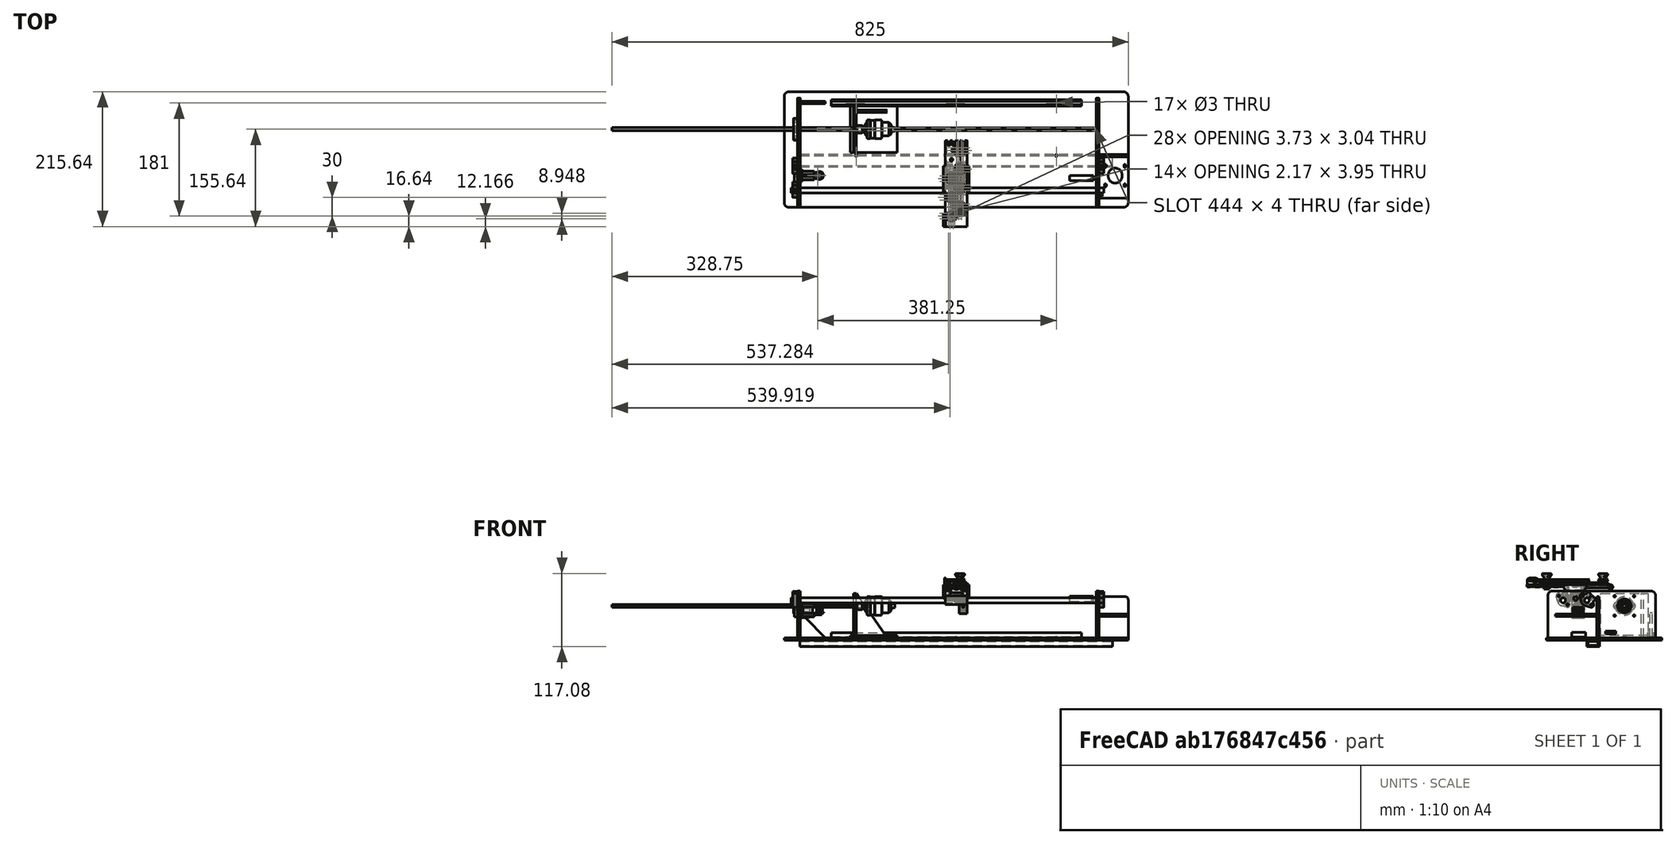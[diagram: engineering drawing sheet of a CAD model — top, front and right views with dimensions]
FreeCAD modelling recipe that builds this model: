
FCSTD DOCUMENT  (FreeCAD 0.18R16131 (Git))
Label: Nawijarka
License: All rights reserved
LicenseURL: http://en.wikipedia.org/wiki/All_rights_reserved
objects: Sketcher::SketchObject×83, PartDesign::Body×59, PartDesign::Pad×39, PartDesign::Pocket×37, PartDesign::FeatureBase×29, PartDesign::Mirrored×16, PartDesign::Revolution×7, Mesh::Feature×4, PartDesign::Chamfer×3, PartDesign::PolarPattern×3, PartDesign::MultiTransform×2, Spreadsheet::Sheet×1, PartDesign::LinearPattern×1, PartDesign::AdditiveCylinder×1, Part::Feature×1
note: 365 computed .brp shape members not serialized (recipe doc carries the construction recipe); baked Part::Feature solids carry a one-line shape summary decoded from their .brp

FEATURE [Sketcher::SketchObject] Sketch
  MapMode = 5
  Support = -> [XY_Plane]
  sketch-geometry (8):
    g0: LineSegment StartX=-267 StartY=110 StartZ=0 EndX=267 EndY=110 EndZ=0
    g1: LineSegment StartX=275 StartY=102 StartZ=0 EndX=275 EndY=-67 EndZ=0
    g2: LineSegment StartX=267 StartY=-75 StartZ=0 EndX=-267 EndY=-75 EndZ=0
    g3: LineSegment StartX=-275 StartY=-67 StartZ=0 EndX=-275 EndY=102 EndZ=0
    g4: ArcOfCircle CenterX=267 CenterY=102 CenterZ=0 NormalX=0 NormalY=0 NormalZ=1 AngleXU=0 Radius=8 StartAngle=6.6112e-12 EndAngle=1.5708
    g5: ArcOfCircle CenterX=267 CenterY=-67 CenterZ=0 NormalX=0 NormalY=0 NormalZ=1 AngleXU=0 Radius=8 StartAngle=4.71239 EndAngle=6.28319
    g6: ArcOfCircle CenterX=-267 CenterY=-67 CenterZ=0 NormalX=0 NormalY=0 NormalZ=1 AngleXU=0 Radius=8 StartAngle=3.14159 EndAngle=4.71239
    g7: ArcOfCircle CenterX=-267 CenterY=102 CenterZ=0 NormalX=0 NormalY=0 NormalZ=1 AngleXU=0 Radius=8 StartAngle=1.5708 EndAngle=3.14159
  constraints (19):
    c: Horizontal(g0)
    c: Horizontal(g2)
    c: Vertical(g1)
    c: Vertical(g3)
    c: Tangent(g0,g4) = 1.5708
    c: Tangent(g1,g4) = 1.5708
    c: Tangent(g2,g5) = 1.5708
    c: Tangent(g1,g5) = 1.5708
    c: Tangent(g2,g6) = 1.5708
    c: Tangent(g3,g6) = 1.5708
    c: Tangent(g3,g7) = 1.5708
    c: Tangent(g0,g7) = 1.5708
    c: Equal(g2,g0)
    c: Equal(g1,g3)
    c: Radius(g6) = 8
    c: DistanceX(g3,g1) = 550
    c: Symmetric(g6,g5,g-2)
    c: DistanceY(g2) = -75
    c: DistanceY(g0) = 110
FEATURE [Spreadsheet::Sheet] Spreadsheet  label="SS"
  cells = A2=thickness_; B2(thickness)==4mm
FEATURE [PartDesign::Pad] Pad
  Length = 4
  Length2 = 100
  Profile = -> Sketch
  Type = 0
  expr: Length = SS.thickness
FEATURE [Mesh::Feature] Motor_NEMA17
  Placement = pos=(254,-24,21) rot=(0,0,1;0rad)
FEATURE [Sketcher::SketchObject] Sketch001
  MapMode = 5
  Placement = pos=(0,0,0) rot=(0.57735,0.57735,0.57735;2.0944rad)
  Support = -> [YZ_Plane001]
  expr: Constraints[5] = SS.thickness
  sketch-geometry (6):
    g0: LineSegment StartX=-64.5 StartY=79 StartZ=0 EndX=92 EndY=79 EndZ=0
    g1: LineSegment StartX=100 StartY=71 StartZ=0 EndX=100 EndY=4 EndZ=0
    g2: LineSegment StartX=100 StartY=4 StartZ=0 EndX=-72.5 EndY=4 EndZ=0
    g3: LineSegment StartX=-72.5 StartY=4 StartZ=0 EndX=-72.5 EndY=71 EndZ=0
    g4: ArcOfCircle CenterX=-64.5 CenterY=71 CenterZ=0 NormalX=0 NormalY=0 NormalZ=1 AngleXU=0 Radius=8 StartAngle=1.5708 EndAngle=3.14159
    g5: ArcOfCircle CenterX=92 CenterY=71 CenterZ=0 NormalX=0 NormalY=0 NormalZ=1 AngleXU=0 Radius=8 StartAngle=7e-16 EndAngle=1.5708
  constraints (16):
    c: Coincident(g1,g2)
    c: Coincident(g2,g3)
    c: Horizontal(g0)
    c: Vertical(g1)
    c: Vertical(g3)
    c: DistanceY(g1) = 4
    c: Tangent(g0,g4) = 1.5708
    c: Tangent(g3,g4) = 1.5708
    c: Tangent(g0,g5) = 1.5708
    c: Tangent(g1,g5) = 1.5708
    c: Equal(g5,g4)
    c: Radius(g4) = 8
    c: DistanceY(g2,g0) = 75
    c: DistanceX(g2) = -72.5
    c: DistanceX(g-1,g1) = 100
    c: Horizontal(g2)
FEATURE [PartDesign::Pad] Pad001
  Length = 4
  Length2 = 100
  Placement = pos=(0,0,0) rot=(0.57735,0.57735,0.57735;2.0944rad)
  Profile = -> Sketch001
  Type = 0
  expr: Length = SS.thickness
FEATURE [Sketcher::SketchObject] Sketch002
  ExternalGeometry = -> [Pad001]
  MapMode = 5
  Placement = pos=(4,-9e-16,9e-16) rot=(0.57735,0.57735,0.57735;2.0944rad)
  Support = -> [Pad001]
  sketch-geometry (12):
    g0: Circle CenterX=-48 CenterY=64 CenterZ=0 NormalX=0 NormalY=0 NormalZ=1 AngleXU=0 Radius=3.9
    g1: Circle CenterX=-10 CenterY=64 CenterZ=0 NormalX=0 NormalY=0 NormalZ=1 AngleXU=0 Radius=3.9
    g2: Circle CenterX=-40.9289 CenterY=56.9289 CenterZ=0 NormalX=0 NormalY=0 NormalZ=1 AngleXU=0 Radius=1.5
    g3: Circle CenterX=-55.0711 CenterY=71.0711 CenterZ=0 NormalX=0 NormalY=0 NormalZ=1 AngleXU=0 Radius=1.5
    g4: Circle CenterX=-17.0711 CenterY=71.0711 CenterZ=0 NormalX=0 NormalY=0 NormalZ=1 AngleXU=0 Radius=1.5
    g5: Circle CenterX=-2.92893 CenterY=56.9289 CenterZ=0 NormalX=0 NormalY=0 NormalZ=1 AngleXU=0 Radius=1.5
    g6: LineSegment [constr] StartX=-55.0711 StartY=71.0711 StartZ=0 EndX=-40.9289 EndY=56.9289 EndZ=0
    g7: LineSegment [constr] StartX=-17.0711 StartY=71.0711 StartZ=0 EndX=-2.92893 EndY=56.9289 EndZ=0
    g8: LineSegment StartX=-32 StartY=53 StartZ=0 EndX=-16 EndY=53 EndZ=0
    g9: LineSegment StartX=-16 StartY=53 StartZ=0 EndX=-16 EndY=44 EndZ=0
    g10: LineSegment StartX=-16 StartY=44 StartZ=0 EndX=-32 EndY=44 EndZ=0
    g11: LineSegment StartX=-32 StartY=44 StartZ=0 EndX=-32 EndY=53 EndZ=0
  constraints (32):
    c: Equal(g1,g0)
    c: Radius(g0) = 3.9
    c: Coincident(g5,g7)
    c: Coincident(g2,g6)
    c: Coincident(g3,g6)
    c: Symmetric(g2,g3,g0)
    c: Symmetric(g4,g5,g1)
    c: Equal(g4,g5)
    c: Equal(g5,g2)
    c: Equal(g2,g3)
    c: Radius(g2) = 1.5
    c: Coincident(g4,g7)
    c: Equal(g7,g6)
    c: Distance(g4,g5) = 20
    c: Angle(g7) = -0.785398
    c: Angle(g6) = -0.785398
    c: Coincident(g8,g9)
    c: Coincident(g9,g10)
    c: Coincident(g10,g11)
    c: Coincident(g11,g8)
    c: Horizontal(g8)
    c: Horizontal(g10)
    c: Vertical(g9)
    c: Vertical(g11)
    c: DistanceX(g10,g10) = 16
    c: DistanceY(g11,g11) = 9
    c: DistanceY(g-3,g10) = 40
    c: DistanceY(g0) = 64
    c: Horizontal(g0,g1)
    c: DistanceX(g0,g1) = 38
    c: DistanceX(g1) = -10
    c: DistanceX(g9) = -16
FEATURE [PartDesign::Pocket] Pocket
  BaseFeature = -> Pad001
  Length = 5
  Length2 = 100
  Placement = pos=(0,0,0) rot=(0.57735,0.57735,0.57735;2.0944rad)
  Profile = -> Sketch002
  Type = 1
FEATURE [Sketcher::SketchObject] Sketch003
  MapMode = 5
  Placement = pos=(0,0,0) rot=(1,0,0;1.5708rad)
  Support = -> [XZ_Plane002]
  expr: Constraints[5] = SS.thickness
  sketch-geometry (5):
    g0: LineSegment StartX=0 StartY=4 StartZ=0 EndX=47 EndY=4 EndZ=0
    g1: LineSegment StartX=47 StartY=4 StartZ=0 EndX=47 EndY=65 EndZ=0
    g2: LineSegment StartX=42 StartY=70 StartZ=0 EndX=0 EndY=70 EndZ=0
    g3: LineSegment StartX=0 StartY=70 StartZ=0 EndX=0 EndY=4 EndZ=0
    g4: ArcOfCircle CenterX=42 CenterY=65 CenterZ=0 NormalX=0 NormalY=0 NormalZ=1 AngleXU=0 Radius=5 StartAngle=2e-16 EndAngle=1.5708
  constraints (14):
    c: Coincident(g0,g1)
    c: Coincident(g2,g3)
    c: Coincident(g3,g0)
    c: Horizontal(g0)
    c: Horizontal(g2)
    c: DistanceY(g0) = 4
    c: Vertical(g1)
    c: Tangent(g1,g4) = -1.5708
    c: Tangent(g2,g4) = -1.5708
    c: Radius(g4) = 5
    c: DistanceX(g-1,g0) = 47
    c: DistanceY(g2) = 70
    c: Vertical(g3)
    c: PointOnObject(g2,g-2)
FEATURE [PartDesign::Pad] Pad002
  Length = 4
  Length2 = 100
  Placement = pos=(0,0,0) rot=(1,0,0;1.5708rad)
  Profile = -> Sketch003
  Type = 0
  expr: Length = SS.thickness
FEATURE [PartDesign::Body] Body002  label="motor_plate_1"
  Group = -> [Sketch003,Pad002]
  Origin = -> Origin002
  Placement = pos=(228,-60,0) rot=(0,0,1;0rad)
  Tip = -> Pad002
FEATURE [PartDesign::FeatureBase] Clone
  BaseFeature = -> Body002
  Placement = pos=(230,-57,0) rot=(0,0,1;0rad)
FEATURE [PartDesign::Body] Body003  label="motor_plate_2"
  BaseFeature = -> Body002
  Group = -> [Clone]
  Origin = -> Origin003
  Placement = pos=(-2.1,66.7,0) rot=(0,0,1;0rad)
  Tip = -> Clone
FEATURE [Sketcher::SketchObject] Sketch004
  MapMode = 5
  Support = -> [XY_Plane004]
  sketch-geometry (4):
    g0: LineSegment StartX=-23.5 StartY=30 StartZ=0 EndX=23.5 EndY=30 EndZ=0
    g1: LineSegment StartX=23.5 StartY=30 StartZ=0 EndX=23.5 EndY=-36 EndZ=0
    g2: LineSegment StartX=23.5 StartY=-36 StartZ=0 EndX=-23.5 EndY=-36 EndZ=0
    g3: LineSegment StartX=-23.5 StartY=-36 StartZ=0 EndX=-23.5 EndY=30 EndZ=0
  constraints (11):
    c: Coincident(g0,g1)
    c: Coincident(g1,g2)
    c: Coincident(g2,g3)
    c: Coincident(g3,g0)
    c: Horizontal(g0)
    c: Vertical(g1)
    c: Vertical(g3)
    c: DistanceX(g2,g2) = 47
    c: DistanceY(g1) = -36
    c: DistanceY(g0) = 30
    c: Symmetric(g1,g2,g-2)
FEATURE [PartDesign::Pad] Pad003
  Length = 4
  Length2 = 100
  Profile = -> Sketch004
  Type = 0
  expr: Length = SS.thickness
FEATURE [Sketcher::SketchObject] Sketch005
  ExternalGeometry = -> [Pad003]
  MapMode = 5
  Placement = pos=(0,0,4) rot=(0,0,1;0rad)
  Support = -> [Pad003]
  sketch-geometry (25):
    g0: LineSegment [constr] StartX=-13 StartY=15.5 StartZ=0 EndX=18 EndY=15.5 EndZ=0
    g1: LineSegment [constr] StartX=18 StartY=15.5 StartZ=0 EndX=18 EndY=-15.5 EndZ=0
    g2: LineSegment [constr] StartX=18 StartY=-15.5 StartZ=0 EndX=-13 EndY=-15.5 EndZ=0
    g3: LineSegment [constr] StartX=-13 StartY=-15.5 StartZ=0 EndX=-13 EndY=15.5 EndZ=0
    g4: ArcOfCircle CenterX=2.5 CenterY=1 CenterZ=0 NormalX=0 NormalY=0 NormalZ=1 AngleXU=0 Radius=11 StartAngle=1e-16 EndAngle=3.14159
    g5: ArcOfCircle CenterX=2.5 CenterY=-1 CenterZ=0 NormalX=0 NormalY=0 NormalZ=1 AngleXU=0 Radius=11 StartAngle=3.14159 EndAngle=6.28319
    g6: LineSegment StartX=-8.5 StartY=1 StartZ=0 EndX=-8.5 EndY=-1 EndZ=0
    g7: LineSegment StartX=13.5 StartY=1 StartZ=0 EndX=13.5 EndY=-1 EndZ=0
    g8: ArcOfCircle CenterX=-13 CenterY=16.5 CenterZ=0 NormalX=0 NormalY=0 NormalZ=1 AngleXU=0 Radius=1.5 StartAngle=1e-15 EndAngle=3.14159
    g9: ArcOfCircle CenterX=-13 CenterY=14.5 CenterZ=0 NormalX=0 NormalY=0 NormalZ=1 AngleXU=0 Radius=1.5 StartAngle=3.14159 EndAngle=6.28319
    g10: LineSegment StartX=-14.5 StartY=16.5 StartZ=0 EndX=-14.5 EndY=14.5 EndZ=0
    g11: LineSegment StartX=-11.5 StartY=16.5 StartZ=0 EndX=-11.5 EndY=14.5 EndZ=0
    g12: ArcOfCircle CenterX=18 CenterY=16.5 CenterZ=0 NormalX=0 NormalY=0 NormalZ=1 AngleXU=0 Radius=1.5 StartAngle=-9e-16 EndAngle=3.14159
    g13: ArcOfCircle CenterX=18 CenterY=14.5 CenterZ=0 NormalX=0 NormalY=0 NormalZ=1 AngleXU=0 Radius=1.5 StartAngle=3.14159 EndAngle=6.28319
    g14: LineSegment StartX=16.5 StartY=16.5 StartZ=0 EndX=16.5 EndY=14.5 EndZ=0
    g15: LineSegment StartX=19.5 StartY=16.5 StartZ=0 EndX=19.5 EndY=14.5 EndZ=0
    g16: ArcOfCircle CenterX=18 CenterY=-14.5 CenterZ=0 NormalX=0 NormalY=0 NormalZ=1 AngleXU=0 Radius=1.5 StartAngle=6e-16 EndAngle=3.14159
    g17: ArcOfCircle CenterX=18 CenterY=-16.5 CenterZ=0 NormalX=0 NormalY=0 NormalZ=1 AngleXU=0 Radius=1.5 StartAngle=3.14159 EndAngle=6.28319
    g18: LineSegment StartX=16.5 StartY=-14.5 StartZ=0 EndX=16.5 EndY=-16.5 EndZ=0
    g19: LineSegment StartX=19.5 StartY=-14.5 StartZ=0 EndX=19.5 EndY=-16.5 EndZ=0
    g20: ArcOfCircle CenterX=-13 CenterY=-14.5 CenterZ=0 NormalX=0 NormalY=0 NormalZ=1 AngleXU=0 Radius=1.5 StartAngle=2e-16 EndAngle=3.14159
    g21: ArcOfCircle CenterX=-13 CenterY=-16.5 CenterZ=0 NormalX=0 NormalY=0 NormalZ=1 AngleXU=0 Radius=1.5 StartAngle=3.14159 EndAngle=6.28319
    g22: LineSegment StartX=-14.5 StartY=-14.5 StartZ=0 EndX=-14.5 EndY=-16.5 EndZ=0
    g23: LineSegment StartX=-11.5 StartY=-14.5 StartZ=0 EndX=-11.5 EndY=-16.5 EndZ=0
    g24: GeomPoint X=2.5 Y=6e-16 Z=0
  constraints (57):
    c: Coincident(g0,g1)
    c: Coincident(g1,g2)
    c: Coincident(g2,g3)
    c: Coincident(g3,g0)
    c: Horizontal(g0)
    c: Horizontal(g2)
    c: Vertical(g3)
    c: Equal(g2,g1)
    c: DistanceX(g2,g2) = 31
    c: Tangent(g4,g7) = 1.5708
    c: Tangent(g4,g6) = -1.5708
    c: Tangent(g6,g5) = -1.5708
    c: Tangent(g7,g5) = 1.5708
    c: Vertical(g6)
    c: Tangent(g8,g11) = 1.5708
    c: Tangent(g8,g10) = -1.5708
    c: Tangent(g10,g9) = -1.5708
    c: Tangent(g11,g9) = 1.5708
    c: Vertical(g10)
    c: Equal(g8,g9)
    c: Tangent(g12,g15) = 1.5708
    c: Tangent(g12,g14) = -1.5708
    c: Tangent(g14,g13) = -1.5708
    c: Tangent(g15,g13) = 1.5708
    c: Vertical(g14)
    c: Equal(g12,g13)
    c: Tangent(g16,g19) = 1.5708
    c: Tangent(g16,g18) = -1.5708
    c: Tangent(g18,g17) = -1.5708
    c: Tangent(g19,g17) = 1.5708
    c: Vertical(g18)
    c: Equal(g16,g17)
    c: Tangent(g20,g23) = 1.5708
    c: Tangent(g20,g22) = -1.5708
    c: Tangent(g22,g21) = -1.5708
    c: Tangent(g23,g21) = 1.5708
    c: Vertical(g22)
    c: Equal(g20,g21)
    c: Symmetric(g8,g9,g0)
    c: Symmetric(g20,g21,g2)
    c: Symmetric(g16,g17,g1)
    c: Symmetric(g13,g12,g0)
    c: Radius(g13) = 1.5
    c: Equal(g13,g9)
    c: Equal(g13,g20)
    c: Equal(g13,g16)
    c: Equal(g18,g22)
    c: Equal(g22,g10)
    c: Equal(g10,g14)
    c: DistanceY(g10,g10) = 2
    c: DistanceY(g6,g6) = 2
    c: Radius(g4) = 11
    c: Symmetric(g5,g4,g-1)
    c: Symmetric(g1,g0,g-1)
    c: Vertical(g5,g24)
    c: Symmetric(g1,g0,g24)
    c: DistanceX(g24,g-3) = 21
FEATURE [PartDesign::Pocket] Pocket001
  BaseFeature = -> Pad003
  Length = 5
  Length2 = 100
  Profile = -> Sketch005
  Type = 1
FEATURE [Sketcher::SketchObject] Sketch006
  MapMode = 5
  Placement = pos=(4,-9e-16,9e-16) rot=(0.57735,0.57735,0.57735;2.0944rad)
  Support = -> [Pocket]
  expr: Constraints[10] = SS.thickness + 1mm
  sketch-geometry (4):
    g0: LineSegment StartX=-34 StartY=13 StartZ=0 EndX=-12 EndY=13 EndZ=0
    g1: LineSegment StartX=-12 StartY=13 StartZ=0 EndX=-12 EndY=5 EndZ=0
    g2: LineSegment StartX=-12 StartY=5 StartZ=0 EndX=-34 EndY=5 EndZ=0
    g3: LineSegment StartX=-34 StartY=5 StartZ=0 EndX=-34 EndY=13 EndZ=0
  constraints (12):
    c: Coincident(g0,g1)
    c: Coincident(g1,g2)
    c: Coincident(g2,g3)
    c: Coincident(g3,g0)
    c: Horizontal(g0)
    c: Horizontal(g2)
    c: Vertical(g1)
    c: Vertical(g3)
    c: DistanceX(g2,g2) = 22
    c: DistanceY(g1,g1) = 8
    c: DistanceY(g1) = 5
    c: DistanceX(g0) = -12
FEATURE [PartDesign::Pocket] Pocket002
  BaseFeature = -> Pocket
  Length = 5
  Length2 = 100
  Placement = pos=(0,0,0) rot=(0.57735,0.57735,0.57735;2.0944rad)
  Profile = -> Sketch006
  Type = 1
FEATURE [Sketcher::SketchObject] Sketch008
  MapMode = 5
  Placement = pos=(0,0,0) rot=(0.707107,0,0.707107;3.14159rad)
  sketch-geometry (17):
    g0: ArcOfCircle CenterX=-3e-16 CenterY=0 CenterZ=0 NormalX=0 NormalY=0 NormalZ=1 AngleXU=0 Radius=9 StartAngle=4.18879 EndAngle=5.23599
    g1: ArcOfCircle CenterX=10 CenterY=-3e-16 CenterZ=0 NormalX=0 NormalY=0 NormalZ=1 AngleXU=0 Radius=4 StartAngle=5.23599 EndAngle=7.33038
    g2: ArcOfCircle CenterX=-10 CenterY=3e-16 CenterZ=0 NormalX=0 NormalY=0 NormalZ=1 AngleXU=0 Radius=4 StartAngle=2.0944 EndAngle=4.18879
    g3: LineSegment StartX=-12 StartY=3.4641 StartZ=0 EndX=-8.5 EndY=5.48483 EndZ=0
    g4: LineSegment StartX=8.5 StartY=5.48483 StartZ=0 EndX=12 EndY=3.4641 EndZ=0
    g5: LineSegment StartX=12 StartY=-3.4641 StartZ=0 EndX=4.5 EndY=-7.79423 EndZ=0
    g6: LineSegment StartX=-4.5 StartY=-7.79423 StartZ=0 EndX=-12 EndY=-3.4641 EndZ=0
    g7: GeomPoint X=0 Y=-9 Z=0
    g8: Circle CenterX=-10 CenterY=3e-16 CenterZ=0 NormalX=0 NormalY=0 NormalZ=1 AngleXU=0 Radius=1.5
    g9: Circle CenterX=10 CenterY=-3e-16 CenterZ=0 NormalX=0 NormalY=0 NormalZ=1 AngleXU=0 Radius=1.5
    g10: ArcOfCircle CenterX=-3e-16 CenterY=0 CenterZ=0 NormalX=0 NormalY=0 NormalZ=1 AngleXU=0 Radius=4 StartAngle=1.69612 EndAngle=7.72865
    g11: LineSegment StartX=-8.5 StartY=5.48483 StartZ=0 EndX=-8.5 EndY=11.4848 EndZ=0
    g12: LineSegment StartX=-8.5 StartY=11.4848 StartZ=0 EndX=-0.5 EndY=11.4848 EndZ=0
    g13: LineSegment StartX=-0.5 StartY=11.4848 StartZ=0 EndX=-0.5 EndY=3.96863 EndZ=0
    g14: LineSegment StartX=0.5 StartY=3.96863 StartZ=0 EndX=0.5 EndY=11.4848 EndZ=0
    g15: LineSegment StartX=0.5 StartY=11.4848 StartZ=0 EndX=8.5 EndY=11.4848 EndZ=0
    g16: LineSegment StartX=8.5 StartY=11.4848 StartZ=0 EndX=8.5 EndY=5.48483 EndZ=0
  constraints (41):
    c: Tangent(g2,g3) = 1.5708
    c: Tangent(g1,g4) = 1.5708
    c: Tangent(g1,g5) = 1.5708
    c: Tangent(g0,g5) = 1.5708
    c: Tangent(g0,g6) = 1.5708
    c: Tangent(g2,g6) = 1.5708
    c: DistanceX(g2,g1) = 20
    c: Symmetric(g2,g1,g-1)
    c: Radius(g1) = 4
    c: PointOnObject(g7,g0)
    c: PointOnObject(g7,g-2)
    c: Coincident(g1,g9)
    c: Coincident(g2,g8)
    c: Equal(g8,g9)
    c: Radius(g8) = 1.5
    c: Radius(g10) = 4
    c: Symmetric(g4,g3,g-2)
    c: Symmetric(g0,g0,g-2)
    c: DistanceY(g7,g0) = 9
    c: Equal(g6,g5)
    c: Coincident(g11,g12)
    c: Coincident(g12,g13)
    c: Coincident(g14,g15)
    c: Coincident(g15,g16)
    c: Vertical(g16)
    c: Vertical(g11)
    c: Horizontal(g12)
    c: Horizontal(g15)
    c: Symmetric(g12,g14,g-2)
    c: Coincident(g10,g14)
    c: Coincident(g10,g13)
    c: DistanceX(g10,g10) = 1
    c: DistanceX(g12,g14) = 1
    c: Coincident(g0,g10)
    c: Coincident(g0,g-1)
    c: Symmetric(g10,g10,g-2)
    c: Coincident(g3,g11)
    c: Coincident(g4,g16)
    c: DistanceX(g3,g10) = 8
    c: DistanceY(g11,g11) = 6
    c: Symmetric(g2,g2,g-1)
FEATURE [PartDesign::Pad] Pad004
  Length = 8
  Length2 = 100
  Placement = pos=(0,0,0) rot=(0.707107,0,0.707107;3.14159rad)
  Profile = -> Sketch008
  Type = 0
FEATURE [Sketcher::SketchObject] Sketch009
  ExternalGeometry = -> [Pad004]
  MapMode = 5
  Placement = pos=(-1.9e-15,8e-16,-8.5) rot=(0.707107,0.707107,0;3.14159rad)
  Support = -> [Pad004]
  sketch-geometry (1):
    g0: Circle CenterX=-7.72673 CenterY=4 CenterZ=0 NormalX=0 NormalY=0 NormalZ=1 AngleXU=0 Radius=1.5
  constraints (2):
    c: Symmetric(g-4,g-3,g0)
    c: Radius(g0) = 1.5
FEATURE [PartDesign::Pocket] Pocket003
  BaseFeature = -> Pad004
  Length = 5
  Length2 = 100
  Placement = pos=(0,0,0) rot=(0.707107,0,0.707107;3.14159rad)
  Profile = -> Sketch009
  Type = 1
FEATURE [Sketcher::SketchObject] Sketch010
  ExternalGeometry = -> [Pocket003]
  MapMode = 5
  Placement = pos=(-1.9e-15,8e-16,-8.5) rot=(0.707107,0.707107,0;3.14159rad)
  Support = -> [Pocket003]
  sketch-geometry (1):
    g0: Circle CenterX=-7.72673 CenterY=4 CenterZ=0 NormalX=0 NormalY=0 NormalZ=1 AngleXU=0 Radius=3.4
  constraints (2):
    c: Radius(g0) = 3.4
    c: Coincident(g0,g-3)
FEATURE [PartDesign::Pocket] Pocket004
  BaseFeature = -> Pocket003
  Length = 1
  Length2 = 100
  Placement = pos=(0,0,0) rot=(0.707107,0,0.707107;3.14159rad)
  Profile = -> Sketch010
  Type = 4
FEATURE [Sketcher::SketchObject] Sketch011
  ExternalGeometry = -> [Pocket004]
  MapMode = 5
  Placement = pos=(1.9e-15,-8e-16,8.5) rot=(0,0,-1;1.5708rad)
  Support = -> [Pocket004]
  sketch-geometry (1):
    g0: Circle CenterX=7.72673 CenterY=4 CenterZ=0 NormalX=0 NormalY=0 NormalZ=1 AngleXU=0 Radius=2
  constraints (2):
    c: Coincident(g0,g-3)
    c: Radius(g0) = 2
FEATURE [PartDesign::Pocket] Pocket005
  BaseFeature = -> Pocket004
  Length = 4
  Length2 = 100
  Placement = pos=(0,0,0) rot=(0.707107,0,0.707107;3.14159rad)
  Profile = -> Sketch011
  Type = 4
FEATURE [PartDesign::Chamfer] Chamfer
  Base = -> Pocket005 [Edge40,Edge48]
  BaseFeature = -> Pocket005
  Placement = pos=(0,0,0) rot=(0.707107,0,0.707107;3.14159rad)
  Size = 0.2
FEATURE [Sketcher::SketchObject] Sketch012
  ExternalGeometry = -> [Chamfer]
  MapMode = 5
  Placement = pos=(0,0,0) rot=(0,-1,0;1.5708rad)
  Support = -> [Chamfer]
  sketch-geometry (2):
    g0: Circle CenterX=-10 CenterY=0 CenterZ=0 NormalX=0 NormalY=0 NormalZ=1 AngleXU=0 Radius=2
    g1: Circle CenterX=10 CenterY=-3.8e-15 CenterZ=0 NormalX=0 NormalY=0 NormalZ=1 AngleXU=0 Radius=2
  constraints (4):
    c: Radius(g1) = 2
    c: Equal(g1,g0)
    c: Coincident(g0,g-4)
    c: Coincident(g1,g-3)
FEATURE [PartDesign::Pocket] Pocket006
  BaseFeature = -> Chamfer
  Length = 4
  Length2 = 100
  Placement = pos=(0,0,0) rot=(0.707107,0,0.707107;3.14159rad)
  Profile = -> Sketch012
  Type = 0
FEATURE [PartDesign::Body] Body005  label="shaft_support_2"
  Group = -> [Sketch008,Pad004,Sketch009,Pocket003,Sketch010,Pocket004,Sketch011,Pocket005,Chamfer,Sketch012,Pocket006]
  Origin = -> Origin005
  Placement = pos=(227.8,-47.9889,63.9702) rot=(1,0,0;3.92699rad)
  Tip = -> Pocket006
FEATURE [PartDesign::FeatureBase] Clone001
  BaseFeature = -> Body005
  Placement = pos=(228,-45.019,63.9702) rot=(1,0,0;3.92699rad)
FEATURE [PartDesign::Body] Body006  label="shart_support_1"
  BaseFeature = -> Body005
  Group = -> [Clone001]
  Origin = -> Origin006
  Placement = pos=(-0.1,35,0) rot=(0,0,1;0rad)
  Tip = -> Clone001
FEATURE [Mesh::Feature] GT2_16T_Pulley_for_Alu_CNC
  Placement = pos=(254,-23.9698,58.043) rot=(1,0,0;3.14159rad)
FEATURE [Sketcher::SketchObject] Sketch013
  MapMode = 5
  Placement = pos=(0,0,0) rot=(0.57735,0.57735,0.57735;2.0944rad)
  Support = -> [YZ_Plane007]
  sketch-geometry (1):
    g0: Circle CenterX=0 CenterY=0 CenterZ=0 NormalX=0 NormalY=0 NormalZ=1 AngleXU=0 Radius=4
  constraints (2):
    c: Radius(g0) = 4
    c: Coincident(g0,g-1)
FEATURE [PartDesign::Pad] Pad005
  Length = 500
  Length2 = 100
  Midplane = true
  Placement = pos=(0,0,0) rot=(0.57735,0.57735,0.57735;2.0944rad)
  Profile = -> Sketch013
  Type = 0
FEATURE [PartDesign::Body] Body007  label="rod_1"
  Group = -> [Sketch013,Pad005]
  Origin = -> Origin007
  Placement = pos=(-14,-10,64) rot=(0,0,1;0rad)
  Tip = -> Pad005
FEATURE [PartDesign::FeatureBase] Clone002
  BaseFeature = -> Body007
  Placement = pos=(-14.1,-10,64) rot=(0,0,1;0rad)
FEATURE [PartDesign::Body] Body008  label="rod_2"
  BaseFeature = -> Body007
  Group = -> [Clone002]
  Origin = -> Origin008
  Placement = pos=(0,-38,0) rot=(0,0,1;0rad)
  Tip = -> Clone002
FEATURE [Sketcher::SketchObject] Sketch014
  MapMode = 5
  Placement = pos=(0,0,0) rot=(0.57735,0.57735,0.57735;2.0944rad)
  Support = -> [YZ_Plane009]
  sketch-geometry (16):
    g0: ArcOfCircle CenterX=-19 CenterY=0 CenterZ=0 NormalX=0 NormalY=0 NormalZ=1 AngleXU=0 Radius=4.05 StartAngle=1.5708 EndAngle=6.96426
    g1: ArcOfCircle CenterX=-19 CenterY=0 CenterZ=0 NormalX=0 NormalY=0 NormalZ=1 AngleXU=0 Radius=7 StartAngle=1.5708 EndAngle=6.21886
    g2: LineSegment StartX=-19 StartY=7 StartZ=0 EndX=-3.85973 EndY=7 EndZ=0
    g3: LineSegment StartX=-19 StartY=4.05 StartZ=0 EndX=0 EndY=4.05 EndZ=0
    g4: LineSegment StartX=-15.8536 StartY=2.55 StartZ=0 EndX=-8 EndY=2.55 EndZ=0
    g5: LineSegment StartX=-8 StartY=2.55 StartZ=0 EndX=-8 EndY=-0.45 EndZ=0
    g6: LineSegment StartX=-8 StartY=-0.45 StartZ=0 EndX=-12.0145 EndY=-0.45 EndZ=0
    g7: ArcOfCircle CenterX=0 CenterY=8.05 CenterZ=0 NormalX=0 NormalY=0 NormalZ=1 AngleXU=0 Radius=4 StartAngle=6.01757 EndAngle=9.69039
    g8: ArcOfCircle CenterX=19 CenterY=2e-16 CenterZ=0 NormalX=0 NormalY=0 NormalZ=1 AngleXU=0 Radius=4.05 StartAngle=2.46052 EndAngle=7.85398
    g9: ArcOfCircle CenterX=19 CenterY=2e-16 CenterZ=0 NormalX=0 NormalY=0 NormalZ=1 AngleXU=0 Radius=7 StartAngle=3.20592 EndAngle=7.85398
    g10: LineSegment StartX=19 StartY=7 StartZ=0 EndX=3.85973 EndY=7 EndZ=0
    g11: LineSegment StartX=19 StartY=4.05 StartZ=0 EndX=0 EndY=4.05 EndZ=0
    g12: LineSegment StartX=15.8536 StartY=2.55 StartZ=0 EndX=8 EndY=2.55 EndZ=0
    g13: LineSegment StartX=8 StartY=2.55 StartZ=0 EndX=8 EndY=-0.45 EndZ=0
    g14: LineSegment StartX=8 StartY=-0.45 StartZ=0 EndX=12.0145 EndY=-0.45 EndZ=0
    g15: Circle CenterX=0 CenterY=8.05 CenterZ=0 NormalX=0 NormalY=0 NormalZ=1 AngleXU=0 Radius=2.5
  constraints (45):
    c: Horizontal(g2)
    c: Tangent(g1,g2) = 1.5708
    c: Horizontal(g3)
    c: Tangent(g0,g3) = 1.5708
    c: Coincident(g0,g1)
    c: DistanceX(g0,g-1) = 19
    c: Radius(g0) = 4.05
    c: PointOnObject(g0,g-1)
    c: Coincident(g5,g6)
    c: Coincident(g1,g6)
    c: Coincident(g0,g4)
    c: Coincident(g4,g5)
    c: Horizontal(g6)
    c: Horizontal(g4)
    c: Vertical(g5)
    c: Radius(g1) = 7
    c: DistanceY(g5,g5) = 3
    c: DistanceY(g4,g3) = 1.5
    c: DistanceX(g0,g5) = 11
    c: Coincident(g2,g7)
    c: Radius(g7) = 4
    c: Horizontal(g10)
    c: Tangent(g9,g10) = -1.5708
    c: Horizontal(g11)
    c: Tangent(g8,g11) = -1.5708
    c: Coincident(g8,g9)
    c: Coincident(g13,g14)
    c: Coincident(g9,g14)
    c: Coincident(g8,g12)
    c: Coincident(g12,g13)
    c: Horizontal(g14)
    c: Horizontal(g12)
    c: Vertical(g13)
    c: Equal(g13,g5)
    c: Equal(g8,g0)
    c: Equal(g10,g2)
    c: Equal(g14,g6)
    c: Symmetric(g13,g5,g-2)
    c: Coincident(g7,g10)
    c: PointOnObject(g15,g-2)
    c: Radius(g15) = 2.5
    c: Coincident(g3,g11)
    c: PointOnObject(g3,g-2)
    c: Coincident(g7,g15)
    c: DistanceY(g3,g7) = 4
FEATURE [PartDesign::Pad] Pad006
  Length = 35
  Length2 = 100
  Midplane = true
  Placement = pos=(0,0,0) rot=(0.57735,0.57735,0.57735;2.0944rad)
  Profile = -> Sketch014
  Type = 0
FEATURE [Sketcher::SketchObject] Sketch015
  ExternalGeometry = -> [Pad006]
  MapMode = 5
  Placement = pos=(1e-16,-2e-16,-0.45) rot=(0.707107,0.707107,0;3.14159rad)
  Support = -> [Pad006]
  sketch-geometry (5):
    g0: ArcOfCircle CenterX=-12.0145 CenterY=0 CenterZ=0 NormalX=0 NormalY=0 NormalZ=1 AngleXU=0 Radius=4.01448 StartAngle=0 EndAngle=0.183728
    g1: ArcOfCircle CenterX=-12.0145 CenterY=16.5 CenterZ=0 NormalX=0 NormalY=0 NormalZ=1 AngleXU=0 Radius=1 StartAngle=0.183728 EndAngle=1.5708
    g2: LineSegment StartX=-11.0313 StartY=16.6827 StartZ=0 EndX=-8.06757 EndY=0.733428 EndZ=0
    g3: LineSegment StartX=-8 StartY=0 StartZ=0 EndX=-8 EndY=17.5 EndZ=0
    g4: LineSegment StartX=-8 StartY=17.5 StartZ=0 EndX=-12.0145 EndY=17.5 EndZ=0
  constraints (12):
    c: Coincident(g3,g4)
    c: Tangent(g0,g2) = 1.5708
    c: Coincident(g0,g3)
    c: PointOnObject(g0,g-3)
    c: Tangent(g1,g2) = 1.5708
    c: Coincident(g3,g-3)
    c: Horizontal(g0,g-1)
    c: PointOnObject(g0,g-1)
    c: Coincident(g4,g-4)
    c: Tangent(g1,g4) = -1.5708
    c: Radius(g1) = 1
    c: PointOnObject(g0,g-4)
FEATURE [PartDesign::Pocket] Pocket007
  BaseFeature = -> Pad006
  Length = 4
  Length2 = 100
  Placement = pos=(0,0,0) rot=(0.57735,0.57735,0.57735;2.0944rad)
  Profile = -> Sketch015
  Type = 0
FEATURE [PartDesign::Mirrored] Mirrored
  MirrorPlane = -> YZ_Plane009
  Placement = pos=(0,0,0) rot=(0.57735,0.57735,0.57735;2.0944rad)
FEATURE [PartDesign::Mirrored] Mirrored001
  MirrorPlane = -> XZ_Plane009
  Placement = pos=(0,0,0) rot=(0.57735,0.57735,0.57735;2.0944rad)
FEATURE [PartDesign::MultiTransform] MultiTransform
  BaseFeature = -> Pocket007
  Originals = -> [Pocket007]
  Placement = pos=(0,0,0) rot=(0.57735,0.57735,0.57735;2.0944rad)
  Transformations = -> [Mirrored,Mirrored001]
FEATURE [Sketcher::SketchObject] Sketch016
  ExternalGeometry = -> [MultiTransform]
  MapMode = 5
  Placement = pos=(-2e-15,3.1e-15,7) rot=(0,0,-1;1.5708rad)
  Support = -> [MultiTransform]
  sketch-geometry (1):
    g0: Circle CenterX=-11.5 CenterY=0 CenterZ=0 NormalX=0 NormalY=0 NormalZ=1 AngleXU=0 Radius=1.5
  constraints (3):
    c: Radius(g0) = 1.5
    c: PointOnObject(g0,g-1)
    c: DistanceX(g-3,g0) = 7.5
FEATURE [PartDesign::Pocket] Pocket008
  BaseFeature = -> MultiTransform
  Length = 5
  Length2 = 100
  Placement = pos=(0,0,0) rot=(0.57735,0.57735,0.57735;2.0944rad)
  Profile = -> Sketch016
  Type = 1
FEATURE [Sketcher::SketchObject] Sketch017
  ExternalGeometry = -> [Pocket008]
  MapMode = 5
  Placement = pos=(1e-16,-2e-16,-0.45) rot=(0.707107,0.707107,0;3.14159rad)
  Support = -> [Pocket008]
  sketch-geometry (1):
    g0: Circle CenterX=11.5 CenterY=-1.7e-15 CenterZ=0 NormalX=0 NormalY=0 NormalZ=1 AngleXU=0 Radius=2
  constraints (2):
    c: Radius(g0) = 2
    c: Coincident(g0,g-3)
FEATURE [PartDesign::Pocket] Pocket009
  BaseFeature = -> Pocket008
  Length = 2
  Length2 = 100
  Placement = pos=(0,0,0) rot=(0.57735,0.57735,0.57735;2.0944rad)
  Profile = -> Sketch017
  Type = 4
FEATURE [Sketcher::SketchObject] Sketch018
  ExternalGeometry = -> [Pocket009]
  MapMode = 5
  Placement = pos=(1e-16,-2e-16,-0.45) rot=(0.707107,0.707107,0;3.14159rad)
  Support = -> [Pocket009]
  sketch-geometry (2):
    g0: Circle CenterX=11.5 CenterY=2.05e-14 CenterZ=0 NormalX=0 NormalY=0 NormalZ=1 AngleXU=0 Radius=3.5
    g1: Circle CenterX=11.5 CenterY=2.05e-14 CenterZ=0 NormalX=0 NormalY=0 NormalZ=1 AngleXU=0 Radius=2
  constraints (4):
    c: Coincident(g0,g-3)
    c: Radius(g0) = 3.5
    c: Radius(g1) = 2
    c: Coincident(g0,g1)
FEATURE [PartDesign::Pad] Pad007
  BaseFeature = -> Pocket009
  Length = 2
  Length2 = 100
  Placement = pos=(0,0,0) rot=(0.57735,0.57735,0.57735;2.0944rad)
  Profile = -> Sketch018
  Type = 0
FEATURE [PartDesign::Mirrored] Mirrored002
  BaseFeature = -> Pad007
  MirrorPlane = -> Sketch016 [V_Axis]
  Originals = -> [Pocket008]
  Placement = pos=(0,0,0) rot=(0.57735,0.57735,0.57735;2.0944rad)
FEATURE [PartDesign::Mirrored] Mirrored003
  BaseFeature = -> Mirrored002
  MirrorPlane = -> Sketch017 [V_Axis]
  Originals = -> [Pocket009]
  Placement = pos=(0,0,0) rot=(0.57735,0.57735,0.57735;2.0944rad)
FEATURE [PartDesign::Mirrored] Mirrored004
  BaseFeature = -> Mirrored003
  MirrorPlane = -> Sketch018 [V_Axis]
  Originals = -> [Pad007]
  Placement = pos=(0,0,0) rot=(0.57735,0.57735,0.57735;2.0944rad)
FEATURE [PartDesign::Chamfer] Chamfer001
  Base = -> Mirrored004 [Edge103,Edge113]
  BaseFeature = -> Mirrored004
  Placement = pos=(0,0,0) rot=(0.57735,0.57735,0.57735;2.0944rad)
  Size = 1
FEATURE [Sketcher::SketchObject] Sketch019
  ExternalGeometry = -> [Chamfer001]
  MapMode = 5
  Placement = pos=(-1.1e-15,1.8e-15,4.05) rot=(0.707107,0.707107,0;3.14159rad)
  Support = -> [Chamfer001]
  sketch-geometry (4):
    g0: LineSegment StartX=-11.0313 StartY=17.5 StartZ=0 EndX=-9.03131 EndY=17.5 EndZ=0
    g1: LineSegment StartX=-9.03131 StartY=17.5 StartZ=0 EndX=11.0313 EndY=-17.5 EndZ=0
    g2: LineSegment StartX=11.0313 StartY=-17.5 StartZ=0 EndX=9.03131 EndY=-17.5 EndZ=0
    g3: LineSegment StartX=9.03131 StartY=-17.5 StartZ=0 EndX=-11.0313 EndY=17.5 EndZ=0
  constraints (12):
    c: Coincident(g0,g1)
    c: Coincident(g1,g2)
    c: Coincident(g2,g3)
    c: Coincident(g3,g0)
    c: Horizontal(g0)
    c: Horizontal(g2)
    c: Horizontal(g2,g-3)
    c: Horizontal(g1,g-4)
    c: Vertical(g3,g-5)
    c: Vertical(g2,g-6)
    c: Parallel(g3,g1)
    c: DistanceX(g2,g2) = 2
FEATURE [PartDesign::Pad] Pad008
  BaseFeature = -> Chamfer001
  Length = 2
  Length2 = 100
  Placement = pos=(0,0,0) rot=(0.57735,0.57735,0.57735;2.0944rad)
  Profile = -> Sketch019
  Type = 0
FEATURE [PartDesign::Mirrored] Mirrored005
  BaseFeature = -> Pad008
  MirrorPlane = -> Sketch019 [V_Axis]
  Originals = -> [Pad008]
  Placement = pos=(0,0,0) rot=(0.57735,0.57735,0.57735;2.0944rad)
FEATURE [Sketcher::SketchObject] Sketch020
  ExternalGeometry = -> [Mirrored005]
  MapMode = 5
  Placement = pos=(-1.1e-15,1.8e-15,4.05) rot=(0.707107,0.707107,0;3.14159rad)
  Support = -> [Mirrored005]
  sketch-geometry (8):
    g0: LineSegment StartX=-9.03131 StartY=17.5 StartZ=0 EndX=9.03131 EndY=17.5 EndZ=0
    g1: LineSegment StartX=9.03131 StartY=17.5 StartZ=0 EndX=9.03131 EndY=15.5 EndZ=0
    g2: LineSegment StartX=9.03131 StartY=15.5 StartZ=0 EndX=-9.03131 EndY=15.5 EndZ=0
    g3: LineSegment StartX=-9.03131 StartY=15.5 StartZ=0 EndX=-9.03131 EndY=17.5 EndZ=0
    g4: LineSegment StartX=-9.03131 StartY=-17.5 StartZ=0 EndX=9.03131 EndY=-17.5 EndZ=0
    g5: LineSegment StartX=9.03131 StartY=-17.5 StartZ=0 EndX=9.03131 EndY=-15.5 EndZ=0
    g6: LineSegment StartX=9.03131 StartY=-15.5 StartZ=0 EndX=-9.03131 EndY=-15.5 EndZ=0
    g7: LineSegment StartX=-9.03131 StartY=-15.5 StartZ=0 EndX=-9.03131 EndY=-17.5 EndZ=0
  constraints (20):
    c: Coincident(g0,g1)
    c: Coincident(g1,g2)
    c: Coincident(g2,g3)
    c: Coincident(g3,g0)
    c: Horizontal(g2)
    c: Vertical(g1)
    c: Vertical(g3)
    c: Symmetric(g0,g0,g-2)
    c: DistanceY(g3,g3) = 2
    c: Coincident(g0,g-3)
    c: Coincident(g4,g5)
    c: Coincident(g5,g6)
    c: Coincident(g6,g7)
    c: Coincident(g7,g4)
    c: Horizontal(g6)
    c: Vertical(g5)
    c: Vertical(g7)
    c: Coincident(g4,g-4)
    c: Symmetric(g4,g4,g-2)
    c: Equal(g7,g3)
FEATURE [PartDesign::Pad] Pad009
  BaseFeature = -> Mirrored005
  Length = 2
  Length2 = 100
  Placement = pos=(0,0,0) rot=(0.57735,0.57735,0.57735;2.0944rad)
  Profile = -> Sketch020
  Type = 0
FEATURE [Sketcher::SketchObject] Sketch021
  ExternalGeometry = -> [Pad009]
  MapMode = 5
  Placement = pos=(17.5,-3.8e-15,3.8e-15) rot=(0.57735,0.57735,0.57735;2.0944rad)
  Support = -> [Pad009]
  sketch-geometry (2):
    g0: Circle CenterX=0 CenterY=8.05 CenterZ=0 NormalX=0 NormalY=0 NormalZ=1 AngleXU=0 Radius=7.5
    g1: Circle CenterX=0 CenterY=8.05 CenterZ=0 NormalX=0 NormalY=0 NormalZ=1 AngleXU=0 Radius=2.5
  constraints (5):
    c: Radius(g-3) = 4
    c: Radius(g0) = 7.5
    c: Coincident(g0,g-3)
    c: Coincident(g0,g1)
    c: Equal(g1,g-4)
FEATURE [PartDesign::Pad] Pad010
  BaseFeature = -> Pad009
  Length = 8
  Length2 = 100
  Placement = pos=(0,0,0) rot=(0.57735,0.57735,0.57735;2.0944rad)
  Profile = -> Sketch021
  Reversed = true
  Type = 0
FEATURE [Sketcher::SketchObject] Sketch022
  ExternalGeometry = -> [Pad010]
  MapMode = 5
  Placement = pos=(17.5,-3.8e-15,3.8e-15) rot=(0.57735,0.57735,0.57735;2.0944rad)
  Support = -> [Pad010]
  sketch-geometry (1):
    g0: Circle CenterX=0 CenterY=8.05 CenterZ=0 NormalX=0 NormalY=0 NormalZ=1 AngleXU=0 Radius=5.5
  constraints (2):
    c: Coincident(g0,g-3)
    c: Radius(g0) = 5.5
FEATURE [PartDesign::Pocket] Pocket010
  BaseFeature = -> Pad010
  Length = 5
  Length2 = 100
  Placement = pos=(0,0,0) rot=(0.57735,0.57735,0.57735;2.0944rad)
  Profile = -> Sketch022
  Type = 0
FEATURE [Sketcher::SketchObject] Sketch023
  ExternalGeometry = -> [Pocket010]
  MapMode = 5
  Placement = pos=(12.5,-2.96e-14,1.4e-14) rot=(0.57735,0.57735,0.57735;2.0944rad)
  Support = -> [Pocket010]
  sketch-geometry (1):
    g0: Circle CenterX=0 CenterY=8.05 CenterZ=0 NormalX=0 NormalY=0 NormalZ=1 AngleXU=0 Radius=4
  constraints (2):
    c: Radius(g0) = 4
    c: Coincident(g0,g-3)
FEATURE [PartDesign::Pocket] Pocket011
  BaseFeature = -> Pocket010
  Length = 1
  Length2 = 100
  Placement = pos=(0,0,0) rot=(0.57735,0.57735,0.57735;2.0944rad)
  Profile = -> Sketch023
  Type = 0
FEATURE [PartDesign::Mirrored] Mirrored006
  BaseFeature = -> Pocket011
  MirrorPlane = -> YZ_Plane009
  Originals = -> [Pad010]
  Placement = pos=(0,0,0) rot=(0.57735,0.57735,0.57735;2.0944rad)
FEATURE [PartDesign::Mirrored] Mirrored007
  BaseFeature = -> Mirrored006
  MirrorPlane = -> YZ_Plane009
  Originals = -> [Pocket010]
  Placement = pos=(0,0,0) rot=(0.57735,0.57735,0.57735;2.0944rad)
FEATURE [PartDesign::Mirrored] Mirrored008
  BaseFeature = -> Mirrored007
  MirrorPlane = -> YZ_Plane009
  Originals = -> [Pocket011]
  Placement = pos=(0,0,0) rot=(0.57735,0.57735,0.57735;2.0944rad)
FEATURE [Sketcher::SketchObject] Sketch024
  MapMode = 5
  Support = -> [XY_Plane010]
  sketch-geometry (6):
    g0: LineSegment StartX=17.5 StartY=53.2815 StartZ=0 EndX=17.5 EndY=-76.6383 EndZ=0
    g1: LineSegment StartX=17.5 StartY=-76.6383 StartZ=0 EndX=-17.5 EndY=-76.6383 EndZ=0
    g2: LineSegment StartX=-17.5 StartY=-76.6383 StartZ=0 EndX=-17.5 EndY=53.2815 EndZ=0
    g3: LineSegment StartX=-17.5 StartY=53.2815 StartZ=0 EndX=-4.4117 EndY=75.9511 EndZ=0
    g4: LineSegment StartX=-4.4117 StartY=75.9511 StartZ=0 EndX=4.4117 EndY=75.9511 EndZ=0
    g5: LineSegment StartX=4.4117 StartY=75.9511 StartZ=0 EndX=17.5 EndY=53.2815 EndZ=0
  constraints (15):
    c: Coincident(g0,g1)
    c: Coincident(g1,g2)
    c: Vertical(g0)
    c: Vertical(g2)
    c: DistanceX(g1,g1) = 35
    c: Symmetric(g1,g0,g-2)
    c: Coincident(g3,g4)
    c: Coincident(g4,g5)
    c: Coincident(g0,g5)
    c: Coincident(g2,g3)
    c: Horizontal(g0,g2)
    c: Horizontal(g2,g3)
    c: Horizontal(g3,g5)
    c: Symmetric(g4,g3,g-2)
    c: Angle(g4,g5) = 2.0944
FEATURE [PartDesign::Pad] Pad011
  Length = 3
  Length2 = 100
  Profile = -> Sketch024
  Type = 0
FEATURE [Sketcher::SketchObject] Sketch025
  ExternalGeometry = -> [Pad011]
  MapMode = 5
  Placement = pos=(17.5,0,0) rot=(0.57735,0.57735,0.57735;2.0944rad)
  Support = -> [Pad011]
  sketch-geometry (5):
    g0: LineSegment StartX=-20.2073 StartY=3 StartZ=0 EndX=20.2073 EndY=3 EndZ=0
    g1: LineSegment StartX=20.2073 StartY=3 StartZ=0 EndX=10.3923 EndY=-14 EndZ=0
    g2: LineSegment StartX=-10.3923 StartY=-14 StartZ=0 EndX=-20.2073 EndY=3 EndZ=0
    g3: ArcOfCircle CenterX=0 CenterY=-8 CenterZ=0 NormalX=0 NormalY=0 NormalZ=1 AngleXU=0 Radius=12 StartAngle=3.66519 EndAngle=5.75959
    g4: Circle CenterX=0 CenterY=-14 CenterZ=0 NormalX=0 NormalY=0 NormalZ=1 AngleXU=0 Radius=2.5
  constraints (13):
    c: Coincident(g0,g1)
    c: Coincident(g2,g0)
    c: Horizontal(g1,g-3)
    c: Tangent(g2,g3) = 1.5708
    c: Tangent(g1,g3) = 1.5708
    c: DistanceY(g2,g2) = 17
    c: Radius(g3) = 12
    c: PointOnObject(g3,g-2)
    c: Angle(g3) = 2.0944
    c: Symmetric(g0,g0,g-2)
    c: PointOnObject(g4,g-2)
    c: Radius(g4) = 2.5
    c: DistanceY(g4,g0) = 17
FEATURE [PartDesign::Pad] Pad012
  BaseFeature = -> Pad011
  Length = 3
  Length2 = 100
  Profile = -> Sketch025
  Type = 0
FEATURE [Sketcher::SketchObject] Sketch026
  ExternalGeometry = -> [Pad012]
  MapMode = 5
  Placement = pos=(17.5,0,0) rot=(0.57735,-0.57735,-0.57735;2.0944rad)
  Support = -> [Pad012]
  sketch-geometry (4):
    g0: LineSegment StartX=-15.0111 StartY=-6 StartZ=0 EndX=15.0111 EndY=-6 EndZ=0
    g1: LineSegment StartX=-10.3923 StartY=-14 StartZ=0 EndX=-15.0111 EndY=-6 EndZ=0
    g2: LineSegment StartX=15.0111 StartY=-6 StartZ=0 EndX=10.3923 EndY=-14 EndZ=0
    g3: ArcOfCircle CenterX=1.2e-15 CenterY=-8 CenterZ=0 NormalX=0 NormalY=0 NormalZ=1 AngleXU=0 Radius=12 StartAngle=3.66519 EndAngle=5.75959
  constraints (11):
    c: Coincident(g2,g3)
    c: Coincident(g2,g-5)
    c: Coincident(g1,g3)
    c: Coincident(g1,g-6)
    c: Coincident(g0,g1)
    c: Coincident(g0,g2)
    c: PointOnObject(g0,g-6)
    c: Horizontal(g0)
    c: PointOnObject(g0,g-5)
    c: Coincident(g3,g-4)
    c: DistanceY(g-3,g0) = 8
FEATURE [PartDesign::Pocket] Pocket012
  BaseFeature = -> Pad012
  Length = 0.5
  Length2 = 100
  Profile = -> Sketch026
  Type = 0
FEATURE [PartDesign::Mirrored] Mirrored009
  BaseFeature = -> Pocket012
  MirrorPlane = -> YZ_Plane010
  Originals = -> [Pad012]
FEATURE [PartDesign::Mirrored] Mirrored010
  BaseFeature = -> Mirrored009
  MirrorPlane = -> YZ_Plane010
  Originals = -> [Pocket012]
FEATURE [Sketcher::SketchObject] Sketch027
  AttachmentOffset = pos=(0,0,-13) rot=(0,0,1;0rad)
  ExternalGeometry = -> [Mirrored010]
  MapMode = 5
  Placement = pos=(0,13,2.9e-15) rot=(1,0,0;1.5708rad)
  Support = -> [XZ_Plane010]
  sketch-geometry (3):
    g0: LineSegment StartX=-17.5 StartY=-4.4e-15 StartZ=0 EndX=-17.5 EndY=-4.8 EndZ=0
    g1: LineSegment StartX=-17.5 StartY=-4.8 StartZ=0 EndX=-12.7 EndY=-4.4e-15 EndZ=0
    g2: LineSegment StartX=-17.5 StartY=-4.4e-15 StartZ=0 EndX=-12.7 EndY=-4.4e-15 EndZ=0
  constraints (8):
    c: Coincident(g0,g1)
    c: Coincident(g1,g2)
    c: Coincident(g0,g2)
    c: Coincident(g0,g-4)
    c: Vertical(g0)
    c: Horizontal(g2)
    c: Equal(g2,g0)
    c: DistanceY(g0,g0) = 4.8
FEATURE [PartDesign::Pad] Pad013
  BaseFeature = -> Mirrored010
  Length = 3
  Length2 = 100
  Profile = -> Sketch027
  Type = 0
FEATURE [PartDesign::Mirrored] Mirrored011
  MirrorPlane = -> XZ_Plane010
FEATURE [PartDesign::Mirrored] Mirrored012
  MirrorPlane = -> YZ_Plane010
FEATURE [PartDesign::MultiTransform] MultiTransform001
  BaseFeature = -> Pad013
  Originals = -> [Pad013]
  Transformations = -> [Mirrored011,Mirrored012]
FEATURE [Sketcher::SketchObject] Sketch028
  ExternalGeometry = -> [MultiTransform001]
  MapMode = 5
  Placement = pos=(0,0,3) rot=(0,0,1;0rad)
  Support = -> [MultiTransform001]
  sketch-geometry (7):
    g0: Circle CenterX=-7.5 CenterY=30 CenterZ=0 NormalX=0 NormalY=0 NormalZ=1 AngleXU=0 Radius=2
    g1: Circle CenterX=-7.5 CenterY=0 CenterZ=0 NormalX=0 NormalY=0 NormalZ=1 AngleXU=0 Radius=2
    g2: Circle CenterX=-7.5 CenterY=-30 CenterZ=0 NormalX=0 NormalY=0 NormalZ=1 AngleXU=0 Radius=2
    g3: Circle CenterX=-7.5 CenterY=-60 CenterZ=0 NormalX=0 NormalY=0 NormalZ=1 AngleXU=0 Radius=2
    g4: LineSegment [constr] StartX=-7.5 StartY=30 StartZ=0 EndX=-7.5 EndY=0 EndZ=0
    g5: LineSegment [constr] StartX=-7.5 StartY=0 StartZ=0 EndX=-7.5 EndY=-30 EndZ=0
    g6: LineSegment [constr] StartX=-7.5 StartY=-30 StartZ=0 EndX=-7.5 EndY=-60 EndZ=0
  constraints (18):
    c: Equal(g3,g2)
    c: Equal(g2,g1)
    c: Equal(g1,g0)
    c: Vertical(g0,g1)
    c: Vertical(g1,g2)
    c: Vertical(g2,g3)
    c: Radius(g0) = 2
    c: Coincident(g3,g6)
    c: Coincident(g2,g5)
    c: Coincident(g2,g6)
    c: Coincident(g1,g4)
    c: Coincident(g1,g5)
    c: Coincident(g0,g4)
    c: Equal(g4,g5)
    c: Equal(g5,g6)
    c: DistanceY(g3,g0) = 90
    c: PointOnObject(g1,g-1)
    c: DistanceX(g2) = -7.5
FEATURE [PartDesign::Pocket] Pocket013
  BaseFeature = -> MultiTransform001
  Length = 5
  Length2 = 100
  Profile = -> Sketch028
  Type = 0
FEATURE [Sketcher::SketchObject] Sketch029
  ExternalGeometry = -> [Pocket013]
  MapMode = 5
  Placement = pos=(0,0,0) rot=(1,0,0;3.14159rad)
  Support = -> [Pocket013]
  sketch-geometry (8):
    g0: Circle CenterX=-7.5 CenterY=60 CenterZ=0 NormalX=0 NormalY=0 NormalZ=1 AngleXU=0 Radius=2
    g1: Circle CenterX=-7.5 CenterY=30 CenterZ=0 NormalX=0 NormalY=0 NormalZ=1 AngleXU=0 Radius=2
    g2: Circle CenterX=-7.5 CenterY=0 CenterZ=0 NormalX=0 NormalY=0 NormalZ=1 AngleXU=0 Radius=2
    g3: Circle CenterX=-7.5 CenterY=-30 CenterZ=0 NormalX=0 NormalY=0 NormalZ=1 AngleXU=0 Radius=2
    g4: Circle CenterX=-7.5 CenterY=0 CenterZ=0 NormalX=0 NormalY=0 NormalZ=1 AngleXU=0 Radius=3.5
    g5: Circle CenterX=-7.5 CenterY=-30 CenterZ=0 NormalX=0 NormalY=0 NormalZ=1 AngleXU=0 Radius=3.5
    g6: Circle CenterX=-7.5 CenterY=30 CenterZ=0 NormalX=0 NormalY=0 NormalZ=1 AngleXU=0 Radius=3.5
    g7: Circle CenterX=-7.5 CenterY=60 CenterZ=0 NormalX=0 NormalY=0 NormalZ=1 AngleXU=0 Radius=3.5
  constraints (16):
    c: Coincident(g3,g-6)
    c: Coincident(g2,g-5)
    c: Coincident(g1,g-4)
    c: Coincident(g0,g-3)
    c: Equal(g0,g-3)
    c: Equal(g1,g-4)
    c: Equal(g2,g-5)
    c: Equal(g3,g-6)
    c: Coincident(g0,g7)
    c: Coincident(g1,g6)
    c: Coincident(g2,g4)
    c: Coincident(g3,g5)
    c: Equal(g5,g4)
    c: Equal(g4,g6)
    c: Equal(g6,g7)
    c: Radius(g7) = 3.5
FEATURE [PartDesign::Pad] Pad014
  BaseFeature = -> Pocket013
  Length = 1
  Length2 = 100
  Profile = -> Sketch029
  Type = 0
FEATURE [Sketcher::SketchObject] Sketch030
  MapMode = 5
  Placement = pos=(0,0,0) rot=(1,0,0;1.5708rad)
  Support = -> [XZ_Plane011]
  sketch-geometry (4):
    g0: LineSegment StartX=1.5 StartY=0 StartZ=0 EndX=5.38675 EndY=0 EndZ=0
    g1: LineSegment StartX=5.38675 StartY=0 StartZ=0 EndX=2.5 EndY=5 EndZ=0
    g2: LineSegment StartX=2.5 StartY=5 StartZ=0 EndX=1.5 EndY=5 EndZ=0
    g3: LineSegment StartX=1.5 StartY=5 StartZ=0 EndX=1.5 EndY=0 EndZ=0
  constraints (12):
    c: Coincident(g0,g1)
    c: Coincident(g1,g2)
    c: Coincident(g2,g3)
    c: Coincident(g0,g3)
    c: Horizontal(g3,g-1)
    c: Horizontal(g0)
    c: Vertical(g3)
    c: Horizontal(g2)
    c: DistanceX(g0) = 1.5
    c: Angle(g1,g0) = 1.0472
    c: DistanceX(g2,g2) = 1
    c: DistanceY(g3,g3) = 5
FEATURE [PartDesign::Revolution] Revolution
  Angle = 360
  Axis = (0,2e-16,1)
  Base = (0,0,0)
  Placement = pos=(0,0,0) rot=(1,0,0;1.5708rad)
  Profile = -> Sketch030
  ReferenceAxis = -> Sketch030 [V_Axis]
  Reversed = true
FEATURE [PartDesign::Body] Body011  label="spacer"
  Group = -> [Sketch030,Revolution]
  Origin = -> Origin011
  Placement = pos=(-7.5,1,89) rot=(0,0,1;0rad)
  Tip = -> Revolution
FEATURE [PartDesign::FeatureBase] Clone003
  BaseFeature = -> Body011
  Placement = pos=(-7,-9,89) rot=(0,0,1;0rad)
FEATURE [PartDesign::Body] Body012  label="spacer_1"
  BaseFeature = -> Body011
  Group = -> [Clone003]
  Origin = -> Origin012
  Placement = pos=(-0.5,-20,0) rot=(0,0,1;0rad)
  Tip = -> Clone003
FEATURE [PartDesign::FeatureBase] Clone004
  BaseFeature = -> Body011
  Placement = pos=(-7,-9,89) rot=(0,0,1;0rad)
FEATURE [PartDesign::Body] Body013  label="spacer_2"
  BaseFeature = -> Body011
  Group = -> [Clone004]
  Origin = -> Origin013
  Placement = pos=(-0.5,-50,0) rot=(0,0,1;0rad)
  Tip = -> Clone004
FEATURE [PartDesign::FeatureBase] Clone005
  BaseFeature = -> Body011
  Placement = pos=(-7,-9,89) rot=(0,0,1;0rad)
FEATURE [PartDesign::Body] Body014  label="spacer_3"
  BaseFeature = -> Body011
  Group = -> [Clone005]
  Origin = -> Origin014
  Placement = pos=(-0.5,-80,0) rot=(0,0,1;0rad)
  Tip = -> Clone005
FEATURE [Sketcher::SketchObject] Sketch031
  MapMode = 5
  Placement = pos=(0,0,0) rot=(1,0,0;1.5708rad)
  Support = -> [XZ_Plane015]
  sketch-geometry (5):
    g0: LineSegment StartX=3.5 StartY=1.5 StartZ=0 EndX=3.5 EndY=-1.5 EndZ=0
    g1: LineSegment StartX=3.5 StartY=1.5 StartZ=0 EndX=8.25865 EndY=1.5 EndZ=0
    g2: LineSegment StartX=8.25865 StartY=1.5 StartZ=0 EndX=7 EndY=0 EndZ=0
    g3: LineSegment StartX=7 StartY=0 StartZ=0 EndX=8.25865 EndY=-1.5 EndZ=0
    g4: LineSegment StartX=8.25865 StartY=-1.5 StartZ=0 EndX=3.5 EndY=-1.5 EndZ=0
  constraints (15):
    c: Coincident(g1,g2)
    c: Coincident(g2,g3)
    c: Coincident(g3,g4)
    c: Horizontal(g4)
    c: Coincident(g0,g4)
    c: Horizontal(g1)
    c: Angle(g3,g2) = 1.74533
    c: DistanceY(g0,g0) = 3
    c: Equal(g2,g3)
    c: Coincident(g0,g1)
    c: DistanceX(g0) = 3.5
    c: Vertical(g0)
    c: PointOnObject(g2,g-1)
    c: Vertical(g2,g3)
    c: DistanceX(g2) = 7
FEATURE [PartDesign::Revolution] Revolution001
  Angle = 360
  Axis = (0,2e-16,1)
  Base = (0,0,0)
  Placement = pos=(0,0,0) rot=(1,0,0;1.5708rad)
  Profile = -> Sketch031
  ReferenceAxis = -> Sketch031 [V_Axis]
  Reversed = true
FEATURE [Sketcher::SketchObject] Sketch032
  ExternalGeometry = -> [Revolution001]
  MapMode = 5
  Support = -> [XY_Plane015]
  sketch-geometry (10):
    g0: GeomPoint X=3.5 Y=0 Z=0
    g1: GeomPoint X=7 Y=0 Z=0
    g2: GeomPoint X=4.2 Y=0 Z=0
    g3: GeomPoint X=6.3 Y=0 Z=0
    g4: ArcOfCircle CenterX=0 CenterY=0 CenterZ=0 NormalX=0 NormalY=0 NormalZ=1 AngleXU=0 Radius=6.3 StartAngle=6.1029 EndAngle=6.46347
    g5: ArcOfCircle CenterX=0 CenterY=0 CenterZ=0 NormalX=0 NormalY=0 NormalZ=1 AngleXU=0 Radius=4.2 StartAngle=6.1029 EndAngle=6.46347
    g6: LineSegment [constr] StartX=0 StartY=0 StartZ=0 EndX=4.54663 EndY=2.625 EndZ=0
    g7: ArcOfCircle CenterX=5.16491 CenterY=-0.941377 CenterZ=0 NormalX=0 NormalY=0 NormalZ=1 AngleXU=0 Radius=1.05 StartAngle=2.96131 EndAngle=6.1029
    g8: ArcOfCircle CenterX=5.16491 CenterY=0.941377 CenterZ=0 NormalX=0 NormalY=0 NormalZ=1 AngleXU=0 Radius=1.05 StartAngle=0.180285 EndAngle=3.32188
    g9: ArcOfCircle [constr] CenterX=0 CenterY=0 CenterZ=0 NormalX=0 NormalY=0 NormalZ=1 AngleXU=0 Radius=5.25 StartAngle=0.180285 EndAngle=0.38062
  constraints (27):
    c: PointOnObject(g1,g-3)
    c: PointOnObject(g0,g-4)
    c: Horizontal(g0,g1)
    c: Horizontal(g2,g3)
    c: DistanceX(g0,g2) = 0.7
    c: DistanceX(g3,g1) = 0.7
    c: PointOnObject(g2,g5)
    c: PointOnObject(g3,g4)
    c: Coincident(g4,g5)
    c: Coincident(g4,g6)
    c: Symmetric(g5,g5,g-1)
    c: Symmetric(g4,g4,g-1)
    c: Angle(g-1,g6) = 0.523599
    c: Tangent(g4,g8) = -1.5708
    c: Tangent(g5,g7) = 1.5708
    c: Tangent(g4,g7) = -1.5708
    c: PointOnObject(g9,g8)
    c: Tangent(g5,g8) = 1.5708
    c: Coincident(g8,g9)
    c: PointOnObject(g6,g9)
    c: PointOnObject(g2,g-1)
    c: Coincident(g4,g9)
    c: Coincident(g4,g-3)
    c: Coincident(g4,g-1)
    c: Symmetric(g7,g8,g-1)
    c: PointOnObject(g1,g-1)
    c: Distance(g9,g6) = 0.75
FEATURE [PartDesign::Pocket] Pocket014
  BaseFeature = -> Revolution001
  Length = 5
  Length2 = 100
  Midplane = true
  Placement = pos=(0,0,0) rot=(1,0,0;1.5708rad)
  Profile = -> Sketch032
  Type = 1
FEATURE [PartDesign::PolarPattern] PolarPattern
  Angle = 360
  Axis = -> Sketch032 [N_Axis]
  BaseFeature = -> Pocket014
  Occurrences = 6
  Originals = -> [Pocket014]
  Placement = pos=(0,0,0) rot=(1,0,0;1.5708rad)
FEATURE [PartDesign::Body] Body015  label="wheel"
  Group = -> [Sketch031,Revolution001,Sketch032,Pocket014,PolarPattern]
  Origin = -> Origin015
  Placement = pos=(-7.5,1,95.5) rot=(0,0,1;0rad)
  Tip = -> PolarPattern
FEATURE [PartDesign::FeatureBase] Clone006
  BaseFeature = -> Body015
  Placement = pos=(-7.5,1,95.5) rot=(0,0,1;0rad)
FEATURE [PartDesign::Body] Body016  label="wheel_1"
  BaseFeature = -> Body015
  Group = -> [Clone006]
  Origin = -> Origin016
  Placement = pos=(0,-30,0) rot=(0,0,1;0rad)
  Tip = -> Clone006
FEATURE [PartDesign::FeatureBase] Clone007
  BaseFeature = -> Body015
  Placement = pos=(-7.5,1,95.5) rot=(0,0,1;0rad)
FEATURE [PartDesign::Body] Body017  label="wheel_2"
  BaseFeature = -> Body015
  Group = -> [Clone007]
  Origin = -> Origin017
  Placement = pos=(0,-60,0) rot=(0,0,1;0rad)
  Tip = -> Clone007
FEATURE [PartDesign::FeatureBase] Clone008
  BaseFeature = -> Body015
  Placement = pos=(-7.5,1,95.5) rot=(0,0,1;0rad)
FEATURE [PartDesign::Body] Body018  label="wheel_3"
  BaseFeature = -> Body015
  Group = -> [Clone008]
  Origin = -> Origin018
  Placement = pos=(0,-90,0) rot=(0,0,1;0rad)
  Tip = -> Clone008
FEATURE [Sketcher::SketchObject] Sketch033
  MapMode = 5
  Support = -> [XY_Plane019]
  sketch-geometry (25):
    g0: LineSegment StartX=0 StartY=23 StartZ=0 EndX=18.5 EndY=23 EndZ=0
    g1: LineSegment StartX=18.5 StartY=23 StartZ=0 EndX=18.5 EndY=-83 EndZ=0
    g2: LineSegment StartX=18.5 StartY=-83 StartZ=0 EndX=0 EndY=-83 EndZ=0
    g3: LineSegment StartX=0 StartY=23 StartZ=0 EndX=0 EndY=7 EndZ=0
    g4: LineSegment StartX=0 StartY=7 StartZ=0 EndX=8.08898 EndY=7 EndZ=0
    g5: LineSegment StartX=8.08898 StartY=7 StartZ=0 EndX=8.08898 EndY=-7 EndZ=0
    g6: LineSegment StartX=8.08898 StartY=-7 StartZ=0 EndX=0 EndY=-7 EndZ=0
    g7: LineSegment StartX=0 StartY=-7 StartZ=0 EndX=0 EndY=-23 EndZ=0
    g8: LineSegment StartX=0 StartY=-23 StartZ=0 EndX=8.08898 EndY=-23 EndZ=0
    g9: LineSegment StartX=8.08898 StartY=-23 StartZ=0 EndX=8.08898 EndY=-37 EndZ=0
    g10: LineSegment StartX=8.08898 StartY=-37 StartZ=0 EndX=0 EndY=-37 EndZ=0
    g11: LineSegment StartX=0 StartY=-37 StartZ=0 EndX=0 EndY=-53 EndZ=0
    g12: LineSegment StartX=0 StartY=-53 StartZ=0 EndX=8.08898 EndY=-53 EndZ=0
    g13: LineSegment StartX=8.08898 StartY=-53 StartZ=0 EndX=8.08898 EndY=-67 EndZ=0
    g14: LineSegment StartX=8.08898 StartY=-67 StartZ=0 EndX=0 EndY=-67 EndZ=0
    g15: LineSegment StartX=0 StartY=-67 StartZ=0 EndX=0 EndY=-83 EndZ=0
    g16: Circle CenterX=7 CenterY=15 CenterZ=0 NormalX=0 NormalY=0 NormalZ=1 AngleXU=0 Radius=1.2
    g17: Circle CenterX=7 CenterY=-15 CenterZ=0 NormalX=0 NormalY=0 NormalZ=1 AngleXU=0 Radius=1.2
    g18: Circle CenterX=7 CenterY=-45 CenterZ=0 NormalX=0 NormalY=0 NormalZ=1 AngleXU=0 Radius=1.2
    g19: Circle CenterX=7 CenterY=-75 CenterZ=0 NormalX=0 NormalY=0 NormalZ=1 AngleXU=0 Radius=1.2
    g20: LineSegment [constr] StartX=7 StartY=-15 StartZ=0 EndX=7 EndY=15 EndZ=0
    g21: LineSegment [constr] StartX=7 StartY=-15 StartZ=0 EndX=7 EndY=-45 EndZ=0
    g22: LineSegment [constr] StartX=7 StartY=-45 StartZ=0 EndX=7 EndY=-75 EndZ=0
    g23: GeomPoint X=7 Y=-83 Z=0
    g24: GeomPoint X=7 Y=-67 Z=0
  constraints (66):
    c: Coincident(g0,g1)
    c: Coincident(g1,g2)
    c: Horizontal(g0)
    c: Horizontal(g2)
    c: Vertical(g1)
    c: DistanceX(g0) = 18.5
    c: Coincident(g3,g4)
    c: Coincident(g4,g5)
    c: Coincident(g5,g6)
    c: Coincident(g6,g7)
    c: Coincident(g7,g8)
    c: Coincident(g8,g9)
    c: Coincident(g9,g10)
    c: Coincident(g10,g11)
    c: Coincident(g11,g12)
    c: Coincident(g12,g13)
    c: Coincident(g13,g14)
    c: Coincident(g14,g15)
    c: Coincident(g2,g15)
    c: Vertical(g15)
    c: Vertical(g13)
    c: Vertical(g9)
    c: Vertical(g12,g14)
    c: Vertical(g15,g7)
    c: Vertical(g8,g10)
    c: Vertical(g3)
    c: Coincident(g3,g0)
    c: Horizontal(g4)
    c: Horizontal(g12)
    c: Horizontal(g14)
    c: Vertical(g5,g9)
    c: Vertical(g9,g13)
    c: Horizontal(g10)
    c: Horizontal(g8)
    c: Horizontal(g6)
    c: Equal(g15,g11)
    c: Equal(g11,g7)
    c: Equal(g7,g3)
    c: Equal(g5,g9)
    c: Equal(g9,g13)
    c: Vertical(g7,g0)
    c: Vertical(g7)
    c: Vertical(g18,g17)
    c: Equal(g17,g16)
    c: Equal(g16,g19)
    c: Equal(g19,g18)
    c: Radius(g16) = 1.2
    c: DistanceY(g19,g16) = 90
    c: Coincident(g19,g22)
    c: Coincident(g18,g21)
    c: Coincident(g18,g22)
    c: Coincident(g17,g20)
    c: Coincident(g17,g21)
    c: Coincident(g16,g20)
    c: Equal(g20,g21)
    c: Equal(g21,g22)
    c: DistanceY(g5,g5) = 14
    c: Symmetric(g5,g4,g-1)
    c: Vertical(g22)
    c: DistanceX(g2,g19) = 7
    c: Symmetric(g16,g17,g-1)
    c: PointOnObject(g2,g-2)
    c: PointOnObject(g23,g2)
    c: PointOnObject(g24,g14)
    c: Symmetric(g23,g24,g19)
    c: Vertical(g23,g24)
FEATURE [PartDesign::Pad] Pad015
  Length = 3
  Length2 = 100
  Profile = -> Sketch033
  Type = 0
FEATURE [PartDesign::Chamfer] Chamfer002
  Base = -> Pad015 [Edge50,Edge53,Edge56,Edge59]
  BaseFeature = -> Pad015
  Size = 1.5
FEATURE [PartDesign::Body] Body019  label="strightener_component"
  Group = -> [Sketch033,Pad015,Chamfer002]
  Origin = -> Origin019
  Placement = pos=(-1,1,89) rot=(0,0,1;0rad)
  Tip = -> Chamfer002
FEATURE [Sketcher::SketchObject] Sketch034
  MapMode = 5
  Placement = pos=(0,0,3) rot=(0,0,1;0rad)
  Support = -> [Pad014]
  sketch-geometry (8):
    g0: ArcOfCircle CenterX=-5 CenterY=45 CenterZ=0 NormalX=0 NormalY=0 NormalZ=1 AngleXU=0 Radius=2.5 StartAngle=1.5708 EndAngle=4.71239
    g1: ArcOfCircle CenterX=4 CenterY=45 CenterZ=0 NormalX=0 NormalY=0 NormalZ=1 AngleXU=0 Radius=2.5 StartAngle=4.71239 EndAngle=7.85398
    g2: LineSegment StartX=-5 StartY=42.5 StartZ=0 EndX=4 EndY=42.5 EndZ=0
    g3: LineSegment StartX=-5 StartY=47.5 StartZ=0 EndX=4 EndY=47.5 EndZ=0
    g4: ArcOfCircle CenterX=-5 CenterY=-45 CenterZ=0 NormalX=0 NormalY=0 NormalZ=1 AngleXU=0 Radius=2.5 StartAngle=1.5708 EndAngle=4.71239
    g5: ArcOfCircle CenterX=4 CenterY=-45 CenterZ=0 NormalX=0 NormalY=0 NormalZ=1 AngleXU=0 Radius=2.5 StartAngle=4.71239 EndAngle=7.85398
    g6: LineSegment StartX=-5 StartY=-47.5 StartZ=0 EndX=4 EndY=-47.5 EndZ=0
    g7: LineSegment StartX=-5 StartY=-42.5 StartZ=0 EndX=4 EndY=-42.5 EndZ=0
  constraints (20):
    c: Tangent(g0,g3) = 1.5708
    c: Tangent(g0,g2) = -1.5708
    c: Tangent(g2,g1) = -1.5708
    c: Tangent(g3,g1) = 1.5708
    c: Horizontal(g2)
    c: Equal(g0,g1)
    c: Tangent(g4,g7) = 1.5708
    c: Tangent(g4,g6) = -1.5708
    c: Tangent(g6,g5) = -1.5708
    c: Tangent(g7,g5) = 1.5708
    c: Horizontal(g6)
    c: Equal(g4,g5)
    c: Radius(g5) = 2.5
    c: Equal(g1,g5)
    c: Vertical(g4,g0)
    c: Vertical(g5,g1)
    c: DistanceY(g4,g0) = 90
    c: DistanceY(g0) = 45
    c: DistanceX(g0) = -5
    c: DistanceX(g1) = 4
FEATURE [PartDesign::Pocket] Pocket015
  BaseFeature = -> Pad014
  Length = 5
  Length2 = 100
  Profile = -> Sketch034
  Type = 0
FEATURE [Sketcher::SketchObject] Sketch035
  ExternalGeometry = -> [Pocket015]
  MapMode = 5
  Placement = pos=(17.5,0,0) rot=(0.57735,0.57735,0.57735;2.0944rad)
  Support = -> [Pocket015]
  sketch-geometry (4):
    g0: LineSegment StartX=13 StartY=-3.4e-15 StartZ=0 EndX=53 EndY=-3.4e-15 EndZ=0
    g1: LineSegment StartX=51.8453 StartY=-2 StartZ=0 EndX=13 EndY=-2 EndZ=0
    g2: LineSegment StartX=53 StartY=-3.4e-15 StartZ=0 EndX=51.8453 EndY=-2 EndZ=0
    g3: LineSegment StartX=13 StartY=-2 StartZ=0 EndX=13 EndY=-3.6e-15 EndZ=0
  constraints (11):
    c: Horizontal(g1)
    c: Coincident(g1,g2)
    c: DistanceY(g1,g0) = 2
    c: Angle(g2,g1) = 2.0944
    c: Coincident(g0,g2)
    c: Horizontal(g0)
    c: Vertical(g0,g1)
    c: Coincident(g0,g-5)
    c: Coincident(g1,g3)
    c: Coincident(g0,g3)
    c: DistanceX(g0,g0) = 40
FEATURE [PartDesign::Pad] Pad016
  BaseFeature = -> Pocket015
  Length = 2
  Length2 = 100
  Profile = -> Sketch035
  Reversed = true
  Type = 0
FEATURE [PartDesign::Mirrored] Mirrored013
  BaseFeature = -> Pad016
  MirrorPlane = -> YZ_Plane010
  Originals = -> [Pad016]
FEATURE [Sketcher::SketchObject] Sketch036
  MapMode = 5
  Placement = pos=(0,0,0) rot=(1,0,0;1.5708rad)
  Support = -> [XZ_Plane020]
  sketch-geometry (4):
    g0: LineSegment StartX=1.5 StartY=0 StartZ=0 EndX=1.5 EndY=2 EndZ=0
    g1: LineSegment StartX=1.5 StartY=2 StartZ=0 EndX=2.5 EndY=2 EndZ=0
    g2: LineSegment StartX=2.5 StartY=2 StartZ=0 EndX=3.6547 EndY=0 EndZ=0
    g3: LineSegment StartX=3.6547 StartY=0 StartZ=0 EndX=1.5 EndY=0 EndZ=0
  constraints (12):
    c: Coincident(g0,g1)
    c: Coincident(g1,g2)
    c: Coincident(g2,g3)
    c: Coincident(g3,g0)
    c: Vertical(g0)
    c: Horizontal(g3)
    c: Horizontal(g1)
    c: Horizontal(g3,g-1)
    c: DistanceX(g0) = 1.5
    c: Angle(g2,g3) = 1.0472
    c: DistanceX(g1,g1) = 1
    c: DistanceY(g0,g0) = 2
FEATURE [PartDesign::Revolution] Revolution002
  Angle = 360
  Axis = (0,2e-16,1)
  Base = (0,0,0)
  Placement = pos=(0,0,0) rot=(1,0,0;1.5708rad)
  Profile = -> Sketch036
  ReferenceAxis = -> Sketch036 [V_Axis]
  Reversed = true
FEATURE [PartDesign::Body] Body020  label="lower_spacer"
  Group = -> [Sketch036,Revolution002]
  Origin = -> Origin020
  Placement = pos=(6,16,92) rot=(0,0,1;0rad)
  Tip = -> Revolution002
FEATURE [PartDesign::FeatureBase] Clone009
  BaseFeature = -> Body020
FEATURE [PartDesign::Body] Body021  label="lower_spacer_1"
  BaseFeature = -> Body020
  Group = -> [Clone009]
  Origin = -> Origin021
  Placement = pos=(6,-14,92) rot=(0,0,1;0rad)
  Tip = -> Clone009
FEATURE [PartDesign::FeatureBase] Clone010
  BaseFeature = -> Body020
FEATURE [PartDesign::Body] Body022  label="lower_spacer_2"
  BaseFeature = -> Body020
  Group = -> [Clone010]
  Origin = -> Origin022
  Placement = pos=(6,-44,92) rot=(0,0,1;0rad)
  Tip = -> Clone010
FEATURE [PartDesign::FeatureBase] Clone011
  BaseFeature = -> Body020
FEATURE [PartDesign::Body] Body023  label="lower_spacer_3"
  BaseFeature = -> Body020
  Group = -> [Clone011]
  Origin = -> Origin023
  Placement = pos=(6,-74,92) rot=(0,0,1;0rad)
  Tip = -> Clone011
FEATURE [PartDesign::FeatureBase] Clone012
  BaseFeature = -> Body015
  Placement = pos=(-7.5,1,95.5) rot=(0,0,1;0rad)
FEATURE [PartDesign::Body] Body024  label="wheel_4"
  BaseFeature = -> Body015
  Group = -> [Clone012]
  Origin = -> Origin024
  Placement = pos=(13.5,15,0) rot=(0,0,1;0rad)
  Tip = -> Clone012
FEATURE [PartDesign::FeatureBase] Clone013
  BaseFeature = -> Body015
  Placement = pos=(-7.5,1,95.5) rot=(0,0,1;0rad)
FEATURE [PartDesign::Body] Body025  label="wheel_5"
  BaseFeature = -> Body015
  Group = -> [Clone013]
  Origin = -> Origin025
  Placement = pos=(13.5,-15,0) rot=(0,0,1;0rad)
  Tip = -> Clone013
FEATURE [PartDesign::FeatureBase] Clone014
  BaseFeature = -> Body015
  Placement = pos=(-7.5,1,95.5) rot=(0,0,1;0rad)
FEATURE [PartDesign::Body] Body026  label="wheel_6"
  BaseFeature = -> Body015
  Group = -> [Clone014]
  Origin = -> Origin026
  Placement = pos=(13.5,-45,0) rot=(0,0,1;0rad)
  Tip = -> Clone014
FEATURE [PartDesign::FeatureBase] Clone015
  BaseFeature = -> Body015
  Placement = pos=(-7.5,1,95.5) rot=(0,0,1;0rad)
FEATURE [PartDesign::Body] Body027  label="wheel_7"
  BaseFeature = -> Body015
  Group = -> [Clone015]
  Origin = -> Origin027
  Placement = pos=(13.5,-75,0) rot=(0,0,1;0rad)
  Tip = -> Clone015
FEATURE [Sketcher::SketchObject] Sketch037
  MapMode = 5
  Placement = pos=(0,0,0) rot=(1,0,0;1.5708rad)
  Support = -> [XZ_Plane028]
  sketch-geometry (13):
    g0: LineSegment StartX=2 StartY=0 StartZ=0 EndX=2 EndY=10 EndZ=0
    g1: LineSegment StartX=2 StartY=0 StartZ=0 EndX=3 EndY=0 EndZ=0
    g2-g7: Circle [constr] x6 (B-spline internal-alignment scaffolding for g8; pole/knot coordinates omitted)
    g8: BSplineCurve PolesCount=6 KnotsCount=4 Degree=3 IsPeriodic=0
    g9-g12: GeomPoint [constr] x4 (B-spline internal-alignment scaffolding for g8; pole/knot coordinates omitted)
  constraints (13):
    c: DistanceX(g0) = 2
    c: Vertical(g0)
    c: Coincident(g0,g1)
    c: Horizontal(g1,g-1)
    c: Horizontal(g1)
    c: DistanceY(g0,g0) = 10
    c: Radius(g2) = 0.4
    c: Equal(g2, g3-g7) x5
    c: InternalAlignment(g2-g7 -> g8) x6
    c: InternalAlignment(g9-g12 -> g8) x4
    c: Coincident(g8,g0)
    c: Coincident(g8,g1)
    c: DistanceX(g1) = 3
FEATURE [PartDesign::Revolution] Revolution003
  Angle = 360
  Axis = (0,2e-16,1)
  Base = (0,0,0)
  Placement = pos=(0,0,0) rot=(1,0,0;1.5708rad)
  Profile = -> Sketch037
  ReferenceAxis = -> Sketch037 [V_Axis]
  Reversed = true
FEATURE [Sketcher::SketchObject] Sketch038
  MapMode = 5
  Support = -> [XY_Plane028]
  sketch-geometry (17):
    g0-g7: Circle [constr] x8 (B-spline internal-alignment scaffolding for g8; pole/knot coordinates omitted)
    g8: BSplineCurve PolesCount=8 KnotsCount=6 Degree=3 IsPeriodic=0
    g9-g14: GeomPoint [constr] x6 (B-spline internal-alignment scaffolding for g8; pole/knot coordinates omitted)
    g15: LineSegment StartX=7.08786 StartY=13.8751 StartZ=0 EndX=20.1808 EndY=4.79439 EndZ=0
    g16: LineSegment StartX=20.1808 StartY=4.79439 StartZ=0 EndX=7.08786 EndY=-13.8751 EndZ=0
  constraints (11):
    c: Radius(g0) = 0.7
    c: Equal(g0, g1-g7) x7
    c: InternalAlignment(g0-g7 -> g8) x8
    c: InternalAlignment(g9-g14 -> g8) x6
    c: Symmetric(g8,g8,g-1)
    c: Symmetric(g6,g1,g-1)
    c: Symmetric(g5,g2,g-1)
    c: Symmetric(g3,g4,g-1)
    c: Coincident(g15,g16)
    c: Coincident(g15,g8)
    c: Coincident(g16,g8)
FEATURE [PartDesign::Pocket] Pocket016
  BaseFeature = -> Revolution003
  Length = 5
  Length2 = 100
  Placement = pos=(0,0,0) rot=(1,0,0;1.5708rad)
  Profile = -> Sketch038
  Reversed = true
  Type = 1
FEATURE [PartDesign::PolarPattern] PolarPattern001
  Angle = 360
  Axis = -> Sketch038 [N_Axis]
  BaseFeature = -> Pocket016
  Occurrences = 4
  Originals = -> [Pocket016]
  Placement = pos=(0,0,0) rot=(1,0,0;1.5708rad)
FEATURE [PartDesign::Body] Body028  label="knob"
  Group = -> [Sketch037,Revolution003,Sketch038,Pocket016,PolarPattern001]
  Origin = -> Origin028
  Placement = pos=(-259.5,-24,48.5) rot=(0,-1,0;1.5708rad)
  Tip = -> PolarPattern001
FEATURE [PartDesign::FeatureBase] Clone016
  BaseFeature = -> Body028
  Placement = pos=(6,16,97) rot=(0,0,1;0rad)
FEATURE [PartDesign::Body] Body029  label="knob_1"
  BaseFeature = -> Body028
  Group = -> [Clone016]
  Origin = -> Origin029
  Placement = pos=(0,-90,0) rot=(0,0,1;0rad)
  Tip = -> Clone016
FEATURE [Sketcher::SketchObject] Sketch039
  ExternalGeometry = -> [Mirrored013]
  MapMode = 5
  Placement = pos=(0,0,0) rot=(1,0,0;3.14159rad)
  Support = -> [Mirrored013]
  sketch-geometry (20):
    g0: LineSegment StartX=-5 StartY=51 StartZ=0 EndX=4 EndY=51 EndZ=0
    g1: LineSegment StartX=4 StartY=51 StartZ=0 EndX=4 EndY=50 EndZ=0
    g2: LineSegment StartX=4 StartY=50 StartZ=0 EndX=-5 EndY=50 EndZ=0
    g3: LineSegment StartX=-5 StartY=50 StartZ=0 EndX=-5 EndY=51 EndZ=0
    g4: LineSegment StartX=-5 StartY=40 StartZ=0 EndX=4 EndY=40 EndZ=0
    g5: LineSegment StartX=4 StartY=40 StartZ=0 EndX=4 EndY=39 EndZ=0
    g6: LineSegment StartX=4 StartY=39 StartZ=0 EndX=-5 EndY=39 EndZ=0
    g7: LineSegment StartX=-5 StartY=39 StartZ=0 EndX=-5 EndY=40 EndZ=0
    g8: LineSegment StartX=-5 StartY=-39 StartZ=0 EndX=4 EndY=-39 EndZ=0
    g9: LineSegment StartX=4 StartY=-39 StartZ=0 EndX=4 EndY=-40 EndZ=0
    g10: LineSegment StartX=4 StartY=-40 StartZ=0 EndX=-5 EndY=-40 EndZ=0
    g11: LineSegment StartX=-5 StartY=-40 StartZ=0 EndX=-5 EndY=-39 EndZ=0
    g12: LineSegment StartX=-5 StartY=-50 StartZ=0 EndX=4 EndY=-50 EndZ=0
    g13: LineSegment StartX=4 StartY=-50 StartZ=0 EndX=4 EndY=-51 EndZ=0
    g14: LineSegment StartX=4 StartY=-51 StartZ=0 EndX=-5 EndY=-51 EndZ=0
    g15: LineSegment StartX=-5 StartY=-51 StartZ=0 EndX=-5 EndY=-50 EndZ=0
    g16: LineSegment [constr] StartX=-5 StartY=47.5 StartZ=0 EndX=-5 EndY=50 EndZ=0
    g17: LineSegment [constr] StartX=-5 StartY=40 StartZ=0 EndX=-5 EndY=42.5 EndZ=0
    g18: LineSegment [constr] StartX=-5 StartY=-42.5 StartZ=0 EndX=-5 EndY=-40 EndZ=0
    g19: LineSegment [constr] StartX=-5 StartY=-50 StartZ=0 EndX=-5 EndY=-47.5 EndZ=0
  constraints (56):
    c: Coincident(g0,g1)
    c: Coincident(g1,g2)
    c: Coincident(g2,g3)
    c: Coincident(g3,g0)
    c: Horizontal(g0)
    c: Horizontal(g2)
    c: Vertical(g1)
    c: Vertical(g3)
    c: DistanceY(g1,g1) = 1
    c: Vertical(g3,g-6)
    c: Vertical(g2,g-6)
    c: Coincident(g4,g5)
    c: Coincident(g5,g6)
    c: Coincident(g6,g7)
    c: Coincident(g7,g4)
    c: Horizontal(g4)
    c: Horizontal(g6)
    c: Vertical(g5)
    c: Vertical(g7)
    c: Vertical(g4,g-5)
    c: Vertical(g4,g-5)
    c: Equal(g7,g3)
    c: Coincident(g8,g9)
    c: Coincident(g9,g10)
    c: Coincident(g10,g11)
    c: Coincident(g11,g8)
    c: Horizontal(g8)
    c: Horizontal(g10)
    c: Vertical(g9)
    c: Vertical(g11)
    c: Coincident(g12,g13)
    c: Coincident(g13,g14)
    c: Coincident(g14,g15)
    c: Coincident(g15,g12)
    c: Horizontal(g12)
    c: Horizontal(g14)
    c: Vertical(g13)
    c: Vertical(g15)
    c: Vertical(g12,g-4)
    c: Vertical(g12,g-4)
    c: Vertical(g-3,g10)
    c: Vertical(g9,g-3)
    c: Equal(g11,g15)
    c: Equal(g15,g3)
    c: Coincident(g12,g19)
    c: Coincident(g19,g-4)
    c: Coincident(g18,g-3)
    c: Coincident(g10,g18)
    c: Coincident(g17,g-5)
    c: Coincident(g4,g17)
    c: Coincident(g16,g-6)
    c: Coincident(g2,g16)
    c: Equal(g16,g17)
    c: Equal(g17,g18)
    c: Equal(g18,g19)
    c: DistanceY(g16,g16) = 2.5
FEATURE [PartDesign::Pad] Pad017
  BaseFeature = -> Mirrored013
  Length = 1
  Length2 = 100
  Profile = -> Sketch039
  Type = 0
FEATURE [Sketcher::SketchObject] Sketch040
  MapMode = 5
  Support = -> [XY_Plane030]
  sketch-geometry (11):
    g0: LineSegment StartX=-4.5 StartY=4.5 StartZ=0 EndX=4.5 EndY=4.5 EndZ=0
    g1: LineSegment StartX=4.5 StartY=4.5 StartZ=0 EndX=4.5 EndY=-4.5 EndZ=0
    g2: LineSegment StartX=4.5 StartY=-4.5 StartZ=0 EndX=-4.5 EndY=-4.5 EndZ=0
    g3: LineSegment StartX=-4.5 StartY=-4.5 StartZ=0 EndX=-4.5 EndY=4.5 EndZ=0
    g4: LineSegment StartX=2.75 StartY=-1.58771 StartZ=0 EndX=2.75 EndY=1.58771 EndZ=0
    g5: LineSegment StartX=2.75 StartY=1.58771 StartZ=0 EndX=3.1e-15 EndY=3.17543 EndZ=0
    g6: LineSegment StartX=3.1e-15 StartY=3.17543 StartZ=0 EndX=-2.75 EndY=1.58771 EndZ=0
    g7: LineSegment StartX=-2.75 StartY=1.58771 StartZ=0 EndX=-2.75 EndY=-1.58771 EndZ=0
    g8: LineSegment StartX=-2.75 StartY=-1.58771 StartZ=0 EndX=2.2e-15 EndY=-3.17543 EndZ=0
    g9: LineSegment StartX=2.2e-15 StartY=-3.17543 StartZ=0 EndX=2.75 EndY=-1.58771 EndZ=0
    g10: Circle [constr] CenterX=0 CenterY=0 CenterZ=0 NormalX=0 NormalY=0 NormalZ=1 AngleXU=0 Radius=3.17543
  constraints (27):
    c: Coincident(g0,g1)
    c: Coincident(g1,g2)
    c: Coincident(g2,g3)
    c: Coincident(g3,g0)
    c: Horizontal(g0)
    c: Horizontal(g2)
    c: Vertical(g1)
    c: Vertical(g3)
    c: Symmetric(g1,g0,g-1)
    c: Coincident(g4,g5)
    c: Coincident(g5,g6)
    c: Coincident(g6,g7)
    c: Coincident(g7,g8)
    c: Coincident(g8,g9)
    c: Coincident(g9,g4)
    c: Equal(g4, g5-g9) x5
    c: PointOnObject(g4,g10)
    c: PointOnObject(g5,g10)
    c: PointOnObject(g6,g10)
    c: PointOnObject(g7,g10)
    c: PointOnObject(g8,g10)
    c: PointOnObject(g9,g10)
    c: Vertical(g4)
    c: DistanceX(g7,g4) = 5.5
    c: Coincident(g10,g-1)
    c: DistanceX(g2,g2) = 9
    c: Equal(g2,g3)
FEATURE [PartDesign::Pad] Pad018
  Length = 2
  Length2 = 100
  Profile = -> Sketch040
  Type = 0
FEATURE [Sketcher::SketchObject] Sketch041
  MapMode = 5
  Placement = pos=(0,0,2) rot=(0,0,1;0rad)
  Support = -> [Pad018]
  sketch-geometry (5):
    g0: LineSegment StartX=-4.5 StartY=4.5 StartZ=0 EndX=4.5 EndY=4.5 EndZ=0
    g1: LineSegment StartX=4.5 StartY=4.5 StartZ=0 EndX=4.5 EndY=-4.5 EndZ=0
    g2: LineSegment StartX=4.5 StartY=-4.5 StartZ=0 EndX=-4.5 EndY=-4.5 EndZ=0
    g3: LineSegment StartX=-4.5 StartY=-4.5 StartZ=0 EndX=-4.5 EndY=4.5 EndZ=0
    g4: Circle CenterX=0 CenterY=0 CenterZ=0 NormalX=0 NormalY=0 NormalZ=1 AngleXU=0 Radius=1.5
  constraints (13):
    c: Coincident(g0,g1)
    c: Coincident(g1,g2)
    c: Coincident(g2,g3)
    c: Coincident(g3,g0)
    c: Horizontal(g0)
    c: Horizontal(g2)
    c: Vertical(g1)
    c: Vertical(g3)
    c: Symmetric(g1,g0,g-1)
    c: Equal(g2,g3)
    c: DistanceX(g2,g2) = 9
    c: Coincident(g4,g-1)
    c: Radius(g4) = 1.5
FEATURE [PartDesign::Pad] Pad019
  BaseFeature = -> Pad018
  Length = 2
  Length2 = 100
  Profile = -> Sketch041
  Type = 0
FEATURE [PartDesign::Body] Body030  label="nut_holder"
  Group = -> [Sketch040,Pad018,Sketch041,Pad019]
  Origin = -> Origin030
  Placement = pos=(0,16,82) rot=(0,0,1;0rad)
  Tip = -> Pad019
FEATURE [PartDesign::FeatureBase] Clone017
  BaseFeature = -> Body030
  Placement = pos=(0,16,82) rot=(0,0,1;0rad)
FEATURE [PartDesign::Body] Body031  label="nut_holder_1"
  BaseFeature = -> Body030
  Group = -> [Clone017]
  Origin = -> Origin031
  Placement = pos=(0,-90,0) rot=(0,0,1;0rad)
  Tip = -> Clone017
FEATURE [Sketcher::SketchObject] Sketch042
  ExternalGeometry = -> [Pad017]
  MapMode = 5
  Placement = pos=(-17.5,0,0) rot=(0.57735,-0.57735,-0.57735;2.0944rad)
  Support = -> [Pad017]
  sketch-geometry (4):
    g0: LineSegment StartX=56.6383 StartY=3 StartZ=0 EndX=76.6383 EndY=3 EndZ=0
    g1: LineSegment StartX=76.6383 StartY=3 StartZ=0 EndX=76.6383 EndY=0 EndZ=0
    g2: LineSegment StartX=76.6383 StartY=0 StartZ=0 EndX=56.6383 EndY=0 EndZ=0
    g3: LineSegment StartX=56.6383 StartY=0 StartZ=0 EndX=56.6383 EndY=3 EndZ=0
  constraints (10):
    c: Coincident(g0,g1)
    c: Coincident(g1,g2)
    c: Coincident(g2,g3)
    c: Coincident(g3,g0)
    c: Horizontal(g0)
    c: Horizontal(g2)
    c: Vertical(g3)
    c: Coincident(g1,g-3)
    c: Coincident(g0,g-4)
    c: DistanceX(g0,g0) = 20
FEATURE [PartDesign::Pad] Pad020
  BaseFeature = -> Pad017
  Length = 3
  Length2 = 100
  Profile = -> Sketch042
  Type = 0
FEATURE [Sketcher::SketchObject] Sketch043
  ExternalGeometry = -> [Pad020]
  MapMode = 5
  Placement = pos=(0,0,3) rot=(0,0,1;0rad)
  Support = -> [Pad020]
  sketch-geometry (4):
    g0: LineSegment StartX=-18.5 StartY=-59.6383 StartZ=0 EndX=-16.9 EndY=-59.6383 EndZ=0
    g1: LineSegment StartX=-16.9 StartY=-59.6383 StartZ=0 EndX=-16.9 EndY=-73.6383 EndZ=0
    g2: LineSegment StartX=-16.9 StartY=-73.6383 StartZ=0 EndX=-18.5 EndY=-73.6383 EndZ=0
    g3: LineSegment StartX=-18.5 StartY=-73.6383 StartZ=0 EndX=-18.5 EndY=-59.6383 EndZ=0
  constraints (12):
    c: Coincident(g0,g1)
    c: Coincident(g1,g2)
    c: Coincident(g2,g3)
    c: Coincident(g3,g0)
    c: Horizontal(g0)
    c: Horizontal(g2)
    c: Vertical(g1)
    c: Vertical(g3)
    c: DistanceX(g2,g2) = 1.6
    c: DistanceX(g-4,g2) = 2
    c: DistanceY(g-4,g2) = 3
    c: DistanceY(g0,g-4) = 3
FEATURE [PartDesign::Pocket] Pocket017
  BaseFeature = -> Pad020
  Length = 5
  Length2 = 100
  Profile = -> Sketch043
  Type = 1
FEATURE [Sketcher::SketchObject] Sketch044
  MapMode = 5
  Placement = pos=(0,0,0) rot=(0.57735,0.57735,0.57735;2.0944rad)
  Support = -> [YZ_Plane032]
  sketch-geometry (28):
    g0: LineSegment StartX=-4.5 StartY=3 StartZ=0 EndX=-4.5 EndY=-1.07735 EndZ=0
    g1: LineSegment StartX=-7 StartY=-1.07735 StartZ=0 EndX=-8 EndY=-0.5 EndZ=0
    g2: LineSegment StartX=-8 StartY=-0.5 StartZ=0 EndX=-8 EndY=0 EndZ=0
    g3: LineSegment StartX=-8 StartY=0 StartZ=0 EndX=-7 EndY=0 EndZ=0
    g4: LineSegment StartX=-5 StartY=13.5 StartZ=0 EndX=5 EndY=13.5 EndZ=0
    g5: LineSegment StartX=7 StartY=0 StartZ=0 EndX=8 EndY=0 EndZ=0
    g6: LineSegment StartX=8 StartY=0 StartZ=0 EndX=8 EndY=-0.5 EndZ=0
    g7: LineSegment StartX=8 StartY=-0.5 StartZ=0 EndX=7 EndY=-1.07735 EndZ=0
    g8: LineSegment StartX=4.5 StartY=-1.07735 StartZ=0 EndX=4.5 EndY=3 EndZ=0
    g9: LineSegment StartX=4.5 StartY=3 StartZ=0 EndX=3.5 EndY=3 EndZ=0
    g10: LineSegment StartX=3.5 StartY=3 StartZ=0 EndX=3.5 EndY=0 EndZ=0
    g11: LineSegment StartX=3.5 StartY=0 StartZ=0 EndX=-3.5 EndY=0 EndZ=0
    g12: LineSegment StartX=-3.5 StartY=0 StartZ=0 EndX=-3.5 EndY=3 EndZ=0
    g13: LineSegment StartX=-3.5 StartY=3 StartZ=0 EndX=-4.5 EndY=3 EndZ=0
    g14: ArcOfCircle CenterX=-5 CenterY=9.5 CenterZ=0 NormalX=0 NormalY=0 NormalZ=1 AngleXU=0 Radius=1 StartAngle=1.5708 EndAngle=4.71239
    g15: ArcOfCircle CenterX=5 CenterY=9.5 CenterZ=0 NormalX=0 NormalY=0 NormalZ=1 AngleXU=0 Radius=1 StartAngle=4.71239 EndAngle=7.85398
    g16: LineSegment StartX=-5 StartY=8.5 StartZ=0 EndX=5 EndY=8.5 EndZ=0
    g17: LineSegment StartX=-5 StartY=10.5 StartZ=0 EndX=5 EndY=10.5 EndZ=0
    g18: ArcOfCircle CenterX=-5 CenterY=9.5 CenterZ=0 NormalX=0 NormalY=0 NormalZ=1 AngleXU=0 Radius=4 StartAngle=1.5708 EndAngle=3.14159
    g19: ArcOfCircle CenterX=5 CenterY=9.5 CenterZ=0 NormalX=0 NormalY=0 NormalZ=1 AngleXU=0 Radius=4 StartAngle=0 EndAngle=1.5708
    g20: LineSegment StartX=-9 StartY=9.5 StartZ=0 EndX=-9 EndY=3.1 EndZ=0
    g21: LineSegment StartX=-9 StartY=3.1 StartZ=0 EndX=-7 EndY=3.1 EndZ=0
    g22: LineSegment StartX=-7 StartY=3.1 StartZ=0 EndX=-7 EndY=0 EndZ=0
    g23: LineSegment StartX=9 StartY=9.5 StartZ=0 EndX=9 EndY=3.1 EndZ=0
    g24: LineSegment StartX=9 StartY=3.1 StartZ=0 EndX=7 EndY=3.1 EndZ=0
    g25: LineSegment StartX=7 StartY=3.1 StartZ=0 EndX=7 EndY=0 EndZ=0
    g26: LineSegment StartX=-7 StartY=-1.07735 StartZ=0 EndX=-4.5 EndY=-1.07735 EndZ=0
    g27: LineSegment StartX=4.5 StartY=-1.07735 StartZ=0 EndX=7 EndY=-1.07735 EndZ=0
  constraints (77):
    c: Coincident(g1,g2)
    c: Coincident(g2,g3)
    c: Coincident(g5,g6)
    c: Coincident(g6,g7)
    c: Coincident(g8,g9)
    c: Coincident(g9,g10)
    c: Coincident(g10,g11)
    c: Coincident(g11,g12)
    c: Coincident(g12,g13)
    c: Coincident(g13,g0)
    c: Tangent(g14,g17) = 1.5708
    c: Tangent(g14,g16) = -1.5708
    c: Tangent(g16,g15) = -1.5708
    c: Tangent(g17,g15) = 1.5708
    c: Horizontal(g16)
    c: Horizontal(g4)
    c: Vertical(g8)
    c: Vertical(g10)
    c: Vertical(g12)
    c: Horizontal(g13)
    c: Horizontal(g9)
    c: Horizontal(g9,g12)
    c: Vertical(g2)
    c: Horizontal(g3)
    c: Horizontal(g5,g3)
    c: Horizontal(g5)
    c: Equal(g6,g2)
    c: Equal(g7,g1)
    c: Vertical(g0)
    c: Equal(g8,g0)
    c: Equal(g3,g5)
    c: Vertical(g6)
    c: DistanceX(g3,g3) = 1
    c: Angle(g0,g1) = 1.0472
    c: Equal(g13,g9)
    c: DistanceX(g13,g13) = 1
    c: DistanceX(g3,g0) = 2.5
    c: Horizontal(g3,g11)
    c: Symmetric(g11,g10,g-2)
    c: Symmetric(g14,g15,g-2)
    c: DistanceY(g14) = 9.5
    c: Horizontal(g11,g-1)
    c: DistanceY(g12,g12) = 3
    c: DistanceX(g3,g5) = 14
    c: DistanceY(g14,g14) = 2
    c: DistanceX(g14,g15) = 10
    c: Tangent(g4,g18) = 1.5708
    c: Tangent(g4,g19) = 1.5708
    c: Equal(g19,g18)
    c: Coincident(g14,g18)
    c: Coincident(g20,g21)
    c: Coincident(g21,g22)
    c: Coincident(g23,g24)
    c: Coincident(g24,g25)
    c: Vertical(g23)
    c: Vertical(g20)
    c: Vertical(g22)
    c: Vertical(g25)
    c: Horizontal(g24)
    c: Horizontal(g21)
    c: Horizontal(g21,g24)
    c: Coincident(g3,g22)
    c: Coincident(g5,g25)
    c: DistanceX(g21,g21) = 2
    c: Equal(g21,g24)
    c: DistanceY(g22,g22) = 3.1
    c: Tangent(g18,g20) = -1.5708
    c: Tangent(g19,g23) = 1.5708
    c: Horizontal(g27)
    c: Horizontal(g26)
    c: Coincident(g1,g26)
    c: Coincident(g7,g27)
    c: Coincident(g8,g27)
    c: Coincident(g0,g26)
    c: Equal(g27,g26)
    c: DistanceX(g26,g26) = 2.5
    c: DistanceY(g2,g2) = 0.5
FEATURE [PartDesign::Pad] Pad021
  Length = 1.6
  Length2 = 100
  Placement = pos=(0,0,0) rot=(0.57735,0.57735,0.57735;2.0944rad)
  Profile = -> Sketch044
  Type = 0
FEATURE [PartDesign::Body] Body032  label="wire_gate"
  Group = -> [Sketch044,Pad021]
  Origin = -> Origin032
  Placement = pos=(-18.5,-96.5,86) rot=(0,0,1;0rad)
  Tip = -> Pad021
FEATURE [Sketcher::SketchObject] Sketch045
  ExternalGeometry = -> [Mirrored008]
  MapMode = 5
  Placement = pos=(17.5,-2.77e-14,1.91e-14) rot=(0.57735,0.57735,0.57735;2.0944rad)
  Support = -> [Mirrored008]
  sketch-geometry (8):
    g0: LineSegment StartX=3.35 StartY=3.68795 StartZ=0 EndX=3.35 EndY=-21.3121 EndZ=0
    g1: LineSegment StartX=3.35 StartY=-21.3121 StartZ=0 EndX=0.35 EndY=-21.3121 EndZ=0
    g2: LineSegment StartX=0.35 StartY=-21.3121 StartZ=0 EndX=0.35 EndY=0 EndZ=0
    g3: LineSegment StartX=-0.35 StartY=0 StartZ=0 EndX=-0.35 EndY=-21.3121 EndZ=0
    g4: LineSegment StartX=-0.35 StartY=-21.3121 StartZ=0 EndX=-3.35 EndY=-21.3121 EndZ=0
    g5: LineSegment StartX=-3.35 StartY=-21.3121 StartZ=0 EndX=-3.35 EndY=3.68795 EndZ=0
    g6: LineSegment StartX=-0.35 StartY=0 StartZ=0 EndX=0.35 EndY=0 EndZ=0
    g7: ArcOfCircle CenterX=-7.3e-15 CenterY=8.05 CenterZ=0 NormalX=0 NormalY=0 NormalZ=1 AngleXU=0 Radius=5.5 StartAngle=4.05748 EndAngle=5.3673
  constraints (23):
    c: Coincident(g0,g1)
    c: Horizontal(g1)
    c: Vertical(g0)
    c: Vertical(g2)
    c: Coincident(g4,g5)
    c: Horizontal(g4)
    c: Vertical(g3)
    c: Vertical(g5)
    c: Horizontal(g2,g3)
    c: Coincident(g3,g4)
    c: Coincident(g2,g1)
    c: Coincident(g3,g6)
    c: Coincident(g2,g6)
    c: Symmetric(g2,g3,g-2)
    c: Equal(g4,g1)
    c: DistanceX(g4,g4) = 3
    c: DistanceX(g3,g1) = 0.7
    c: PointOnObject(g2,g-1)
    c: DistanceY(g0,g0) = 25
    c: Coincident(g0,g7)
    c: Coincident(g5,g7)
    c: PointOnObject(g5,g-4)
    c: Coincident(g7,g-4)
FEATURE [PartDesign::Pad] Pad022
  BaseFeature = -> Mirrored008
  Length = 13
  Length2 = 100
  Placement = pos=(0,0,0) rot=(0.57735,0.57735,0.57735;2.0944rad)
  Profile = -> Sketch045
  Reversed = true
  Type = 0
FEATURE [Sketcher::SketchObject] Sketch046
  ExternalGeometry = -> [Pad022]
  MapMode = 5
  Placement = pos=(17.5,-2.77e-14,1.91e-14) rot=(0.57735,0.57735,0.57735;2.0944rad)
  Support = -> [Pad022]
  sketch-geometry (6):
    g0: LineSegment StartX=8.35 StartY=2.05 StartZ=0 EndX=3.35 EndY=-2.95 EndZ=0
    g1: LineSegment StartX=3.35 StartY=-2.95 StartZ=0 EndX=3.35 EndY=2.05 EndZ=0
    g2: LineSegment StartX=3.35 StartY=2.05 StartZ=0 EndX=8.35 EndY=2.05 EndZ=0
    g3: LineSegment StartX=-8.35 StartY=2.05 StartZ=0 EndX=-3.35 EndY=-2.95 EndZ=0
    g4: LineSegment StartX=-3.35 StartY=-2.95 StartZ=0 EndX=-3.35 EndY=2.05 EndZ=0
    g5: LineSegment StartX=-3.35 StartY=2.05 StartZ=0 EndX=-8.35 EndY=2.05 EndZ=0
  constraints (17):
    c: Coincident(g0,g1)
    c: Coincident(g1,g2)
    c: Coincident(g0,g2)
    c: Horizontal(g2)
    c: Vertical(g1)
    c: Vertical(g2,g-4)
    c: Horizontal(g2,g-3)
    c: Equal(g1,g2)
    c: Coincident(g3,g4)
    c: Coincident(g4,g5)
    c: Coincident(g3,g5)
    c: Horizontal(g5)
    c: Equal(g4,g5)
    c: Symmetric(g3,g0,g-2)
    c: Symmetric(g1,g4,g-2)
    c: Symmetric(g0,g3,g-2)
    c: DistanceY(g1,g1) = 5
FEATURE [PartDesign::Pad] Pad023
  BaseFeature = -> Pad022
  Length = 2
  Length2 = 100
  Placement = pos=(0,0,0) rot=(0.57735,0.57735,0.57735;2.0944rad)
  Profile = -> Sketch046
  Reversed = true
  Type = 0
FEATURE [Sketcher::SketchObject] Sketch047
  ExternalGeometry = -> [Pad022]
  MapMode = 5
  Placement = pos=(2.49e-14,0,-21.3121) rot=(0.707107,0.707107,0;3.14159rad)
  Support = -> [Pad022]
  sketch-geometry (4):
    g0: ArcOfCircle CenterX=0.45 CenterY=5.1 CenterZ=0 NormalX=0 NormalY=0 NormalZ=1 AngleXU=0 Radius=0.5 StartAngle=4.71239 EndAngle=7.85398
    g1: LineSegment StartX=0.35 StartY=5.7 StartZ=0 EndX=0.35 EndY=4.5 EndZ=0
    g2: ArcOfCircle CenterX=0.45 CenterY=5.7 CenterZ=0 NormalX=0 NormalY=0 NormalZ=1 AngleXU=0 Radius=0.1 StartAngle=3.14159 EndAngle=4.71239
    g3: ArcOfCircle CenterX=0.45 CenterY=4.5 CenterZ=0 NormalX=0 NormalY=0 NormalZ=1 AngleXU=0 Radius=0.1 StartAngle=1.5708 EndAngle=3.14159
  constraints (11):
    c: Vertical(g1)
    c: Radius(g0) = 0.5
    c: Tangent(g3,g1) = -1.5708
    c: Tangent(g1,g2) = -1.5708
    c: Angle(g2) = 1.5708
    c: Coincident(g0,g3)
    c: Angle(g3) = 1.5708
    c: Equal(g3,g2)
    c: Radius(g3) = 0.1
    c: Coincident(g1,g-3)
    c: Tangent(g0,g2) = 1.5708
FEATURE [PartDesign::Pocket] Pocket018
  BaseFeature = -> Pad023
  Length = 20
  Length2 = 100
  Placement = pos=(0,0,0) rot=(0.57735,0.57735,0.57735;2.0944rad)
  Profile = -> Sketch047
  Type = 0
FEATURE [PartDesign::LinearPattern] LinearPattern
  BaseFeature = -> Pocket018
  Direction = -> X_Axis009
  Length = 12
  Occurrences = 7
  Originals = -> [Pocket018]
  Placement = pos=(0,0,0) rot=(0.57735,0.57735,0.57735;2.0944rad)
FEATURE [Sketcher::SketchObject] Sketch048
  ExternalGeometry = -> [LinearPattern]
  MapMode = 5
  Placement = pos=(5.2e-15,3.35,-2e-16) rot=(0.57735,0.57735,0.57735;4.18879rad)
  Support = -> [LinearPattern]
  sketch-geometry (3):
    g0: Circle CenterX=-10.3121 CenterY=11 CenterZ=0 NormalX=0 NormalY=0 NormalZ=1 AngleXU=0 Radius=0.7
    g1: GeomPoint X=-10.3121 Y=17.5 Z=0
    g2: GeomPoint X=-10.3121 Y=4.5 Z=0
  constraints (6):
    c: Radius(g0) = 0.7
    c: PointOnObject(g2,g-4)
    c: PointOnObject(g1,g-3)
    c: Symmetric(g2,g1,g0)
    c: DistanceX(g-4,g0) = 11
    c: Vertical(g0,g1)
FEATURE [PartDesign::Pocket] Pocket019
  BaseFeature = -> LinearPattern
  Length = 5
  Length2 = 100
  Placement = pos=(0,0,0) rot=(0.57735,0.57735,0.57735;2.0944rad)
  Profile = -> Sketch048
  Type = 1
FEATURE [Sketcher::SketchObject] Sketch049
  ExternalGeometry = -> [Pocket019]
  MapMode = 5
  Placement = pos=(-5.2e-15,-3.35,2e-16) rot=(-0.57735,-0.57735,0.57735;4.18879rad)
  Support = -> [Pocket019]
  sketch-geometry (1):
    g0: Circle CenterX=10.3121 CenterY=11 CenterZ=0 NormalX=0 NormalY=0 NormalZ=1 AngleXU=0 Radius=1.2
  constraints (2):
    c: Radius(g0) = 1.2
    c: Coincident(g0,g-3)
FEATURE [PartDesign::Pocket] Pocket020
  BaseFeature = -> Pocket019
  Length = 3
  Length2 = 100
  Placement = pos=(0,0,0) rot=(0.57735,0.57735,0.57735;2.0944rad)
  Profile = -> Sketch049
  Type = 0
FEATURE [Sketcher::SketchObject] Sketch050
  MapMode = 5
  Placement = pos=(0,0,0) rot=(0.57735,0.57735,0.57735;2.0944rad)
  Support = -> [YZ_Plane033]
  sketch-geometry (6):
    g0: LineSegment StartX=-64.5 StartY=79 StartZ=0 EndX=92 EndY=79 EndZ=0
    g1: LineSegment StartX=100 StartY=71 StartZ=0 EndX=100 EndY=4 EndZ=0
    g2: LineSegment StartX=100 StartY=4 StartZ=0 EndX=-72.5 EndY=4 EndZ=0
    g3: LineSegment StartX=-72.5 StartY=4 StartZ=0 EndX=-72.5 EndY=71 EndZ=0
    g4: ArcOfCircle CenterX=-64.5 CenterY=71 CenterZ=0 NormalX=0 NormalY=0 NormalZ=1 AngleXU=0 Radius=8 StartAngle=1.5708 EndAngle=3.14159
    g5: ArcOfCircle CenterX=92 CenterY=71 CenterZ=0 NormalX=0 NormalY=0 NormalZ=1 AngleXU=0 Radius=8 StartAngle=0 EndAngle=1.5708
  constraints (16):
    c: Coincident(g1,g2)
    c: Coincident(g2,g3)
    c: Horizontal(g0)
    c: Vertical(g1)
    c: Vertical(g3)
    c: DistanceY(g2) = 4
    c: Tangent(g0,g4) = 1.5708
    c: Tangent(g3,g4) = 1.5708
    c: Tangent(g0,g5) = 1.5708
    c: Tangent(g1,g5) = 1.5708
    c: Equal(g5,g4)
    c: DistanceY(g1,g0) = 75
    c: Radius(g4) = 8
    c: DistanceX(g2) = -72.5
    c: DistanceX(g1) = 100
    c: Horizontal(g2)
FEATURE [PartDesign::Pad] Pad024
  Length = 4
  Length2 = 100
  Placement = pos=(0,0,0) rot=(0.57735,0.57735,0.57735;2.0944rad)
  Profile = -> Sketch050
  Type = 0
  expr: Length = SS.thickness
FEATURE [Sketcher::SketchObject] Sketch051
  MapMode = 5
  Placement = pos=(-1e-16,0,0) rot=(0.57735,0.57735,-0.57735;4.18879rad)
  Support = -> [Pad024]
  sketch-geometry (8):
    g0: Circle CenterX=-10 CenterY=-64 CenterZ=0 NormalX=0 NormalY=0 NormalZ=1 AngleXU=0 Radius=4
    g1: Circle CenterX=-48 CenterY=-64 CenterZ=0 NormalX=0 NormalY=0 NormalZ=1 AngleXU=0 Radius=4
    g2: Circle CenterX=-55.0711 CenterY=-71.0711 CenterZ=0 NormalX=0 NormalY=0 NormalZ=1 AngleXU=0 Radius=1.5
    g3: Circle CenterX=-40.9289 CenterY=-56.9289 CenterZ=0 NormalX=0 NormalY=0 NormalZ=1 AngleXU=0 Radius=1.5
    g4: Circle CenterX=-17.0711 CenterY=-71.0711 CenterZ=0 NormalX=0 NormalY=0 NormalZ=1 AngleXU=0 Radius=1.5
    g5: Circle CenterX=-2.92893 CenterY=-56.9289 CenterZ=0 NormalX=0 NormalY=0 NormalZ=1 AngleXU=0 Radius=1.5
    g6: LineSegment [constr] StartX=-17.0711 StartY=-71.0711 StartZ=0 EndX=-2.92893 EndY=-56.9289 EndZ=0
    g7: LineSegment [constr] StartX=-55.0711 StartY=-71.0711 StartZ=0 EndX=-40.9289 EndY=-56.9289 EndZ=0
  constraints (20):
    c: Equal(g1,g0)
    c: Horizontal(g0,g1)
    c: DistanceX(g1,g0) = 38
    c: Radius(g1) = 4
    c: Coincident(g7,g3)
    c: Coincident(g7,g2)
    c: Coincident(g6,g4)
    c: Coincident(g5,g6)
    c: Radius(g5) = 1.5
    c: Equal(g5,g4)
    c: Equal(g5,g2)
    c: Equal(g5,g3)
    c: Symmetric(g3,g2,g1)
    c: Symmetric(g5,g4,g0)
    c: Parallel(g6,g7)
    c: Angle(g6) = 0.785398
    c: Equal(g7,g6)
    c: Distance(g7) = 20
    c: DistanceY(g0) = -64
    c: DistanceX(g0) = -10
FEATURE [PartDesign::Pocket] Pocket021
  BaseFeature = -> Pad024
  Length = 5
  Length2 = 100
  Placement = pos=(0,0,0) rot=(0.57735,0.57735,0.57735;2.0944rad)
  Profile = -> Sketch051
  Type = 1
FEATURE [PartDesign::FeatureBase] Clone018
  BaseFeature = -> Body005
  Placement = pos=(227.8,-47.9889,63.9702) rot=(1,0,0;3.92699rad)
FEATURE [PartDesign::Body] Body034  label="shaft_support_3"
  BaseFeature = -> Body005
  Group = -> [Clone018]
  Origin = -> Origin034
  Placement = pos=(-489,0,0) rot=(0,0,1;0rad)
  Tip = -> Clone018
FEATURE [PartDesign::FeatureBase] Clone019
  BaseFeature = -> Body005
  Placement = pos=(227.8,-47.9889,63.9702) rot=(1,0,0;3.92699rad)
FEATURE [PartDesign::Body] Body035  label="shaft_support_4"
  BaseFeature = -> Body005
  Group = -> [Clone019]
  Origin = -> Origin035
  Placement = pos=(-489,38,0) rot=(0,0,1;0rad)
  Tip = -> Clone019
FEATURE [Mesh::Feature] Motor_NEMA018
  Placement = pos=(245,50,55) rot=(0,1,0;4.71239rad)
FEATURE [Sketcher::SketchObject] Sketch052
  MapMode = 5
  Placement = pos=(4,-9e-16,9e-16) rot=(0.57735,0.57735,0.57735;2.0944rad)
  Support = -> [Pocket002]
  sketch-geometry (10):
    g0: Circle CenterX=50 CenterY=55 CenterZ=0 NormalX=0 NormalY=0 NormalZ=1 AngleXU=0 Radius=11
    g1: LineSegment [constr] StartX=34.5 StartY=70.5 StartZ=0 EndX=65.5 EndY=70.5 EndZ=0
    g2: LineSegment [constr] StartX=65.5 StartY=70.5 StartZ=0 EndX=65.5 EndY=39.5 EndZ=0
    g3: LineSegment [constr] StartX=65.5 StartY=39.5 StartZ=0 EndX=34.5 EndY=39.5 EndZ=0
    g4: LineSegment [constr] StartX=34.5 StartY=39.5 StartZ=0 EndX=34.5 EndY=70.5 EndZ=0
    g5: Circle CenterX=34.5 CenterY=70.5 CenterZ=0 NormalX=0 NormalY=0 NormalZ=1 AngleXU=0 Radius=1.5
    g6: Circle CenterX=65.5 CenterY=70.5 CenterZ=0 NormalX=0 NormalY=0 NormalZ=1 AngleXU=0 Radius=1.5
    g7: Circle CenterX=65.5 CenterY=39.5 CenterZ=0 NormalX=0 NormalY=0 NormalZ=1 AngleXU=0 Radius=1.5
    g8: Circle CenterX=34.5 CenterY=39.5 CenterZ=0 NormalX=0 NormalY=0 NormalZ=1 AngleXU=0 Radius=1.5
    g9: Circle CenterX=-28 CenterY=67 CenterZ=0 NormalX=0 NormalY=0 NormalZ=1 AngleXU=0 Radius=3.25
  constraints (25):
    c: Radius(g0) = 11
    c: Coincident(g1,g2)
    c: Coincident(g2,g3)
    c: Coincident(g3,g4)
    c: Coincident(g4,g1)
    c: Horizontal(g1)
    c: Horizontal(g3)
    c: Vertical(g2)
    c: Vertical(g4)
    c: Symmetric(g2,g1,g0)
    c: Equal(g3,g4)
    c: Coincident(g5,g1)
    c: Coincident(g6,g1)
    c: Coincident(g7,g2)
    c: Coincident(g8,g3)
    c: Radius(g5) = 1.5
    c: Equal(g5,g8)
    c: Equal(g5,g7)
    c: Equal(g5,g6)
    c: DistanceX(g3,g3) = 31
    c: DistanceY(g0) = 55
    c: DistanceX(g0) = 50
    c: Radius(g9) = 3.25
    c: DistanceY(g9) = 67
    c: DistanceX(g9) = -28
FEATURE [PartDesign::Pocket] Pocket022
  BaseFeature = -> Pocket002
  Length = 5
  Length2 = 100
  Placement = pos=(0,0,0) rot=(0.57735,0.57735,0.57735;2.0944rad)
  Profile = -> Sketch052
  Type = 0
FEATURE [Sketcher::SketchObject] Sketch053
  MapMode = 5
  Placement = pos=(0,0,0) rot=(1,0,0;1.5708rad)
  Support = -> [XZ_Plane036]
  sketch-geometry (27):
    g0: LineSegment StartX=0.25 StartY=2.5 StartZ=0 EndX=0 EndY=2.75 EndZ=0
    g1: LineSegment StartX=0 StartY=2.75 StartZ=0 EndX=0 EndY=5.75 EndZ=0
    g2: LineSegment StartX=0 StartY=5.75 StartZ=0 EndX=0.25 EndY=6 EndZ=0
    g3: LineSegment StartX=0.25 StartY=6 StartZ=0 EndX=8.55 EndY=6 EndZ=0
    g4: LineSegment StartX=8.55 StartY=6 StartZ=0 EndX=9.55 EndY=5 EndZ=0
    g5: LineSegment StartX=9.55 StartY=5 StartZ=0 EndX=13.5 EndY=5 EndZ=0
    g6: LineSegment StartX=0.25 StartY=2.5 StartZ=0 EndX=13.5 EndY=2.5 EndZ=0
    g7: LineSegment StartX=13.5 StartY=2.5 StartZ=0 EndX=13.5 EndY=0 EndZ=0
    g8: LineSegment StartX=13.5 StartY=5 StartZ=0 EndX=13.5 EndY=8 EndZ=0
    g9: LineSegment StartX=13.5 StartY=8 StartZ=0 EndX=16.5 EndY=11.5 EndZ=0
    g10: LineSegment StartX=16.5 StartY=11.5 StartZ=0 EndX=17.5 EndY=11.5 EndZ=0
    g11: LineSegment StartX=17.5 StartY=11.5 StartZ=0 EndX=17.5 EndY=11.6 EndZ=0
    g12: LineSegment StartX=17.5 StartY=11.6 StartZ=0 EndX=16.5 EndY=11.6 EndZ=0
    g13: LineSegment StartX=16.5 StartY=11.6 StartZ=0 EndX=16.5 EndY=13.75 EndZ=0
    g14: ArcOfCircle CenterX=17.5 CenterY=13.75 CenterZ=0 NormalX=0 NormalY=0 NormalZ=1 AngleXU=0 Radius=1 StartAngle=1.5708 EndAngle=3.14159
    g15: LineSegment StartX=17.5 StartY=14.75 StartZ=0 EndX=21.6 EndY=14.75 EndZ=0
    g16: LineSegment StartX=21.6 StartY=14.75 StartZ=0 EndX=22.1 EndY=14.25 EndZ=0
    g17: LineSegment StartX=22.1 StartY=14.25 StartZ=0 EndX=28.6 EndY=14.25 EndZ=0
    g18: LineSegment StartX=28.6 StartY=14.25 StartZ=0 EndX=29.1 EndY=14.75 EndZ=0
    g19: LineSegment StartX=29.1 StartY=14.75 StartZ=0 EndX=40.1 EndY=14.75 EndZ=0
    g20: LineSegment StartX=40.1 StartY=14.75 StartZ=0 EndX=40.7877 EndY=10.85 EndZ=0
    g21: LineSegment StartX=40.7877 StartY=10.85 StartZ=0 EndX=51.2877 EndY=10.85 EndZ=0
    g22: LineSegment StartX=51.2877 StartY=10.85 StartZ=0 EndX=54.8232 EndY=7.31447 EndZ=0
    g23: LineSegment StartX=54.8232 StartY=7.31447 StartZ=0 EndX=54.8232 EndY=4.31447 EndZ=0
    g24: LineSegment StartX=54.8232 StartY=4.31447 StartZ=0 EndX=60.8232 EndY=3 EndZ=0
    g25: LineSegment StartX=60.8232 StartY=3 StartZ=0 EndX=60.8232 EndY=0 EndZ=0
    g26: LineSegment StartX=60.8232 StartY=0 StartZ=0 EndX=13.5 EndY=0 EndZ=0
  constraints (80):
    c: Coincident(g0,g1)
    c: Vertical(g1)
    c: Coincident(g1,g2)
    c: Coincident(g2,g3)
    c: Horizontal(g3)
    c: Coincident(g3,g4)
    c: Coincident(g4,g5)
    c: Horizontal(g5)
    c: Coincident(g6,g0)
    c: Horizontal(g6)
    c: DistanceY(g0) = 2.5
    c: Angle(g6,g0) = 2.35619
    c: Angle(g1,g2) = 2.35619
    c: DistanceY(g2) = 6
    c: Equal(g0,g2)
    c: DistanceY(g1,g1) = 3
    c: DistanceX(g3,g3) = 8.3
    c: Angle(g3,g4) = 2.35619
    c: DistanceY(g4) = 5
    c: PointOnObject(g1,g-2)
    c: DistanceX(g5) = 13.5
    c: Coincident(g7,g6)
    c: Vertical(g7)
    c: Vertical(g6,g5)
    c: Coincident(g5,g8)
    c: Vertical(g8)
    c: Coincident(g8,g9)
    c: Coincident(g9,g10)
    c: Horizontal(g10)
    c: Coincident(g10,g11)
    c: Coincident(g11,g12)
    c: Horizontal(g12)
    c: Coincident(g12,g13)
    c: Tangent(g13,g14) = 1.5708
    c: Tangent(g14,g15) = 1.5708
    c: Vertical(g11)
    c: DistanceY(g8) = 8
    c: DistanceY(g9) = 11.5
    c: DistanceX(g8,g9) = 3
    c: Equal(g12,g10)
    c: DistanceY(g11,g11) = 0.1
    c: Vertical(g13)
    c: DistanceY(g13) = 13.75
    c: Radius(g14) = 1
    c: Horizontal(g15)
    c: Coincident(g15,g16)
    c: Coincident(g16,g17)
    c: Horizontal(g17)
    c: Coincident(g17,g18)
    c: Coincident(g18,g19)
    c: Horizontal(g19)
    c: Coincident(g19,g20)
    c: Coincident(g20,g21)
    c: Horizontal(g21)
    c: Coincident(g21,g22)
    c: Coincident(g22,g23)
    c: Coincident(g23,g24)
    c: Coincident(g24,g25)
    c: Vertical(g25)
    c: Coincident(g25,g26)
    c: Coincident(g26,g7)
    c: Horizontal(g26)
    c: PointOnObject(g7,g-1)
    c: Horizontal(g15,g18)
    c: Equal(g16,g18)
    c: DistanceX(g13,g16) = 5.6
    c: DistanceX(g13,g19) = 23.6
    c: Angle(g21,g20) = 1.74533
    c: Vertical(g23)
    c: DistanceX(g17,g17) = 6.5
    c: DistanceY(g16,g15) = 0.5
    c: DistanceY(g21) = 10.85
    c: DistanceX(g21,g21) = 10.5
    c: Angle(g21,g22) = 2.35619
    c: DistanceY(g25,g25) = 3
    c: Distance(g22) = 5
    c: DistanceX(g23,g24) = 6
    c: DistanceY(g23,g23) = 3
    c: DistanceX(g10,g10) = 1
    c: Angle(g17,g16) = 2.35619
FEATURE [PartDesign::Revolution] Revolution004
  Angle = 360
  Axis = (1,0,0)
  Base = (0,0,0)
  Placement = pos=(0,0,0) rot=(1,0,0;1.5708rad)
  Profile = -> Sketch053
  ReferenceAxis = -> Sketch053 [H_Axis]
FEATURE [PartDesign::Body] Body036  label="chuck_1"
  Group = -> [Sketch053,Revolution004]
  Origin = -> Origin036
  Placement = pos=(223,50,55) rot=(0,0,1;3.14159rad)
  Tip = -> Revolution004
FEATURE [Sketcher::SketchObject] Sketch054
  MapMode = 5
  Placement = pos=(0,0,0) rot=(0.57735,0.57735,0.57735;2.0944rad)
  Support = -> [YZ_Plane037]
  sketch-geometry (9):
    g0: LineSegment StartX=-10 StartY=0 StartZ=0 EndX=10 EndY=0 EndZ=0
    g1: LineSegment StartX=10 StartY=0 StartZ=0 EndX=10 EndY=-10 EndZ=0
    g2: LineSegment StartX=10 StartY=-10 StartZ=0 EndX=-10 EndY=-10 EndZ=0
    g3: LineSegment StartX=-10 StartY=-10 StartZ=0 EndX=-10 EndY=0 EndZ=0
    g4: LineSegment StartX=8 StartY=-8 StartZ=0 EndX=-8 EndY=-8 EndZ=0
    g5: LineSegment StartX=-8 StartY=-8 StartZ=0 EndX=-8 EndY=-2 EndZ=0
    g6: LineSegment StartX=-8 StartY=-2 StartZ=0 EndX=8 EndY=-2 EndZ=0
    g7: LineSegment StartX=8 StartY=-2 StartZ=0 EndX=8 EndY=-8 EndZ=0
    g8: GeomPoint X=0 Y=-5 Z=0
  constraints (24):
    c: Coincident(g0,g1)
    c: Coincident(g1,g2)
    c: Coincident(g2,g3)
    c: Coincident(g3,g0)
    c: Horizontal(g0)
    c: Horizontal(g2)
    c: Vertical(g1)
    c: Vertical(g3)
    c: PointOnObject(g0,g-1)
    c: DistanceX(g2,g2) = 20
    c: DistanceY(g3,g3) = 10
    c: Coincident(g4,g5)
    c: Coincident(g5,g6)
    c: Coincident(g6,g7)
    c: Coincident(g7,g4)
    c: Horizontal(g4)
    c: Horizontal(g6)
    c: Vertical(g5)
    c: Vertical(g7)
    c: Symmetric(g4,g5,g8)
    c: Symmetric(g1,g0,g8)
    c: DistanceX(g2,g4) = 2
    c: DistanceY(g2,g4) = 2
    c: PointOnObject(g8,g-2)
FEATURE [PartDesign::Pad] Pad025
  Length = 500
  Length2 = 100
  Midplane = true
  Placement = pos=(0,0,0) rot=(0.57735,0.57735,0.57735;2.0944rad)
  Profile = -> Sketch054
  Type = 0
FEATURE [PartDesign::Body] Body037  label="square_profile"
  Group = -> [Sketch054,Pad025]
  Origin = -> Origin037
  Tip = -> Pad025
FEATURE [Sketcher::SketchObject] Sketch056
  MapMode = 5
  Support = -> [XY_Plane]
  sketch-geometry (4):
    g0: ArcOfCircle CenterX=-220 CenterY=50 CenterZ=0 NormalX=0 NormalY=0 NormalZ=1 AngleXU=0 Radius=2 StartAngle=1.5708 EndAngle=4.71239
    g1: ArcOfCircle CenterX=220 CenterY=50 CenterZ=0 NormalX=0 NormalY=0 NormalZ=1 AngleXU=0 Radius=2 StartAngle=4.71239 EndAngle=7.85398
    g2: LineSegment StartX=-220 StartY=48 StartZ=0 EndX=220 EndY=48 EndZ=0
    g3: LineSegment StartX=-220 StartY=52 StartZ=0 EndX=220 EndY=52 EndZ=0
  constraints (9):
    c: Tangent(g0,g3) = 1.5708
    c: Tangent(g0,g2) = -1.5708
    c: Tangent(g2,g1) = -1.5708
    c: Tangent(g3,g1) = 1.5708
    c: Horizontal(g2)
    c: Symmetric(g0,g1,g-2)
    c: Radius(g0) = 2
    c: DistanceY(g1) = 50
    c: DistanceX(g1) = 220
FEATURE [PartDesign::Pocket] Pocket023
  BaseFeature = -> Pad
  Length = 5
  Length2 = 100
  Profile = -> Sketch056
  Reversed = true
  Type = 0
FEATURE [Sketcher::SketchObject] Sketch057
  MapMode = 5
  Placement = pos=(-1e-16,0,0) rot=(0.57735,0.57735,-0.57735;4.18879rad)
  Support = -> [Pocket021]
  sketch-geometry (3):
    g0: Circle CenterX=50 CenterY=-55 CenterZ=0 NormalX=0 NormalY=0 NormalZ=1 AngleXU=0 Radius=5.5
    g1: Circle CenterX=37.5 CenterY=-55 CenterZ=0 NormalX=0 NormalY=0 NormalZ=1 AngleXU=0 Radius=1.5
    g2: Circle CenterX=62.5 CenterY=-55 CenterZ=0 NormalX=0 NormalY=0 NormalZ=1 AngleXU=0 Radius=1.5
  constraints (8):
    c: DistanceY(g0) = -55
    c: DistanceX(g0) = 50
    c: Radius(g0) = 5.5
    c: Horizontal(g1,g0)
    c: Radius(g2) = 1.5
    c: Equal(g2,g1)
    c: Symmetric(g1,g2,g0)
    c: DistanceX(g1,g2) = 25
FEATURE [PartDesign::Pocket] Pocket024
  BaseFeature = -> Pocket021
  Length = 5
  Length2 = 100
  Placement = pos=(0,0,0) rot=(0.57735,0.57735,0.57735;2.0944rad)
  Profile = -> Sketch057
  Type = 0
FEATURE [Sketcher::SketchObject] Sketch058
  MapMode = 5
  Support = -> [XY_Plane040]
  sketch-geometry (6):
    g0: LineSegment StartX=-37.5 StartY=37.5 StartZ=0 EndX=37.5 EndY=37.5 EndZ=0
    g1: LineSegment StartX=37.5 StartY=37.5 StartZ=0 EndX=37.5 EndY=-37.5 EndZ=0
    g2: LineSegment StartX=37.5 StartY=-37.5 StartZ=0 EndX=-37.5 EndY=-37.5 EndZ=0
    g3: LineSegment StartX=-37.5 StartY=-37.5 StartZ=0 EndX=-37.5 EndY=37.5 EndZ=0
    g4: Circle CenterX=25 CenterY=0 CenterZ=0 NormalX=0 NormalY=0 NormalZ=1 AngleXU=0 Radius=2
    g5: Circle CenterX=0 CenterY=0 CenterZ=0 NormalX=0 NormalY=0 NormalZ=1 AngleXU=0 Radius=2
  constraints (16):
    c: Coincident(g0,g1)
    c: Coincident(g1,g2)
    c: Coincident(g2,g3)
    c: Coincident(g3,g0)
    c: Horizontal(g0)
    c: Horizontal(g2)
    c: Vertical(g1)
    c: Vertical(g3)
    c: DistanceY(g1,g1) = 75
    c: DistanceX(g2,g2) = 75
    c: Symmetric(g1,g0,g-1)
    c: PointOnObject(g4,g-1)
    c: Radius(g4) = 2
    c: DistanceX(g4,g-1) = -25
    c: Coincident(g-1,g5)
    c: Equal(g5,g4)
FEATURE [PartDesign::Pad] Pad027
  Length = 4
  Length2 = 100
  Profile = -> Sketch058
  Type = 0
  expr: Length = SS.thickness
FEATURE [PartDesign::Body] Body040  label="support_base"
  Group = -> [Sketch058,Pad027]
  Origin = -> Origin040
  Placement = pos=(-132,50,4) rot=(0,0,1;0rad)
  Tip = -> Pad027
FEATURE [Sketcher::SketchObject] Sketch059
  MapMode = 5
  Placement = pos=(0,0,0) rot=(1,0,0;1.5708rad)
  Support = -> [XZ_Plane041]
  expr: Constraints[7] = SS.thickness
  sketch-geometry (3):
    g0: LineSegment StartX=0 StartY=4 StartZ=0 EndX=0 EndY=75 EndZ=0
    g1: LineSegment StartX=0 StartY=75 StartZ=0 EndX=-50 EndY=4 EndZ=0
    g2: LineSegment StartX=-50 StartY=4 StartZ=0 EndX=0 EndY=4 EndZ=0
  constraints (9):
    c: PointOnObject(g0,g-2)
    c: Coincident(g0,g1)
    c: Coincident(g1,g2)
    c: DistanceY(g0,g0) = 71
    c: Coincident(g0,g2)
    c: Vertical(g0)
    c: Horizontal(g2)
    c: DistanceY(g-1,g0) = 4
    c: DistanceX(g2,g2) = 50
FEATURE [PartDesign::Pad] Pad028
  Length = 4
  Length2 = 100
  Placement = pos=(0,0,0) rot=(1,0,0;1.5708rad)
  Profile = -> Sketch059
  Type = 0
  expr: Length = SS.thickness
FEATURE [PartDesign::Body] Body041
  Group = -> [Sketch059,Pad028]
  Origin = -> Origin041
  Placement = pos=(-160,19,0) rot=(0,0,1;3.14159rad)
  Tip = -> Pad028
FEATURE [PartDesign::FeatureBase] Clone021
  BaseFeature = -> Body041
  Placement = pos=(-96,19,0) rot=(0,0,1;0rad)
FEATURE [PartDesign::Body] Body042
  BaseFeature = -> Body041
  Group = -> [Clone021]
  Origin = -> Origin042
  Placement = pos=(-256,96,0) rot=(0,0,1;3.14159rad)
  Tip = -> Clone021
FEATURE [Sketcher::SketchObject] Sketch060
  MapMode = 5
  Placement = pos=(0,0,0) rot=(0.57735,0.57735,0.57735;2.0944rad)
  Support = -> [YZ_Plane043]
  sketch-geometry (4):
    g0: LineSegment StartX=-37.5 StartY=75 StartZ=0 EndX=37.5 EndY=75 EndZ=0
    g1: LineSegment StartX=37.5 StartY=75 StartZ=0 EndX=37.5 EndY=4 EndZ=0
    g2: LineSegment StartX=37.5 StartY=4 StartZ=0 EndX=-37.5 EndY=4 EndZ=0
    g3: LineSegment StartX=-37.5 StartY=4 StartZ=0 EndX=-37.5 EndY=75 EndZ=0
  constraints (11):
    c: Coincident(g0,g1)
    c: Coincident(g1,g2)
    c: Coincident(g2,g3)
    c: Coincident(g3,g0)
    c: Horizontal(g0)
    c: Vertical(g1)
    c: Vertical(g3)
    c: DistanceY(g2) = 4
    c: Symmetric(g2,g1,g-2)
    c: DistanceY(g3,g3) = 71
    c: DistanceX(g2,g2) = 75
FEATURE [PartDesign::Pad] Pad029
  Length = 4
  Length2 = 100
  Placement = pos=(0,0,0) rot=(0.57735,0.57735,0.57735;2.0944rad)
  Profile = -> Sketch060
  Type = 0
  expr: Length = SS.thickness
FEATURE [Sketcher::SketchObject] Sketch061
  MapMode = 5
  Placement = pos=(4,-9e-16,9e-16) rot=(0.57735,0.57735,0.57735;2.0944rad)
  Support = -> [Pad029]
  sketch-geometry (3):
    g0: Circle CenterX=0 CenterY=55 CenterZ=0 NormalX=0 NormalY=0 NormalZ=1 AngleXU=0 Radius=5.5
    g1: Circle CenterX=-12.5 CenterY=55 CenterZ=0 NormalX=0 NormalY=0 NormalZ=1 AngleXU=0 Radius=1.5
    g2: Circle CenterX=12.5 CenterY=55 CenterZ=0 NormalX=0 NormalY=0 NormalZ=1 AngleXU=0 Radius=1.5
  constraints (8):
    c: PointOnObject(g0,g-2)
    c: Horizontal(g0,g1)
    c: Symmetric(g1,g2,g0)
    c: Equal(g1,g2)
    c: Radius(g1) = 1.5
    c: Radius(g0) = 5.5
    c: DistanceX(g1,g2) = 25
    c: DistanceY(g0) = 55
FEATURE [PartDesign::Pocket] Pocket025
  BaseFeature = -> Pad029
  Length = 5
  Length2 = 100
  Placement = pos=(0,0,0) rot=(0.57735,0.57735,0.57735;2.0944rad)
  Profile = -> Sketch061
  Type = 0
FEATURE [PartDesign::Body] Body043
  Group = -> [Sketch060,Pad029,Sketch061,Pocket025]
  Origin = -> Origin043
  Placement = pos=(-164,50,0) rot=(0,0,1;0rad)
  Tip = -> Pocket025
FEATURE [Sketcher::SketchObject] Sketch062
  MapMode = 5
  Placement = pos=(0,0,0) rot=(1,0,0;1.5708rad)
  Support = -> [XZ_Plane044]
  sketch-geometry (13):
    g0: LineSegment StartX=0 StartY=2.5 StartZ=0 EndX=2.5 EndY=2.5 EndZ=0
    g1: LineSegment StartX=2.5 StartY=2.5 StartZ=0 EndX=2.5 EndY=3 EndZ=0
    g2: LineSegment StartX=2.5 StartY=3 StartZ=0 EndX=0.926142 EndY=3 EndZ=0
    g3: LineSegment StartX=0.926142 StartY=3 StartZ=0 EndX=2.2 EndY=2.83821 EndZ=0
    g4: LineSegment StartX=2.2 StartY=2.83821 StartZ=0 EndX=2.2 EndY=4.03249 EndZ=0
    g5: LineSegment StartX=2.2 StartY=4.03249 StartZ=0 EndX=1.84645 EndY=4.38604 EndZ=0
    g6: LineSegment StartX=1.84645 StartY=4.38604 StartZ=0 EndX=1.84645 EndY=4.91814 EndZ=0
    g7: LineSegment StartX=1.84645 StartY=4.91814 StartZ=0 EndX=0.00187 EndY=4.91127 EndZ=0
    g8: LineSegment StartX=0.00187 StartY=4.91127 StartZ=0 EndX=0.932522 EndY=5 EndZ=0
    g9: LineSegment StartX=0.932522 StartY=5 StartZ=0 EndX=2.5 EndY=5 EndZ=0
    g10: LineSegment StartX=2.5 StartY=5 StartZ=0 EndX=2.5 EndY=5.5 EndZ=0
    g11: LineSegment StartX=2.5 StartY=5.5 StartZ=0 EndX=0 EndY=5.5 EndZ=0
    g12: LineSegment StartX=0 StartY=2.5 StartZ=0 EndX=0 EndY=5.5 EndZ=0
  constraints (32):
    c: Horizontal(g0)
    c: Coincident(g0,g1)
    c: Coincident(g1,g2)
    c: Coincident(g2,g3)
    c: Coincident(g3,g4)
    c: Vertical(g4)
    c: Coincident(g4,g5)
    c: Coincident(g5,g6)
    c: Vertical(g6)
    c: Coincident(g6,g7)
    c: Coincident(g7,g8)
    c: Coincident(g8,g9)
    c: Horizontal(g9)
    c: Coincident(g9,g10)
    c: Vertical(g10)
    c: Coincident(g10,g11)
    c: Horizontal(g11)
    c: Vertical(g0,g11)
    c: Vertical(g11,g-1)
    c: DistanceY(g0) = 2.5
    c: DistanceY(g11) = 5.5
    c: Vertical(g1)
    c: DistanceY(g1,g1) = 0.5
    c: DistanceX(g3,g1) = 0.3
    c: Angle(g5,g4) = 2.35619
    c: Vertical(g1,g9)
    c: Equal(g1,g10)
    c: Horizontal(g2)
    c: Coincident(g12,g0)
    c: Coincident(g12,g11)
    c: Distance(g5) = 0.5
    c: DistanceX(g0,g0) = 2.5
FEATURE [PartDesign::Revolution] Revolution005
  Angle = 360
  Axis = (1,0,0)
  Base = (0,0,0)
  Placement = pos=(0,0,0) rot=(1,0,0;1.5708rad)
  Profile = -> Sketch062
  ReferenceAxis = -> Sketch062 [H_Axis]
FEATURE [PartDesign::Mirrored] Mirrored014
  BaseFeature = -> Revolution005
  MirrorPlane = -> YZ_Plane044
  Originals = -> [Revolution005]
  Placement = pos=(0,0,0) rot=(1,0,0;1.5708rad)
FEATURE [PartDesign::Body] Body044  label="685ZZ"
  Group = -> [Sketch062,Revolution005,Mirrored014]
  Origin = -> Origin044
  Placement = pos=(-166.5,50,55) rot=(0,0,1;0rad)
  Tip = -> Mirrored014
FEATURE [PartDesign::FeatureBase] Clone022
  BaseFeature = -> Body044
  Placement = pos=(-98.5,50,55) rot=(0,0,1;0rad)
FEATURE [PartDesign::Body] Body045  label="685ZZ_2"
  BaseFeature = -> Body044
  Group = -> [Clone022]
  Origin = -> Origin045
  Placement = pos=(-158.5,0,0) rot=(0,0,1;0rad)
  Tip = -> Clone022
FEATURE [PartDesign::FeatureBase] Clone023
  BaseFeature = -> Body036
  Placement = pos=(223,50,55) rot=(0,0,1;3.14159rad)
FEATURE [PartDesign::Body] Body046  label="chuck_2"
  BaseFeature = -> Body036
  Group = -> [Clone023]
  Origin = -> Origin046
  Placement = pos=(64,100,0) rot=(0,0,1;3.14159rad)
  Tip = -> Clone023
FEATURE [Sketcher::SketchObject] Sketch063
  MapMode = 5
  Placement = pos=(0,0,0) rot=(1,0,0;1.5708rad)
  Support = -> [XZ_Plane047]
  expr: Constraints[6] = SS.thickness
  sketch-geometry (3):
    g0: LineSegment StartX=2e-16 StartY=4 StartZ=0 EndX=40 EndY=4 EndZ=0
    g1: LineSegment StartX=40 StartY=4 StartZ=0 EndX=0 EndY=44 EndZ=0
    g2: LineSegment StartX=2e-16 StartY=44 StartZ=0 EndX=2e-16 EndY=4 EndZ=0
  constraints (9):
    c: Horizontal(g0)
    c: Coincident(g0,g1)
    c: Coincident(g1,g2)
    c: Vertical(g2)
    c: Coincident(g0,g2)
    c: PointOnObject(g0,g-2)
    c: DistanceY(g0) = 4
    c: Equal(g0,g2)
    c: DistanceX(g0,g0) = 40
FEATURE [PartDesign::Pad] Pad030
  Length = 4
  Length2 = 100
  Placement = pos=(0,0,0) rot=(1,0,0;1.5708rad)
  Profile = -> Sketch063
  Type = 0
  expr: Length = SS.thickness
FEATURE [PartDesign::Body] Body047  label="support_1"
  Group = -> [Sketch063,Pad030]
  Origin = -> Origin047
  Placement = pos=(228,80,0) rot=(0,0,1;0rad)
  Tip = -> Pad030
FEATURE [PartDesign::FeatureBase] Clone024
  BaseFeature = -> Body047
  Placement = pos=(228,80,0) rot=(0,0,1;0rad)
FEATURE [PartDesign::Body] Body048  label="support_2"
  BaseFeature = -> Body047
  Group = -> [Clone024]
  Origin = -> Origin048
  Placement = pos=(-477,-80,0) rot=(0,0,1;0rad)
  Tip = -> Clone024
FEATURE [PartDesign::FeatureBase] Clone025
  BaseFeature = -> Body048
  Placement = pos=(-477,-80,0) rot=(0,0,1;0rad)
FEATURE [PartDesign::Body] Body049  label="support_3"
  BaseFeature = -> Body048
  Group = -> [Clone025]
  Origin = -> Origin049
  Placement = pos=(0,-63,0) rot=(0,0,1;0rad)
  Tip = -> Clone025
FEATURE [PartDesign::FeatureBase] Clone026
  BaseFeature = -> Body049
  Placement = pos=(0,-63,0) rot=(0,0,1;0rad)
FEATURE [PartDesign::Body] Body050  label="support_4"
  BaseFeature = -> Body049
  Group = -> [Clone026]
  Origin = -> Origin050
  Placement = pos=(0,158,0) rot=(0,0,1;0rad)
  Tip = -> Clone026
FEATURE [Sketcher::SketchObject] Sketch064
  MapMode = 5
  Placement = pos=(-1e-16,0,0) rot=(0.57735,0.57735,-0.57735;4.18879rad)
  Support = -> [Pocket024]
  sketch-geometry (4):
    g0: LineSegment StartX=-30 StartY=-40 StartZ=0 EndX=-18 EndY=-40 EndZ=0
    g1: LineSegment StartX=-18 StartY=-40 StartZ=0 EndX=-18 EndY=-57 EndZ=0
    g2: LineSegment StartX=-18 StartY=-57 StartZ=0 EndX=-30 EndY=-57 EndZ=0
    g3: LineSegment StartX=-30 StartY=-57 StartZ=0 EndX=-30 EndY=-40 EndZ=0
  constraints (12):
    c: Coincident(g0,g1)
    c: Coincident(g1,g2)
    c: Coincident(g2,g3)
    c: Coincident(g3,g0)
    c: Horizontal(g0)
    c: Horizontal(g2)
    c: Vertical(g1)
    c: Vertical(g3)
    c: DistanceX(g1) = -18
    c: DistanceX(g2,g2) = 12
    c: DistanceY(g0) = -40
    c: DistanceY(g3,g3) = 17
FEATURE [PartDesign::Pocket] Pocket026
  BaseFeature = -> Pocket024
  Length = 5
  Length2 = 100
  Placement = pos=(0,0,0) rot=(0.57735,0.57735,0.57735;2.0944rad)
  Profile = -> Sketch064
  Type = 0
FEATURE [PartDesign::Body] Body033  label="left_plate"
  Group = -> [Sketch050,Pad024,Sketch051,Pocket021,Sketch057,Pocket024,Sketch064,Pocket026]
  Origin = -> Origin033
  Placement = pos=(-253.5,0,0) rot=(0,0,1;0rad)
  Tip = -> Pocket026
FEATURE [PartDesign::AdditiveCylinder] Cylinder
  Angle = 360
  AttacherType = Attacher::AttachEngine3D
  Height = 400
  MapMode = 5
  Placement = pos=(0,0,0) rot=(0.57735,0.57735,0.57735;2.0944rad)
  Radius = 2.5
  Support = -> [YZ_Plane051]
FEATURE [PartDesign::Body] Body051  label="chuck_shaft"
  Group = -> [Cylinder]
  Origin = -> Origin051
  Placement = pos=(-550,50,55) rot=(0,0,1;0rad)
  Tip = -> Cylinder
FEATURE [Sketcher::SketchObject] Sketch055
  MapMode = 5
  Placement = pos=(0,0,0) rot=(0.57735,0.57735,0.57735;2.0944rad)
  Support = -> [YZ_Plane038]
  sketch-geometry (8):
    g0: LineSegment StartX=-5 StartY=-9e-16 StartZ=0 EndX=-3 EndY=-9e-16 EndZ=0
    g1: LineSegment StartX=5 StartY=-9e-16 StartZ=0 EndX=5 EndY=-8 EndZ=0
    g2: LineSegment StartX=5 StartY=-8 StartZ=0 EndX=-5 EndY=-8 EndZ=0
    g3: LineSegment StartX=-5 StartY=-8 StartZ=0 EndX=-5 EndY=-9e-16 EndZ=0
    g4: LineSegment StartX=3 StartY=-9e-16 StartZ=0 EndX=3 EndY=-6 EndZ=0
    g5: LineSegment StartX=3 StartY=-6 StartZ=0 EndX=-3 EndY=-6 EndZ=0
    g6: LineSegment StartX=-3 StartY=-6 StartZ=0 EndX=-3 EndY=-9e-16 EndZ=0
    g7: LineSegment StartX=3 StartY=-9e-16 StartZ=0 EndX=5 EndY=-9e-16 EndZ=0
  constraints (23):
    c: Coincident(g7,g1)
    c: Coincident(g1,g2)
    c: Coincident(g2,g3)
    c: Coincident(g3,g0)
    c: Horizontal(g0)
    c: Horizontal(g2)
    c: Vertical(g1)
    c: Vertical(g3)
    c: Coincident(g4,g5)
    c: Coincident(g5,g6)
    c: Vertical(g4)
    c: Vertical(g6)
    c: Horizontal(g1,g4)
    c: Coincident(g0,g6)
    c: Coincident(g4,g7)
    c: Horizontal(g0,g4)
    c: DistanceY(g2,g5) = 2
    c: Equal(g0,g7)
    c: DistanceX(g0,g0) = 2
    c: DistanceX(g0,g1) = 10
    c: DistanceY(g3,g3) = 8
    c: Symmetric(g5,g4,g-2)
    c: Horizontal(g4,g-1)
FEATURE [PartDesign::Pad] Pad026
  Length = 400
  Length2 = 100
  Midplane = true
  Placement = pos=(0,0,0) rot=(0.57735,0.57735,0.57735;2.0944rad)
  Profile = -> Sketch055
  Reversed = true
  Type = 0
FEATURE [Sketcher::SketchObject] Sketch065
  MapMode = 5
  Placement = pos=(1.7e-15,-4.4e-15,-6) rot=(0,0,-1;1.5708rad)
  Support = -> [Pad026]
  sketch-geometry (3):
    g0: Circle CenterX=0 CenterY=160 CenterZ=0 NormalX=0 NormalY=0 NormalZ=1 AngleXU=0 Radius=1.6
    g1: Circle CenterX=0 CenterY=-160 CenterZ=0 NormalX=0 NormalY=0 NormalZ=1 AngleXU=0 Radius=1.6
    g2: Circle CenterX=0 CenterY=0 CenterZ=0 NormalX=0 NormalY=0 NormalZ=1 AngleXU=0 Radius=1.6
  constraints (8):
    c: PointOnObject(g0,g-2)
    c: Radius(g0) = 1.6
    c: DistanceY(g0) = 160
    c: Radius(g1) = 1.6
    c: PointOnObject(g1,g-2)
    c: DistanceY(g1) = -160
    c: Equal(g1,g2) = 1.6
    c: Coincident(g2,g-1)
FEATURE [PartDesign::Pocket] Pocket027
  BaseFeature = -> Pad026
  Length = 5
  Length2 = 100
  Placement = pos=(0,0,0) rot=(0.57735,0.57735,0.57735;2.0944rad)
  Profile = -> Sketch065
  Type = 1
FEATURE [PartDesign::Body] Body038  label="c_profile"
  Group = -> [Sketch055,Pad026,Sketch065,Pocket027]
  Origin = -> Origin038
  Placement = pos=(0,8,12) rot=(0,0,1;0rad)
  Tip = -> Pocket027
FEATURE [PartDesign::FeatureBase] Clone020
  BaseFeature = -> Body038
  Placement = pos=(0,0,12) rot=(0,0,1;0rad)
FEATURE [PartDesign::Body] Body039  label="c_profile_2"
  BaseFeature = -> Body038
  Group = -> [Clone020]
  Origin = -> Origin039
  Placement = pos=(0,92,0) rot=(0,0,1;0rad)
  Tip = -> Clone020
FEATURE [Sketcher::SketchObject] Sketch066
  MapMode = 5
  Placement = pos=(0,0,4) rot=(0,0,1;0rad)
  Support = -> [Pocket023]
  sketch-geometry (6):
    g0: Circle CenterX=-160 CenterY=92 CenterZ=0 NormalX=0 NormalY=0 NormalZ=1 AngleXU=0 Radius=1.5
    g1: Circle CenterX=-160 CenterY=8 CenterZ=0 NormalX=0 NormalY=0 NormalZ=1 AngleXU=0 Radius=1.5
    g2: Circle CenterX=0 CenterY=92 CenterZ=0 NormalX=0 NormalY=0 NormalZ=1 AngleXU=0 Radius=1.5
    g3: Circle CenterX=0 CenterY=8 CenterZ=0 NormalX=0 NormalY=0 NormalZ=1 AngleXU=0 Radius=1.5
    g4: Circle CenterX=160 CenterY=92 CenterZ=0 NormalX=0 NormalY=0 NormalZ=1 AngleXU=0 Radius=1.5
    g5: Circle CenterX=160 CenterY=8 CenterZ=0 NormalX=0 NormalY=0 NormalZ=1 AngleXU=0 Radius=1.5
  constraints (17):
    c: Vertical(g1,g0)
    c: DistanceY(g1) = 8
    c: DistanceY(g0) = 92
    c: Equal(g1,g0)
    c: Radius(g0) = 1.5
    c: DistanceX(g0) = -160
    c: Vertical(g3,g2)
    c: Equal(g3,g2)
    c: Equal(g0,g2) = 1.5
    c: PointOnObject(g3,g-2)
    c: Vertical(g5,g4)
    c: Equal(g5,g4)
    c: Horizontal(g5,g3)
    c: Horizontal(g3,g1)
    c: Horizontal(g4,g2)
    c: Symmetric(g4,g0,g-2)
    c: Equal(g5,g1)
FEATURE [PartDesign::Pocket] Pocket028
  BaseFeature = -> Pocket023
  Length = 5
  Length2 = 100
  Profile = -> Sketch066
  Type = 0
FEATURE [PartDesign::Body] Body  label="Base"
  Group = -> [Sketch,Pad,Sketch056,Pocket023,Sketch066,Pocket028]
  Origin = -> Origin
  Tip = -> Pocket028
FEATURE [Part::Feature] Part__Feature  label="PULLEY 16T GT-2"
  Placement = pos=(-218.5,-24,45) rot=(0,0,1;0rad)
  shape: bbox 14.03 x 14.03 x 8.59 mm, 166 faces (baked)
FEATURE [Sketcher::SketchObject] Sketch067
  MapMode = 5
  Placement = pos=(0,0,0) rot=(1,0,0;1.5708rad)
  Support = -> [XZ_Plane052]
  sketch-geometry (8):
    g0: LineSegment StartX=0.25 StartY=5 StartZ=0 EndX=14.75 EndY=5 EndZ=0
    g1: LineSegment StartX=14.75 StartY=5 StartZ=0 EndX=14.75 EndY=8 EndZ=0
    g2: LineSegment StartX=14.75 StartY=8 StartZ=0 EndX=-14.75 EndY=8 EndZ=0
    g3: LineSegment StartX=-14.75 StartY=8 StartZ=0 EndX=-14.75 EndY=-8 EndZ=0
    g4: LineSegment StartX=-14.75 StartY=-8 StartZ=0 EndX=14.75 EndY=-8 EndZ=0
    g5: LineSegment StartX=14.75 StartY=-8 StartZ=0 EndX=14.75 EndY=-5 EndZ=0
    g6: LineSegment StartX=14.75 StartY=-5 StartZ=0 EndX=0.25 EndY=-5 EndZ=0
    g7: LineSegment StartX=0.25 StartY=-5 StartZ=0 EndX=0.25 EndY=5 EndZ=0
  constraints (22):
    c: Horizontal(g0)
    c: Coincident(g0,g1)
    c: Vertical(g1)
    c: Coincident(g1,g2)
    c: Horizontal(g2)
    c: Coincident(g2,g3)
    c: Coincident(g3,g4)
    c: Coincident(g4,g5)
    c: Coincident(g5,g6)
    c: Coincident(g6,g7)
    c: Vertical(g7)
    c: Horizontal(g6)
    c: Coincident(g0,g7)
    c: Vertical(g5)
    c: Vertical(g1,g5)
    c: Equal(g1,g5)
    c: DistanceY(g5,g5) = 3
    c: DistanceY(g5,g0) = 10
    c: Symmetric(g2,g3,g-1)
    c: Symmetric(g4,g3,g-2)
    c: DistanceX(g3,g6) = 15
    c: DistanceX(g6,g6) = 14.5
FEATURE [PartDesign::Pad] Pad031
  Length = 10
  Length2 = 100
  Midplane = true
  Placement = pos=(0,0,0) rot=(1,0,0;1.5708rad)
  Profile = -> Sketch067
  Type = 0
FEATURE [Sketcher::SketchObject] Sketch068
  ExternalGeometry = -> [Pad031]
  MapMode = 5
  Placement = pos=(0,1.8e-15,8) rot=(0,0,1;3.14159rad)
  Support = -> [Pad031]
  sketch-geometry (1):
    g0: Circle CenterX=-8.75 CenterY=0 CenterZ=0 NormalX=0 NormalY=0 NormalZ=1 AngleXU=0 Radius=1.5
  constraints (3):
    c: PointOnObject(g0,g-1)
    c: Radius(g0) = 1.5
    c: DistanceX(g-3,g0) = 6
FEATURE [PartDesign::Pocket] Pocket029
  BaseFeature = -> Pad031
  Length = 5
  Length2 = 100
  Placement = pos=(0,0,0) rot=(1,0,0;1.5708rad)
  Profile = -> Sketch068
  Type = 1
FEATURE [Sketcher::SketchObject] Sketch070
  MapMode = 5
  Placement = pos=(-14.75,0,0) rot=(0.707107,0,-0.707107;3.14159rad)
  Support = -> [Pocket029]
  sketch-geometry (1):
    g0: Circle CenterX=0 CenterY=0 CenterZ=0 NormalX=0 NormalY=0 NormalZ=1 AngleXU=0 Radius=2
  constraints (2):
    c: Coincident(g0,g-1)
    c: Radius(g0) = 2
FEATURE [PartDesign::Pocket] Pocket030
  BaseFeature = -> Pocket029
  Length = 5
  Length2 = 100
  Placement = pos=(0,0,0) rot=(1,0,0;1.5708rad)
  Profile = -> Sketch070
  Type = 1
FEATURE [Sketcher::SketchObject] Sketch071
  MapMode = 5
  Placement = pos=(0.25,0,0) rot=(0.707107,0,0.707107;3.14159rad)
  Support = -> [Pocket030]
  sketch-geometry (1):
    g0: Circle CenterX=0 CenterY=0 CenterZ=0 NormalX=0 NormalY=0 NormalZ=1 AngleXU=0 Radius=3.5
  constraints (2):
    c: Coincident(g0,g-1)
    c: Radius(g0) = 3.5
FEATURE [PartDesign::Pocket] Pocket031
  BaseFeature = -> Pocket030
  Length = 4
  Length2 = 100
  Placement = pos=(0,0,0) rot=(1,0,0;1.5708rad)
  Profile = -> Sketch071
  Type = 0
FEATURE [PartDesign::Body] Body052  label="tensioner_part_1"
  Group = -> [Sketch067,Pad031,Sketch068,Pocket029,Sketch070,Pocket030,Sketch071,Pocket031]
  Origin = -> Origin052
  Placement = pos=(-230,-24,48.5) rot=(0,0,1;0rad)
  Tip = -> Pocket031
FEATURE [Sketcher::SketchObject] Sketch072
  MapMode = 5
  Placement = pos=(0,0,0) rot=(0.57735,0.57735,0.57735;2.0944rad)
  Support = -> [YZ_Plane053]
  sketch-geometry (8):
    g0: LineSegment StartX=-5.165 StartY=8.15 StartZ=0 EndX=5.165 EndY=8.15 EndZ=0
    g1: LineSegment StartX=5.165 StartY=8.15 StartZ=0 EndX=5.165 EndY=-8.15 EndZ=0
    g2: LineSegment StartX=5.165 StartY=-8.15 StartZ=0 EndX=-5.165 EndY=-8.15 EndZ=0
    g3: LineSegment StartX=-5.165 StartY=-8.15 StartZ=0 EndX=-5.165 EndY=8.15 EndZ=0
    g4: LineSegment StartX=-10.165 StartY=13.15 StartZ=0 EndX=10.165 EndY=13.15 EndZ=0
    g5: LineSegment StartX=10.165 StartY=13.15 StartZ=0 EndX=10.165 EndY=-13.15 EndZ=0
    g6: LineSegment StartX=10.165 StartY=-13.15 StartZ=0 EndX=-10.165 EndY=-13.15 EndZ=0
    g7: LineSegment StartX=-10.165 StartY=-13.15 StartZ=0 EndX=-10.165 EndY=13.15 EndZ=0
  constraints (22):
    c: Coincident(g0,g1)
    c: Coincident(g1,g2)
    c: Coincident(g2,g3)
    c: Coincident(g3,g0)
    c: Horizontal(g0)
    c: Horizontal(g2)
    c: Vertical(g1)
    c: Vertical(g3)
    c: DistanceX(g2,g2) = 10.33
    c: DistanceY(g3,g3) = 16.3
    c: Symmetric(g0,g1,g-1)
    c: Coincident(g4,g5)
    c: Coincident(g5,g6)
    c: Coincident(g6,g7)
    c: Coincident(g7,g4)
    c: Horizontal(g4)
    c: Horizontal(g6)
    c: Vertical(g5)
    c: Vertical(g7)
    c: DistanceX(g1,g5) = 5
    c: DistanceY(g5,g1) = 5
    c: Symmetric(g6,g4,g-1)
FEATURE [PartDesign::Pad] Pad032
  Length = 3
  Length2 = 100
  Placement = pos=(0,0,0) rot=(0.57735,0.57735,0.57735;2.0944rad)
  Profile = -> Sketch072
  Type = 0
FEATURE [Sketcher::SketchObject] Sketch073
  MapMode = 5
  Placement = pos=(0,0,0) rot=(0.57735,0.57735,-0.57735;4.18879rad)
  Support = -> [Pad032]
  sketch-geometry (16):
    g0: LineSegment StartX=-5.165 StartY=8.15 StartZ=0 EndX=5.165 EndY=8.15 EndZ=0
    g1: LineSegment StartX=5.165 StartY=-8.15 StartZ=0 EndX=-5.165 EndY=-8.15 EndZ=0
    g2: LineSegment StartX=-7.165 StartY=10.15 StartZ=0 EndX=7.165 EndY=10.15 EndZ=0
    g3: LineSegment StartX=5.165 StartY=-5 StartZ=0 EndX=7.165 EndY=-5 EndZ=0
    g4: LineSegment StartX=7.165 StartY=-5 StartZ=0 EndX=7.165 EndY=-10.15 EndZ=0
    g5: LineSegment StartX=5.165 StartY=-8.15 StartZ=0 EndX=5.165 EndY=-5 EndZ=0
    g6: LineSegment StartX=7.165 StartY=5 StartZ=0 EndX=5.165 EndY=5 EndZ=0
    g7: LineSegment StartX=5.165 StartY=5 StartZ=0 EndX=5.165 EndY=8.15 EndZ=0
    g8: LineSegment StartX=7.165 StartY=10.15 StartZ=0 EndX=7.165 EndY=5 EndZ=0
    g9: LineSegment StartX=-5.165 StartY=8.15 StartZ=0 EndX=-5.165 EndY=5 EndZ=0
    g10: LineSegment StartX=-5.165 StartY=5 StartZ=0 EndX=-7.165 EndY=5 EndZ=0
    g11: LineSegment StartX=-7.165 StartY=5 StartZ=0 EndX=-7.165 EndY=10.15 EndZ=0
    g12: LineSegment StartX=-7.165 StartY=-5 StartZ=0 EndX=-5.165 EndY=-5 EndZ=0
    g13: LineSegment StartX=-5.165 StartY=-5 StartZ=0 EndX=-5.165 EndY=-8.15 EndZ=0
    g14: LineSegment StartX=-7.165 StartY=-10.15 StartZ=0 EndX=-7.165 EndY=-5 EndZ=0
    g15: LineSegment StartX=-7.165 StartY=-10.15 StartZ=0 EndX=7.165 EndY=-10.15 EndZ=0
  constraints (48):
    c: Horizontal(g1)
    c: Horizontal(g2)
    c: Coincident(g3,g4)
    c: Coincident(g5,g3)
    c: Horizontal(g3)
    c: Vertical(g4)
    c: Vertical(g5)
    c: Coincident(g6,g7)
    c: Coincident(g8,g6)
    c: Horizontal(g6)
    c: Vertical(g7)
    c: Vertical(g8)
    c: Coincident(g9,g10)
    c: Coincident(g10,g11)
    c: Horizontal(g10)
    c: Vertical(g9)
    c: Vertical(g11)
    c: Coincident(g12,g13)
    c: Coincident(g14,g12)
    c: Horizontal(g12)
    c: Vertical(g13)
    c: Vertical(g14)
    c: Horizontal(g15)
    c: Coincident(g4,g15)
    c: Coincident(g14,g15)
    c: Coincident(g1,g13)
    c: Coincident(g1,g5)
    c: Coincident(g0,g7)
    c: Coincident(g2,g8)
    c: Coincident(g0,g9)
    c: Coincident(g2,g11)
    c: Vertical(g10,g12)
    c: Vertical(g3,g6)
    c: DistanceY(g14,g1) = 2
    c: DistanceX(g12,g12) = 2
    c: Equal(g3,g12)
    c: Horizontal(g3,g12)
    c: Horizontal(g6,g9)
    c: Equal(g12,g6)
    c: Equal(g6,g3)
    c: Equal(g3,g10)
    c: Symmetric(g0,g0,g-2)
    c: Symmetric(g2,g4,g-1)
    c: Symmetric(g6,g3,g-1)
    c: Equal(g7,g5)
    c: DistanceY(g1,g0) = 16.3
    c: DistanceX(g0,g0) = 10.33
    c: DistanceY(g3,g6) = 10
FEATURE [PartDesign::Pad] Pad033
  BaseFeature = -> Pad032
  Length = 20
  Length2 = 100
  Placement = pos=(0,0,0) rot=(0.57735,0.57735,0.57735;2.0944rad)
  Profile = -> Sketch073
  Type = 0
FEATURE [Sketcher::SketchObject] Sketch074
  ExternalGeometry = -> [Pad033]
  MapMode = 5
  Placement = pos=(0,0,0) rot=(1,0,0;1.5708rad)
  Support = -> [XZ_Plane053]
  sketch-geometry (4):
    g0: LineSegment StartX=-20 StartY=-10.15 StartZ=0 EndX=3.6e-15 EndY=-10.15 EndZ=0
    g1: LineSegment StartX=4.7e-15 StartY=-10.15 StartZ=0 EndX=4.7e-15 EndY=-13.15 EndZ=0
    g2: LineSegment StartX=4.7e-15 StartY=-13.15 StartZ=0 EndX=-19.1044 EndY=-11.1445 EndZ=0
    g3: ArcOfCircle CenterX=-19 CenterY=-10.15 CenterZ=0 NormalX=0 NormalY=0 NormalZ=1 AngleXU=0 Radius=1 StartAngle=3.14159 EndAngle=4.6078
  constraints (10):
    c: Coincident(g0,g-3)
    c: Coincident(g0,g1)
    c: Coincident(g1,g2)
    c: Tangent(g2,g3) = 1.5708
    c: Coincident(g3,g-3)
    c: Coincident(g0,g3)
    c: Vertical(g1)
    c: Radius(g3) = 1
    c: DistanceY(g1,g1) = 3
    c: Perpendicular(g3,g0)
FEATURE [PartDesign::Pad] Pad034
  BaseFeature = -> Pad033
  Length = 2
  Length2 = 100
  Midplane = true
  Placement = pos=(0,0,0) rot=(0.57735,0.57735,0.57735;2.0944rad)
  Profile = -> Sketch074
  Type = 0
FEATURE [PartDesign::Mirrored] Mirrored015
  BaseFeature = -> Pad034
  MirrorPlane = -> XY_Plane053
  Originals = -> [Pad034]
  Placement = pos=(0,0,0) rot=(0.57735,0.57735,0.57735;2.0944rad)
FEATURE [PartDesign::Body] Body053  label="tensioner_part_2"
  Group = -> [Sketch072,Pad032,Sketch073,Pad033,Sketch074,Pad034,Mirrored015]
  Origin = -> Origin053
  Placement = pos=(-247,-24,48.5) rot=(0,0,1;3.14159rad)
  Tip = -> Mirrored015
FEATURE [Sketcher::SketchObject] Sketch075
  MapMode = 5
  Placement = pos=(0,0,0) rot=(0.57735,0.57735,0.57735;2.0944rad)
  Support = -> [YZ_Plane054]
  sketch-geometry (2):
    g0: Circle CenterX=0 CenterY=0 CenterZ=0 NormalX=0 NormalY=0 NormalZ=1 AngleXU=0 Radius=11
    g1: Circle CenterX=0 CenterY=0 CenterZ=0 NormalX=0 NormalY=0 NormalZ=1 AngleXU=0 Radius=1.7
  constraints (4):
    c: Coincident(g0,g-1)
    c: Coincident(g1,g0)
    c: Radius(g1) = 1.7
    c: Radius(g0) = 11
FEATURE [PartDesign::Pad] Pad035
  Length = 5
  Length2 = 100
  Placement = pos=(0,0,0) rot=(0.57735,0.57735,0.57735;2.0944rad)
  Profile = -> Sketch075
  Type = 0
FEATURE [PartDesign::Body] Body054  label="tensioner_part_3"
  Group = -> [Sketch075,Pad035]
  Origin = -> Origin054
  Placement = pos=(-259,-24,48.5) rot=(0,0,1;0rad)
  Tip = -> Pad035
FEATURE [PartDesign::FeatureBase] Clone027
  BaseFeature = -> Body028
  Placement = pos=(6,16,97) rot=(0,0,1;0rad)
FEATURE [PartDesign::Body] Body055  label="knob_2"
  BaseFeature = -> Body028
  Group = -> [Clone027]
  Origin = -> Origin055
  Tip = -> Clone027
FEATURE [Mesh::Feature] suich
  Placement = pos=(216.393,-28,66.7003) rot=(0.707107,0,0.707107;3.14159rad)
FEATURE [Sketcher::SketchObject] Sketch076
  MapMode = 5
  Placement = pos=(0,0,4) rot=(0,0,1;0rad)
  Support = -> [Pocket001]
  sketch-geometry (1):
    g0: Circle CenterX=-19.6946 CenterY=-30.2846 CenterZ=0 NormalX=0 NormalY=0 NormalZ=1 AngleXU=0 Radius=2.5
  constraints (1):
    c: Radius(g0) = 2.5
FEATURE [PartDesign::Pocket] Pocket032
  BaseFeature = -> Pocket001
  Length = 5
  Length2 = 100
  Profile = -> Sketch076
  Type = 0
FEATURE [PartDesign::Body] Body004  label="motor_plate"
  Group = -> [Sketch004,Pad003,Sketch005,Pocket001,Sketch076,Pocket032]
  Origin = -> Origin004
  Placement = pos=(251.5,-24.2,38) rot=(0,0,1;0rad)
  Tip = -> Pocket032
FEATURE [Sketcher::SketchObject] Sketch077
  MapMode = 5
  Placement = pos=(0,0,0) rot=(0.57735,0.57735,0.57735;2.0944rad)
  Support = -> [YZ_Plane056]
  sketch-geometry (15):
    g0: Circle CenterX=0 CenterY=0 CenterZ=0 NormalX=0 NormalY=0 NormalZ=1 AngleXU=0 Radius=5.5
    g1: Circle CenterX=-12.5 CenterY=-3e-16 CenterZ=0 NormalX=0 NormalY=0 NormalZ=1 AngleXU=0 Radius=2
    g2: Circle CenterX=12.5 CenterY=3e-16 CenterZ=0 NormalX=0 NormalY=0 NormalZ=1 AngleXU=0 Radius=2
    g3: ArcOfCircle CenterX=-12.5 CenterY=-3e-16 CenterZ=0 NormalX=0 NormalY=0 NormalZ=1 AngleXU=0 Radius=5 StartAngle=3.14159 EndAngle=4.118
    g4: ArcOfCircle CenterX=0 CenterY=0 CenterZ=0 NormalX=0 NormalY=0 NormalZ=1 AngleXU=0 Radius=12 StartAngle=4.118 EndAngle=4.71239
    g5: LineSegment StartX=-6.72 StartY=-9.94191 StartZ=0 EndX=-15.3 EndY=-4.14246 EndZ=0
    g6: ArcOfCircle CenterX=12.5 CenterY=3e-16 CenterZ=0 NormalX=0 NormalY=0 NormalZ=1 AngleXU=0 Radius=5 StartAngle=5.30677 EndAngle=6.28319
    g7: LineSegment StartX=6.72 StartY=-9.94191 StartZ=0 EndX=15.3 EndY=-4.14246 EndZ=0
    g8: ArcOfCircle CenterX=0 CenterY=0 CenterZ=0 NormalX=0 NormalY=0 NormalZ=1 AngleXU=0 Radius=12 StartAngle=4.71239 EndAngle=5.30677
    g9: LineSegment StartX=6.72 StartY=9.94191 StartZ=0 EndX=15.3 EndY=4.14246 EndZ=0
    g10: ArcOfCircle CenterX=12.5 CenterY=3e-16 CenterZ=0 NormalX=0 NormalY=0 NormalZ=1 AngleXU=0 Radius=5 StartAngle=0 EndAngle=0.976411
    g11: ArcOfCircle CenterX=0 CenterY=0 CenterZ=0 NormalX=0 NormalY=0 NormalZ=1 AngleXU=0 Radius=12 StartAngle=0.976411 EndAngle=1.5708
    g12: ArcOfCircle CenterX=0 CenterY=0 CenterZ=0 NormalX=0 NormalY=0 NormalZ=1 AngleXU=0 Radius=12 StartAngle=1.5708 EndAngle=2.16518
    g13: LineSegment StartX=-6.72 StartY=9.94191 StartZ=0 EndX=-15.3 EndY=4.14246 EndZ=0
    g14: ArcOfCircle CenterX=-12.5 CenterY=-3e-16 CenterZ=0 NormalX=0 NormalY=0 NormalZ=1 AngleXU=0 Radius=5 StartAngle=2.16518 EndAngle=3.14159
  constraints (41):
    c: Coincident(g0,g-1)
    c: Radius(g0) = 5.5
    c: Equal(g2,g1)
    c: Radius(g1) = 2
    c: DistanceX(g1,g2) = 25
    c: Symmetric(g2,g1,g0)
    c: Coincident(g3,g1)
    c: Coincident(g4,g0)
    c: Tangent(g5,g3) = 1.5708
    c: Tangent(g4,g5) = 1.5708
    c: DistanceY(g4) = -12
    c: Radius(g3) = 5
    c: PointOnObject(g3,g-1)
    c: Tangent(g7,g6) = -1.5708
    c: Tangent(g8,g7) = -1.5708
    c: Tangent(g13,g14) = -1.5708
    c: Tangent(g12,g13) = -1.5708
    c: Tangent(g9,g10) = 1.5708
    c: Tangent(g11,g9) = 1.5708
    c: Equal(g13,g5)
    c: Equal(g5,g7)
    c: Equal(g7,g9)
    c: Coincident(g0,g8)
    c: Coincident(g0,g11)
    c: Coincident(g0,g12)
    c: Coincident(g1,g14)
    c: Coincident(g2,g6)
    c: Coincident(g2,g10)
    c: Symmetric(g13,g3,g-1)
    c: Symmetric(g12,g4,g-1)
    c: Symmetric(g9,g7,g-1)
    c: Symmetric(g11,g4,g-1)
    c: Symmetric(g3,g6,g-2)
    c: Symmetric(g7,g4,g-2)
    c: Symmetric(g6,g9,g-1)
    c: Symmetric(g13,g9,g-2)
    c: Symmetric(g3,g6,g-2)
    c: Coincident(g6,g10)
    c: Coincident(g11,g12)
    c: Coincident(g4,g8)
    c: Coincident(g3,g14)
FEATURE [PartDesign::Pad] Pad036
  Length = 6
  Length2 = 100
  Placement = pos=(0,0,0) rot=(0.57735,0.57735,0.57735;2.0944rad)
  Profile = -> Sketch077
  Type = 0
FEATURE [PartDesign::Body] Body056  label="bearing_holder"
  Group = -> [Sketch077,Pad036]
  Origin = -> Origin056
  Placement = pos=(-170,50,55) rot=(0,0,1;0rad)
  Tip = -> Pad036
FEATURE [PartDesign::FeatureBase] Clone028
  BaseFeature = -> Body056
  Placement = pos=(-170,50,55) rot=(0,0,1;0rad)
FEATURE [PartDesign::Body] Body057  label="bearing_holer_1"
  BaseFeature = -> Body056
  Group = -> [Clone028]
  Origin = -> Origin057
  Placement = pos=(-90,0,0) rot=(0,0,1;0rad)
  Tip = -> Clone028
FEATURE [Sketcher::SketchObject] Sketch078
  MapMode = 5
  Placement = pos=(0,0,0) rot=(1,0,0;1.5708rad)
  Support = -> [XZ_Plane058]
  sketch-geometry (6):
    g0: LineSegment StartX=35 StartY=0 StartZ=0 EndX=0 EndY=0 EndZ=0
    g1: LineSegment StartX=0 StartY=0 StartZ=0 EndX=0 EndY=4.2 EndZ=0
    g2: LineSegment StartX=0 StartY=4.2 StartZ=0 EndX=38 EndY=4.2 EndZ=0
    g3: LineSegment StartX=38 StartY=4.2 StartZ=0 EndX=38 EndY=3.2 EndZ=0
    g4: LineSegment StartX=38 StartY=3.2 StartZ=0 EndX=35 EndY=3.2 EndZ=0
    g5: LineSegment StartX=35 StartY=3.2 StartZ=0 EndX=35 EndY=0 EndZ=0
  constraints (17):
    c: PointOnObject(g0,g-1)
    c: Coincident(g0,g1)
    c: Vertical(g1)
    c: Coincident(g1,g2)
    c: Horizontal(g2)
    c: Coincident(g2,g3)
    c: Coincident(g3,g4)
    c: Horizontal(g4)
    c: Coincident(g4,g5)
    c: Vertical(g5)
    c: Coincident(g0,g5)
    c: DistanceY(g5,g5) = 3.2
    c: Vertical(g3)
    c: DistanceX(g4,g4) = 3
    c: DistanceY(g3,g3) = 1
    c: DistanceX(g0,g0) = 35
    c: Coincident(g0,g-1)
FEATURE [Sketcher::SketchObject] Sketch079
  MapMode = 5
  Placement = pos=(4,-9e-16,9e-16) rot=(0.57735,0.57735,0.57735;2.0944rad)
  Support = -> [Pocket022]
  sketch-geometry (4):
    g0: LineSegment StartX=20 StartY=15 StartZ=0 EndX=36 EndY=15 EndZ=0
    g1: LineSegment StartX=36 StartY=15 StartZ=0 EndX=36 EndY=10 EndZ=0
    g2: LineSegment StartX=36 StartY=10 StartZ=0 EndX=20 EndY=10 EndZ=0
    g3: LineSegment StartX=20 StartY=10 StartZ=0 EndX=20 EndY=15 EndZ=0
  constraints (12):
    c: Coincident(g0,g1)
    c: Coincident(g1,g2)
    c: Coincident(g2,g3)
    c: Coincident(g3,g0)
    c: Horizontal(g0)
    c: Horizontal(g2)
    c: Vertical(g1)
    c: Vertical(g3)
    c: DistanceX(g2,g2) = 16
    c: DistanceY(g3,g3) = 5
    c: DistanceY(g2) = 10
    c: DistanceX(g2) = 20
FEATURE [PartDesign::Pocket] Pocket033
  BaseFeature = -> Pocket022
  Length = 5
  Length2 = 100
  Placement = pos=(0,0,0) rot=(0.57735,0.57735,0.57735;2.0944rad)
  Profile = -> Sketch079
  Type = 0
FEATURE [PartDesign::Body] Body001  label="right_plate"
  Group = -> [Sketch001,Pad001,Sketch002,Pocket,Sketch006,Pocket002,Sketch052,Pocket022,Sketch079,Pocket033]
  Origin = -> Origin001
  Placement = pos=(224,0,0) rot=(0,0,1;0rad)
  Tip = -> Pocket033
  expr: Placement.Base.x = 550 / 2 - 45 - 2
FEATURE [PartDesign::Revolution] Revolution006
  Angle = 360
  Axis = (1,0,0)
  Base = (0,0,0)
  Placement = pos=(0,0,0) rot=(1,0,0;1.5708rad)
  Profile = -> Sketch078
  ReferenceAxis = -> X_Axis058
  Reversed = true
FEATURE [PartDesign::Body] Body058
  Group = -> [Sketch078,Revolution006]
  Origin = -> Origin058
  Placement = pos=(181.5,-28,66.5) rot=(0,0,1;0rad)
  Tip = -> Revolution006
FEATURE [Sketcher::SketchObject] Sketch080
  MapMode = 5
  Placement = pos=(0,0,0) rot=(1,0,0;1.5708rad)
  Support = -> [XZ_Plane009]
  sketch-geometry (4):
    g0: LineSegment StartX=-17.5 StartY=8.5 StartZ=0 EndX=-17.5 EndY=7.5 EndZ=0
    g1: LineSegment StartX=-17.5 StartY=7.5 StartZ=0 EndX=-18.2 EndY=8 EndZ=0
    g2: LineSegment StartX=-18.2 StartY=8 StartZ=0 EndX=-17.5 EndY=8.5 EndZ=0
    g3: LineSegment [constr] StartX=-17.5 StartY=8 StartZ=0 EndX=-15.1718 EndY=8 EndZ=0
  constraints (12):
    c: Coincident(g0,g1)
    c: Coincident(g1,g2)
    c: Coincident(g2,g0)
    c: Vertical(g0)
    c: Equal(g2,g1)
    c: DistanceY(g0,g0) = 1
    c: DistanceX(g0,g1) = -0.7
    c: DistanceY(g1) = 8
    c: DistanceX(g0) = -17.5
    c: PointOnObject(g3,g0)
    c: Horizontal(g3)
    c: Horizontal(g3,g1)
FEATURE [PartDesign::Pad] Pad037
  BaseFeature = -> Pocket020
  Length = 7.45
  Length2 = 100
  Placement = pos=(0,0,0) rot=(0.57735,0.57735,0.57735;2.0944rad)
  Profile = -> Sketch080
  Type = 0
FEATURE [PartDesign::PolarPattern] PolarPattern002
  Angle = 360
  Axis = -> Sketch080 [Axis0]
  BaseFeature = -> Pad037
  Occurrences = 36
  Originals = -> [Pad037]
  Placement = pos=(0,0,0) rot=(0.57735,0.57735,0.57735;2.0944rad)
FEATURE [Sketcher::SketchObject] Sketch081
  ExternalGeometry = -> [PolarPattern002]
  MapMode = 5
  Placement = pos=(-17.5,-1.98e-14,1.81e-14) rot=(-0.57735,-0.57735,0.57735;2.0944rad)
  Support = -> [PolarPattern002]
  sketch-geometry (1):
    g0: Circle CenterX=-4.8e-15 CenterY=-8.05 CenterZ=0 NormalX=0 NormalY=0 NormalZ=1 AngleXU=0 Radius=5.5
  constraints (2):
    c: Coincident(g0,g-3)
    c: PointOnObject(g-3,g0)
FEATURE [PartDesign::Pocket] Pocket034
  BaseFeature = -> PolarPattern002
  Length = 5
  Length2 = 100
  Placement = pos=(0,0,0) rot=(0.57735,0.57735,0.57735;2.0944rad)
  Profile = -> Sketch081
  Reversed = true
  Type = 0
FEATURE [PartDesign::Body] Body009  label="carriage"
  Group = -> [Sketch014,Pad006,Sketch015,Pocket007,MultiTransform,Mirrored,Mirrored001,Sketch016,Pocket008,Sketch017,Pocket009,Sketch018,Pad007,Mirrored002,Mirrored003,Mirrored004,Chamfer001,Sketch019,Pad008,Mirrored005,Sketch020,Pad009,Sketch021,Pad010,Sketch022,Pocket010,Sketch023,Pocket011,Mirrored006,Mirrored007,Mirrored008,Sketch045,Pad022,Sketch046,Pad023,Sketch047,Pocket018,LinearPattern,Sketch048,+8 more]
  Origin = -> Origin009
  Placement = pos=(0,-29,64) rot=(0,0,1;0rad)
  Tip = -> Pocket034
FEATURE [Sketcher::SketchObject] Sketch082
  ExternalGeometry = -> [Pocket017]
  MapMode = 5
  Placement = pos=(0,0,0) rot=(1,0,0;3.14159rad)
  Support = -> [Pocket017]
  sketch-geometry (4):
    g0: LineSegment StartX=-17.5 StartY=-53.2815 StartZ=0 EndX=17.5 EndY=-53.2815 EndZ=0
    g1: LineSegment StartX=17.5 StartY=-53.2815 StartZ=0 EndX=17.5 EndY=-107.16 EndZ=0
    g2: LineSegment StartX=17.5 StartY=-107.16 StartZ=0 EndX=-17.5 EndY=-107.16 EndZ=0
    g3: LineSegment StartX=-17.5 StartY=-107.16 StartZ=0 EndX=-17.5 EndY=-53.2815 EndZ=0
  constraints (9):
    c: Coincident(g0,g1)
    c: Coincident(g1,g2)
    c: Coincident(g2,g3)
    c: Coincident(g3,g0)
    c: Horizontal(g2)
    c: Vertical(g1)
    c: Vertical(g3)
    c: Coincident(g0,g-3)
    c: Coincident(g0,g-4)
FEATURE [PartDesign::Pocket] Pocket035
  BaseFeature = -> Pocket017
  Length = 5
  Length2 = 100
  Profile = -> Sketch082
  Type = 1
FEATURE [Sketcher::SketchObject] Sketch083
  ExternalGeometry = -> [Pocket035]
  MapMode = 5
  Placement = pos=(0,0,0) rot=(0.57735,0.57735,0.57735;2.0944rad)
  Support = -> [YZ_Plane010]
  sketch-geometry (5):
    g0: Circle CenterX=56.9815 CenterY=-0.7 CenterZ=0 NormalX=0 NormalY=0 NormalZ=1 AngleXU=0 Radius=1.7
    g1: ArcOfCircle CenterX=56.9815 CenterY=-0.7 CenterZ=0 NormalX=0 NormalY=0 NormalZ=1 AngleXU=0 Radius=3.7 StartAngle=3.14159 EndAngle=7.85398
    g2: LineSegment StartX=56.9815 StartY=3 StartZ=0 EndX=53.2815 EndY=3 EndZ=0
    g3: LineSegment StartX=53.2815 StartY=1.95e-14 StartZ=0 EndX=53.2815 EndY=-0.7 EndZ=0
    g4: LineSegment StartX=53.2815 StartY=3 StartZ=0 EndX=53.2815 EndY=1.95e-14 EndZ=0
  constraints (11):
    c: Coincident(g1,g0)
    c: Coincident(g2,g-3)
    c: Horizontal(g2)
    c: Tangent(g2,g1) = -1.5708
    c: Radius(g0) = 1.7
    c: Coincident(g3,g-3)
    c: Vertical(g3)
    c: Radius(g1) = 3.7
    c: Tangent(g3,g1) = -1.5708
    c: Coincident(g4,g2)
    c: Coincident(g4,g3)
FEATURE [PartDesign::Pad] Pad038
  BaseFeature = -> Pocket035
  Length = 35
  Length2 = 100
  Midplane = true
  Profile = -> Sketch083
  Type = 0
FEATURE [Sketcher::SketchObject] Sketch084
  ExternalGeometry = -> [Pad038]
  MapMode = 5
  Placement = pos=(-8e-16,7e-16,3) rot=(0,0,1;0rad)
  Support = -> [Pad038]
  sketch-geometry (21):
    g0: LineSegment StartX=-5.83333 StartY=53.2815 StartZ=0 EndX=-1.94444 EndY=53.2815 EndZ=0
    g1: LineSegment StartX=-1.94444 StartY=53.2815 StartZ=0 EndX=-1.94444 EndY=70 EndZ=0
    g2: LineSegment StartX=-1.94444 StartY=70 StartZ=0 EndX=-5.83333 EndY=70 EndZ=0
    g3: LineSegment StartX=-5.83333 StartY=70 StartZ=0 EndX=-5.83333 EndY=53.2815 EndZ=0
    g4: LineSegment StartX=1.94444 StartY=53.2815 StartZ=0 EndX=5.83333 EndY=53.2815 EndZ=0
    g5: LineSegment StartX=5.83333 StartY=53.2815 StartZ=0 EndX=5.83333 EndY=70 EndZ=0
    g6: LineSegment StartX=5.83333 StartY=70 StartZ=0 EndX=1.94444 EndY=70 EndZ=0
    g7: LineSegment StartX=1.94444 StartY=70 StartZ=0 EndX=1.94444 EndY=53.2815 EndZ=0
    g8: LineSegment StartX=9.72222 StartY=53.2815 StartZ=0 EndX=13.6111 EndY=53.2815 EndZ=0
    g9: LineSegment StartX=13.6111 StartY=53.2815 StartZ=0 EndX=13.6111 EndY=70 EndZ=0
    g10: LineSegment StartX=13.6111 StartY=70 StartZ=0 EndX=9.72222 EndY=70 EndZ=0
    g11: LineSegment StartX=9.72222 StartY=70 StartZ=0 EndX=9.72222 EndY=53.2815 EndZ=0
    g12: LineSegment StartX=-13.6111 StartY=53.2815 StartZ=0 EndX=-9.72222 EndY=53.2815 EndZ=0
    g13: LineSegment StartX=-9.72222 StartY=53.2815 StartZ=0 EndX=-9.72222 EndY=70 EndZ=0
    g14: LineSegment StartX=-9.72222 StartY=70 StartZ=0 EndX=-13.6111 EndY=70 EndZ=0
    g15: LineSegment StartX=-13.6111 StartY=70 StartZ=0 EndX=-13.6111 EndY=53.2815 EndZ=0
    g16: LineSegment [constr] StartX=-9.72222 StartY=70 StartZ=0 EndX=-5.83333 EndY=70 EndZ=0
    g17: LineSegment [constr] StartX=-1.94444 StartY=70 StartZ=0 EndX=1.94444 EndY=70 EndZ=0
    g18: LineSegment [constr] StartX=5.83333 StartY=70 StartZ=0 EndX=9.72222 EndY=70 EndZ=0
    g19: LineSegment [constr] StartX=-13.6111 StartY=70 StartZ=0 EndX=-17.5 EndY=70 EndZ=0
    g20: LineSegment [constr] StartX=13.6111 StartY=70 StartZ=0 EndX=17.5 EndY=70 EndZ=0
  constraints (60):
    c: Coincident(g0,g1)
    c: Coincident(g1,g2)
    c: Coincident(g2,g3)
    c: Coincident(g3,g0)
    c: Horizontal(g0)
    c: Horizontal(g2)
    c: Vertical(g1)
    c: Vertical(g3)
    c: Coincident(g4,g5)
    c: Coincident(g5,g6)
    c: Coincident(g6,g7)
    c: Coincident(g7,g4)
    c: Horizontal(g4)
    c: Horizontal(g6)
    c: Vertical(g5)
    c: Vertical(g7)
    c: Coincident(g8,g9)
    c: Coincident(g9,g10)
    c: Coincident(g10,g11)
    c: Coincident(g11,g8)
    c: Horizontal(g8)
    c: Horizontal(g10)
    c: Vertical(g9)
    c: Vertical(g11)
    c: Horizontal(g1,g10)
    c: Coincident(g12,g13)
    c: Coincident(g13,g14)
    c: Coincident(g14,g15)
    c: Coincident(g15,g12)
    c: Horizontal(g12)
    c: Horizontal(g14)
    c: Vertical(g13)
    c: Vertical(g15)
    c: Horizontal(g13,g2)
    c: Coincident(g16,g13)
    c: Coincident(g16,g2)
    c: Coincident(g17,g1)
    c: Coincident(g17,g6)
    c: Horizontal(g17)
    c: Coincident(g18,g5)
    c: Coincident(g18,g10)
    c: Coincident(g19,g14)
    c: Coincident(g20,g9)
    c: Horizontal(g20)
    c: Horizontal(g19)
    c: Equal(g19,g16)
    c: Equal(g16,g17)
    c: Equal(g17,g18)
    c: Equal(g18,g20)
    c: Equal(g14,g2)
    c: Equal(g2,g6)
    c: Equal(g6,g10)
    c: PointOnObject(g12,g-3)
    c: PointOnObject(g0,g-3)
    c: PointOnObject(g4,g-3)
    c: PointOnObject(g8,g-3)
    c: Vertical(g19,g-3)
    c: Vertical(g20,g-3)
    c: Equal(g20,g10)
    c: DistanceY(g19) = 70
FEATURE [PartDesign::Pocket] Pocket036
  BaseFeature = -> Pad038
  Length = 5
  Length2 = 100
  Profile = -> Sketch084
  Type = 1
FEATURE [PartDesign::Body] Body010  label="car"
  Group = -> [Sketch024,Pad011,Sketch025,Pad012,Sketch026,Pocket012,Mirrored009,Mirrored010,Sketch027,Pad013,MultiTransform001,Mirrored011,Mirrored012,Sketch028,Pocket013,Sketch029,Pad014,Sketch034,Pocket015,Sketch035,Pad016,Mirrored013,Sketch039,Pad017,Sketch042,Pad020,Sketch043,Pocket017,Sketch082,Pocket035,Sketch083,Pad038,Sketch084,Pocket036]
  Origin = -> Origin010
  Placement = pos=(0,-29,86) rot=(0,0,1;0rad)
  Tip = -> Pocket036
